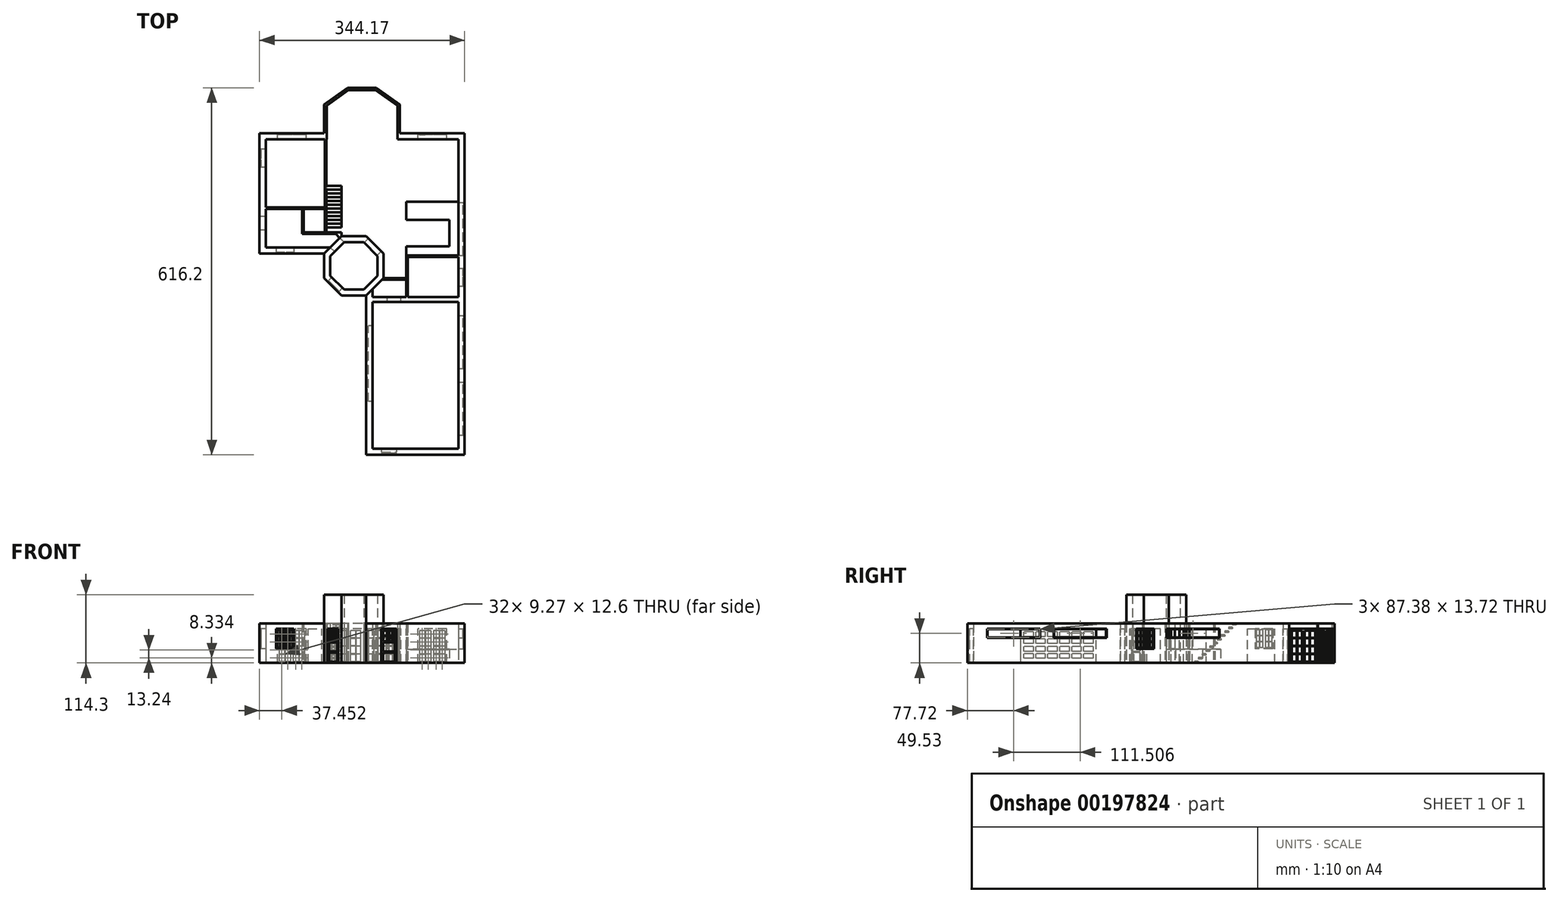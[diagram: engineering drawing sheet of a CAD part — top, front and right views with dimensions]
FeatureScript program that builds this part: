
annotation { "Feature Type Name" : "Feature", "Feature Type Description" : "" }
export const myFeature = defineFeature(function(context is Context, id is Id, definition is map)
    precondition{}
    {
        {
            var Q0;
            Q0=qCreatedBy(makeId("Top.planeOp"),FACE);
            var sketch = newSketch(context, id + "F0", { "sketchPlane" : qUnion([Q0])});
            skLineSegment(sketch, "E0", {"start": v(0, 0) * mm, "end": v(-108.59, 0) * mm});
            skLineSegment(sketch, "E1", {"start": v(-108.59, 0) * mm, "end": v(-108.59, 48.27) * mm});
            skLineSegment(sketch, "E2", {"start": v(-108.59, 48.27) * mm, "end": v(-147.95, 76.2) * mm});
            skLineSegment(sketch, "E3", {"start": v(-147.95, 76.2) * mm, "end": v(-196.22, 76.2) * mm});
            skLineSegment(sketch, "E4", {"start": v(-196.22, 76.2) * mm, "end": v(-235.59, 48.27) * mm});
            skLineSegment(sketch, "E5", {"start": v(-235.59, 48.27) * mm, "end": v(-235.59, 0) * mm});
            skLineSegment(sketch, "E6", {"start": v(-235.59, 0) * mm, "end": v(-344.17, 0) * mm});
            skLineSegment(sketch, "E7", {"start": v(-344.17, 0) * mm, "end": v(-344.17, -202.18) * mm});
            skLineSegment(sketch, "E8", {"start": v(-165.1, -540) * mm, "end": v(0, -540) * mm});
            skLineSegment(sketch, "E9", {"start": v(0, -540) * mm, "end": v(0, 0) * mm});
            skCircle(sketch, "E10.cCircle", {"center": v(-185.82, -222.9) * mm, "radius": 39.86 * mm, "construction": true});
            skLineSegment(sketch, "E10.0", {"start": v(-225.68, -239.41) * mm, "end": v(-225.68, -206.4) * mm});
            skLineSegment(sketch, "E10.1", {"start": v(-225.68, -206.4) * mm, "end": v(-202.33, -183.04) * mm});
            skLineSegment(sketch, "E10.2", {"start": v(-202.33, -183.04) * mm, "end": v(-169.3, -183.04) * mm});
            skLineSegment(sketch, "E10.3", {"start": v(-169.3, -183.04) * mm, "end": v(-145.96, -206.4) * mm});
            skLineSegment(sketch, "E10.4", {"start": v(-145.96, -206.4) * mm, "end": v(-145.96, -239.41) * mm});
            skLineSegment(sketch, "E10.5", {"start": v(-145.96, -239.41) * mm, "end": v(-169.3, -262.76) * mm});
            skLineSegment(sketch, "E10.6", {"start": v(-169.3, -262.76) * mm, "end": v(-202.33, -262.76) * mm});
            skLineSegment(sketch, "E10.7", {"start": v(-202.33, -262.76) * mm, "end": v(-225.68, -239.41) * mm});
            skPoint(sketch, "E10.0.midPoint", {"position": v(-225.68, -222.9) * mm});
            skCircle(sketch, "E11.cCircle", {"center": v(-185.82, -222.9) * mm, "radius": 50.02 * mm, "construction": true});
            skLineSegment(sketch, "E11.0", {"start": v(-235.84, -243.62) * mm, "end": v(-235.84, -202.18) * mm});
            skLineSegment(sketch, "E11.1", {"start": v(-235.84, -202.18) * mm, "end": v(-206.54, -172.88) * mm});
            skLineSegment(sketch, "E11.2", {"start": v(-206.54, -172.88) * mm, "end": v(-165.1, -172.88) * mm});
            skLineSegment(sketch, "E11.3", {"start": v(-165.1, -172.88) * mm, "end": v(-135.8, -202.18) * mm});
            skLineSegment(sketch, "E11.4", {"start": v(-135.8, -202.18) * mm, "end": v(-135.8, -243.62) * mm});
            skLineSegment(sketch, "E11.5", {"start": v(-135.8, -243.62) * mm, "end": v(-165.1, -272.92) * mm});
            skLineSegment(sketch, "E11.6", {"start": v(-165.1, -272.92) * mm, "end": v(-206.54, -272.92) * mm});
            skLineSegment(sketch, "E11.7", {"start": v(-206.54, -272.92) * mm, "end": v(-235.84, -243.62) * mm});
            skPoint(sketch, "E11.0.midPoint", {"position": v(-235.84, -222.9) * mm});
            skLineSegment(sketch, "E12", {"start": v(-235.84, -202.18) * mm, "end": v(-344.17, -202.18) * mm});
            skLineSegment(sketch, "E13", {"start": v(-165.1, -540) * mm, "end": v(-165.1, -272.92) * mm});
            skLineSegment(sketch, "E14", {"start": v(-149.3, 71.98) * mm, "end": v(-194.88, 71.98) * mm});
            skLineSegment(sketch, "E15", {"start": v(-194.88, 71.98) * mm, "end": v(-231.37, 46.1) * mm});
            skLineSegment(sketch, "E16", {"start": v(-112.8, 46.1) * mm, "end": v(-149.3, 71.98) * mm});
            skLineSegment(sketch, "E17", {"start": v(-112.8, -10.41) * mm, "end": v(-10.41, -10.41) * mm});
            skLineSegment(sketch, "E18", {"start": v(-231.37, -10.41) * mm, "end": v(-333.76, -10.41) * mm});
            skLineSegment(sketch, "E19", {"start": v(-333.76, -10.41) * mm, "end": v(-333.76, -191.77) * mm});
            skLineSegment(sketch, "E20", {"start": v(-10.41, -10.41) * mm, "end": v(-10.41, -529.6) * mm});
            skLineSegment(sketch, "E21", {"start": v(-10.41, -529.6) * mm, "end": v(-154.69, -529.6) * mm});
            skLineSegment(sketch, "E22", {"start": v(-333.76, -191.77) * mm, "end": v(-225.42, -191.77) * mm});
            skLineSegment(sketch, "E23", {"start": v(-154.69, -529.6) * mm, "end": v(-154.69, -262.5) * mm});
            skLineSegment(sketch, "E24", {"start": v(-112.8, 46.1) * mm, "end": v(-112.8, -10.41) * mm});
            skLineSegment(sketch, "E25", {"start": v(-231.37, -10.41) * mm, "end": v(-231.37, 46.1) * mm});
            skLineSegment(sketch, "E26", {"start": v(-206.54, -172.88) * mm, "end": v(-206.54, -169.42) * mm});
            skLineSegment(sketch, "E27", {"start": v(-206.54, -169.42) * mm, "end": v(-272.58, -169.42) * mm});
            skLineSegment(sketch, "E28", {"start": v(-206.54, -169.42) * mm, "end": v(-206.54, -166.88) * mm});
            skLineSegment(sketch, "E29", {"start": v(-206.54, -166.88) * mm, "end": v(-270.04, -166.88) * mm});
            skLineSegment(sketch, "E30", {"start": v(-270.04, -166.88) * mm, "end": v(-270.04, -126.93) * mm});
            skLineSegment(sketch, "E31", {"start": v(-272.58, -169.42) * mm, "end": v(-272.58, -126.93) * mm});
            skLineSegment(sketch, "E32", {"start": v(-272.58, -126.93) * mm, "end": v(-333.76, -126.93) * mm});
            skLineSegment(sketch, "E33", {"start": v(-333.76, -124.39) * mm, "end": v(-231.94, -124.39) * mm});
            skLineSegment(sketch, "E34", {"start": v(-270.04, -126.93) * mm, "end": v(-234.48, -126.93) * mm});
            skLineSegment(sketch, "E35", {"start": v(-234.48, -126.93) * mm, "end": v(-234.48, -166.88) * mm});
            skLineSegment(sketch, "E36", {"start": v(-231.94, -124.39) * mm, "end": v(-231.94, -166.88) * mm});
            skLineSegment(sketch, "E37", {"start": v(-231.94, -124.39) * mm, "end": v(-231.94, -103.89) * mm});
            skLineSegment(sketch, "E38", {"start": v(-231.94, -103.89) * mm, "end": v(-231.94, -10.41) * mm});
            skLineSegment(sketch, "E39", {"start": v(-234.48, -10.41) * mm, "end": v(-234.48, -124.39) * mm});
            skLineSegment(sketch, "E40", {"start": v(-154.69, -283.46) * mm, "end": v(-10.41, -283.46) * mm});
            skLineSegment(sketch, "E41", {"start": v(-154.69, -275.34) * mm, "end": v(-10.41, -275.34) * mm});
            skLineSegment(sketch, "E42", {"start": v(-135.8, -243.62) * mm, "end": v(-97.7, -243.62) * mm});
            skLineSegment(sketch, "E43", {"start": v(-97.7, -243.62) * mm, "end": v(-97.7, -205.52) * mm});
            skLineSegment(sketch, "E44", {"start": v(-97.7, -205.52) * mm, "end": v(-10.41, -205.52) * mm});
            skLineSegment(sketch, "E45", {"start": v(-97.7, -243.62) * mm, "end": v(-97.7, -275.34) * mm});
            skLineSegment(sketch, "E46", {"start": v(-95.16, -275.34) * mm, "end": v(-95.16, -208.06) * mm});
            skLineSegment(sketch, "E47", {"start": v(-95.16, -208.06) * mm, "end": v(-10.41, -208.06) * mm});
            skLineSegment(sketch, "E48", {"start": v(-97.7, -246.16) * mm, "end": v(-138.34, -246.16) * mm});
            skLineSegment(sketch, "E49", {"start": v(-209.51, -175.86) * mm, "end": v(-215.95, -169.42) * mm});
            skLineSegment(sketch, "E50", {"start": v(-97.7, -205.52) * mm, "end": v(-97.7, -190.28) * mm});
            skLineSegment(sketch, "E51", {"start": v(-97.7, -190.28) * mm, "end": v(-25.65, -190.28) * mm});
            skLineSegment(sketch, "E52", {"start": v(-25.65, -190.28) * mm, "end": v(-25.65, -145.5) * mm});
            skLineSegment(sketch, "E53", {"start": v(-25.65, -145.5) * mm, "end": v(-97.7, -145.5) * mm});
            skLineSegment(sketch, "E54", {"start": v(-97.7, -145.5) * mm, "end": v(-97.7, -115.03) * mm});
            skLineSegment(sketch, "E55", {"start": v(-97.7, -115.03) * mm, "end": v(-10.41, -115.03) * mm});
            skSolve(sketch);
        }
        {
            var Q0;
            Q0=makeQuery(id+"F0.imprint","IMPRINT",FACE,{"disambiguationData":[TD([[makeQuery(id+"F0.imprint","IMPRINT",EDGE,{"derivedFrom":sQuery(id+"F0.wireOp",EDGE,"E0")}),1.0]])]});
            var Q1;
            {var subQ1=sQuery(id+"F0.wireOp",EDGE,"E37");Q1=makeQuery(id+"F0.imprint","IMPRINT",FACE,{"disambiguationData":[TD([[makeQuery(id+"F0.imprint","IMPRINT",EDGE,{"derivedFrom":subQ1}),1.0]])]});}
            var Q2;
            {var subQ8=sQuery(id+"F0.wireOp",EDGE,"E28");Q2=makeQuery(id+"F0.imprint","IMPRINT",FACE,{"disambiguationData":[TD([[makeQuery(id+"F0.imprint","IMPRINT",EDGE,{"derivedFrom":subQ8}),1.0]])]});}
            var Q3;
            {var subQ0=sQuery(id+"F0.wireOp",EDGE,"E26");Q3=makeQuery(id+"F0.imprint","IMPRINT",FACE,{"disambiguationData":[TD([[makeQuery(id+"F0.imprint","IMPRINT",EDGE,{"derivedFrom":subQ0}),1.0]])]});}
            var Q4;
            {var subQ1=sQuery(id+"F0.wireOp",EDGE,"E43");Q4=makeQuery(id+"F0.imprint","IMPRINT",FACE,{"disambiguationData":[TD([[makeQuery(id+"F0.imprint","IMPRINT",EDGE,{"derivedFrom":subQ1}),-1.0]])]});}
            var Q5;
            {var subQ0=sQuery(id+"F0.wireOp",EDGE,"E42");Q5=makeQuery(id+"F0.imprint","IMPRINT",FACE,{"disambiguationData":[TD([[makeQuery(id+"F0.imprint","IMPRINT",EDGE,{"derivedFrom":subQ0}),-1.0]])]});}
            var Q6;
            {var subQ4=sQuery(id+"F0.wireOp",EDGE,"E40");Q6=makeQuery(id+"F0.imprint","IMPRINT",FACE,{"disambiguationData":[TD([[makeQuery(id+"F0.imprint","IMPRINT",EDGE,{"derivedFrom":subQ4}),1.0]])]});}
            extrude(context, id + "F1", {"entities" : qUnion([Q0, Q1, Q2, Q3, Q4, Q5, Q6]), "depth" : 66.04 * mm});
        }
        {
            var Q0;
            {var subQ0=sQuery(id+"F0.wireOp",EDGE,"E44");Q0=makeQuery(id+"F0.imprint","IMPRINT",FACE,{"disambiguationData":[TD([[makeQuery(id+"F0.imprint","IMPRINT",EDGE,{"derivedFrom":subQ0}),1.0]])]});}
            extrude(context, id + "F2", {"entities" : qUnion([Q0]), "operationType" : NewBodyOperationType.ADD, "depth" : 22.86 * mm});
        }
        {
            var Q0;
            Q0=makeQuery(id+"F0.imprint","IMPRINT",FACE,{"disambiguationData":[TD([[makeQuery(id+"F0.imprint","IMPRINT",EDGE,{"derivedFrom":sQuery(id+"F0.wireOp",EDGE,"E10.0")}),1.0]])]});
            extrude(context, id + "F3", {"entities" : qUnion([Q0]), "operationType" : NewBodyOperationType.ADD, "depth" : 114.3 * mm});
        }
        {
            var Q0;
            Q0=makeQuery(id+"F3.opExtrude","SWEPT_FACE",FACE,{"disambiguationData":[OSD([sQuery(id+"F0.wireOp",EDGE,"E11.7")])]});
            var sketch = newSketch(context, id + "F4", { "sketchPlane" : qUnion([Q0])});
            skLineSegment(sketch, "E56.bottom", {"start": v(13.54, 0) * mm, "end": v(38.94, 0) * mm});
            skLineSegment(sketch, "E56.top", {"start": v(13.54, 57.15) * mm, "end": v(38.94, 57.15) * mm});
            skLineSegment(sketch, "E56.left", {"start": v(13.54, 0) * mm, "end": v(13.54, 57.15) * mm});
            skLineSegment(sketch, "E56.right", {"start": v(38.94, 0) * mm, "end": v(38.94, 57.15) * mm});
            skLineSegment(sketch, "E57", {"start": v(14.3, 0) * mm, "end": v(14.3, 56.39) * mm});
            skLineSegment(sketch, "E58", {"start": v(14.3, 56.39) * mm, "end": v(38.18, 56.39) * mm});
            skLineSegment(sketch, "E59", {"start": v(38.18, 56.39) * mm, "end": v(38.18, 0) * mm});
            skLineSegment(sketch, "E60.bottom", {"start": v(16.33, 17.27) * mm, "end": v(36.15, 17.27) * mm});
            skLineSegment(sketch, "E60.top", {"start": v(16.33, 2.03) * mm, "end": v(36.15, 2.03) * mm});
            skLineSegment(sketch, "E60.left", {"start": v(16.33, 17.27) * mm, "end": v(16.33, 2.03) * mm});
            skLineSegment(sketch, "E60.right", {"start": v(36.15, 17.27) * mm, "end": v(36.15, 2.03) * mm});
            skPoint(sketch, "E61.oppositeSnap0", {"position": v(36.15, 9.65) * mm});
            skLineSegment(sketch, "E61.bottom", {"start": v(16.33, 34.54) * mm, "end": v(36.15, 34.54) * mm});
            skLineSegment(sketch, "E61.top", {"start": v(16.33, 19.3) * mm, "end": v(36.15, 19.3) * mm});
            skLineSegment(sketch, "E61.left", {"start": v(16.33, 34.54) * mm, "end": v(16.33, 19.3) * mm});
            skLineSegment(sketch, "E61.right", {"start": v(36.15, 34.54) * mm, "end": v(36.15, 19.3) * mm});
            skLineSegment(sketch, "E62.bottom", {"start": v(16.33, 54.36) * mm, "end": v(25.92, 54.36) * mm});
            skLineSegment(sketch, "E62.top", {"start": v(16.33, 45.78) * mm, "end": v(25.92, 45.78) * mm});
            skLineSegment(sketch, "E62.left", {"start": v(16.33, 54.36) * mm, "end": v(16.33, 45.78) * mm});
            skLineSegment(sketch, "E62.right", {"start": v(25.92, 54.36) * mm, "end": v(25.92, 45.78) * mm});
            skLineSegment(sketch, "E63.bottom", {"start": v(26.56, 54.36) * mm, "end": v(36.15, 54.36) * mm});
            skLineSegment(sketch, "E63.top", {"start": v(26.56, 45.78) * mm, "end": v(36.15, 45.78) * mm});
            skLineSegment(sketch, "E63.left", {"start": v(26.56, 54.36) * mm, "end": v(26.56, 45.78) * mm});
            skLineSegment(sketch, "E63.right", {"start": v(36.15, 54.36) * mm, "end": v(36.15, 45.78) * mm});
            skLineSegment(sketch, "E64.bottom", {"start": v(36.15, 45.15) * mm, "end": v(26.56, 45.15) * mm});
            skLineSegment(sketch, "E64.top", {"start": v(36.15, 36.58) * mm, "end": v(26.56, 36.58) * mm});
            skLineSegment(sketch, "E64.left", {"start": v(36.15, 45.15) * mm, "end": v(36.15, 36.58) * mm});
            skLineSegment(sketch, "E64.right", {"start": v(26.56, 45.15) * mm, "end": v(26.56, 36.58) * mm});
            skLineSegment(sketch, "E65.bottom", {"start": v(25.92, 45.15) * mm, "end": v(16.33, 45.15) * mm});
            skLineSegment(sketch, "E65.top", {"start": v(25.92, 36.58) * mm, "end": v(16.33, 36.58) * mm});
            skLineSegment(sketch, "E65.left", {"start": v(25.92, 45.15) * mm, "end": v(25.92, 36.58) * mm});
            skLineSegment(sketch, "E65.right", {"start": v(16.33, 45.15) * mm, "end": v(16.33, 36.58) * mm});
            skSolve(sketch);
        }
        {
            var Q0;
            Q0 = qSketchRegion(id + "F4", true);
            var Q1;
            {var subQ1=sQuery(id+"F4.wireOp",EDGE,"wZGJqwOu-hPp5-KiIY-bGTE-YoklEwD7c8TK");Q1=makeQuery(id+"F4.imprint","IMPRINT",FACE,{"disambiguationData":[TD([[makeQuery(id+"F4.imprint","IMPRINT",EDGE,{"derivedFrom":subQ1}),-1.0]])]});}
            var Q2;
            Q2=makeQuery(id+"F4.imprint","IMPRINT",FACE,{"disambiguationData":[TD([[makeQuery(id+"F4.imprint","IMPRINT",EDGE,{"derivedFrom":sQuery(id+"F4.wireOp",EDGE,"E62.bottom")}),-1.0]])]});
            var Q3;
            Q3=makeQuery(id+"F4.imprint","IMPRINT",FACE,{"disambiguationData":[TD([[makeQuery(id+"F4.imprint","IMPRINT",EDGE,{"derivedFrom":sQuery(id+"F4.wireOp",EDGE,"E63.bottom")}),-1.0]])]});
            var Q4;
            Q4=makeQuery(id+"F4.imprint","IMPRINT",FACE,{"disambiguationData":[TD([[makeQuery(id+"F4.imprint","IMPRINT",EDGE,{"derivedFrom":sQuery(id+"F4.wireOp",EDGE,"E64.bottom")}),1.0]])]});
            var Q5;
            Q5=makeQuery(id+"F4.imprint","IMPRINT",FACE,{"disambiguationData":[TD([[makeQuery(id+"F4.imprint","IMPRINT",EDGE,{"derivedFrom":sQuery(id+"F4.wireOp",EDGE,"E65.bottom")}),1.0]])]});
            var Q6;
            Q6=makeQuery(id+"F4.imprint","IMPRINT",FACE,{"disambiguationData":[TD([[makeQuery(id+"F4.imprint","IMPRINT",EDGE,{"derivedFrom":sQuery(id+"F4.wireOp",EDGE,"E61.bottom")}),-1.0]])]});
            var Q7;
            Q7=makeQuery(id+"F4.imprint","IMPRINT",FACE,{"disambiguationData":[TD([[makeQuery(id+"F4.imprint","IMPRINT",EDGE,{"derivedFrom":sQuery(id+"F4.wireOp",EDGE,"E60.bottom")}),-1.0]])]});
            extrude(context, id + "F5", {"entities" : qUnion([Q0, Q1, Q2, Q3, Q4, Q5, Q6, Q7]), "operationType" : NewBodyOperationType.REMOVE, "oppositeDirection" : true, "depth" : 10.16 * mm});
        }
        {
            var Q0;
            Q0 = qSketchRegion(id + "F4", true);
            extrude(context, id + "F6", {"entities" : qUnion([Q0]), "operationType" : NewBodyOperationType.ADD, "oppositeDirection" : true, "depth" : 2.54 * mm, "hasSecondDirection" : true, "secondDirectionOppositeDirection" : true, "secondDirectionDepth" : 1.27 * mm});
        }
        {
            var Q0;
            Q0=makeQuery(id+"F4.imprint","IMPRINT",FACE,{"disambiguationData":[TD([[makeQuery(id+"F4.imprint","IMPRINT",EDGE,{"derivedFrom":sQuery(id+"F4.wireOp",EDGE,"E61.bottom")}),-1.0]])]});
            var Q1;
            Q1=makeQuery(id+"F4.imprint","IMPRINT",FACE,{"disambiguationData":[TD([[makeQuery(id+"F4.imprint","IMPRINT",EDGE,{"derivedFrom":sQuery(id+"F4.wireOp",EDGE,"E60.bottom")}),-1.0]])]});
            extrude(context, id + "F7", {"entities" : qUnion([Q0, Q1]), "operationType" : NewBodyOperationType.ADD, "oppositeDirection" : true, "depth" : 2.54 * mm, "hasSecondDirection" : true, "secondDirectionOppositeDirection" : true, "secondDirectionDepth" : 0.89 * mm});
        }
        {
            var Q0;
            Q0=makeQuery(id+"F1.opExtrude","SWEPT_FACE",FACE,{"disambiguationData":[OSD([sQuery(id+"F0.wireOp",EDGE,"E13")])]});
            var sketch = newSketch(context, id + "F8", { "sketchPlane" : qUnion([Q0])});
            skPoint(sketch, "E66.endSnap0", {"position": v(272.92, 33.02) * mm});
            skLineSegment(sketch, "E67", {"start": v(323.72, 0) * mm, "end": v(323.72, 57.15) * mm});
            skLineSegment(sketch, "E68", {"start": v(323.72, 57.15) * mm, "end": v(450.72, 57.15) * mm});
            skLineSegment(sketch, "E69", {"start": v(450.72, 57.15) * mm, "end": v(450.72, 0) * mm});
            skLineSegment(sketch, "E70.bottom", {"start": v(328.8, 52.07) * mm, "end": v(345.1, 52.07) * mm});
            skLineSegment(sketch, "E70.top", {"start": v(328.8, 44.13) * mm, "end": v(345.1, 44.13) * mm});
            skLineSegment(sketch, "E70.left", {"start": v(328.8, 52.07) * mm, "end": v(328.8, 44.13) * mm});
            skLineSegment(sketch, "E70.right", {"start": v(345.1, 52.07) * mm, "end": v(345.1, 44.13) * mm});
            skLineSegment(sketch, "E71.bottom", {"start": v(348.9, 52.07) * mm, "end": v(365.2, 52.07) * mm});
            skLineSegment(sketch, "E71.top", {"start": v(348.9, 44.13) * mm, "end": v(365.2, 44.13) * mm});
            skLineSegment(sketch, "E71.left", {"start": v(348.9, 52.07) * mm, "end": v(348.9, 44.13) * mm});
            skLineSegment(sketch, "E71.right", {"start": v(365.2, 52.07) * mm, "end": v(365.2, 44.13) * mm});
            skLineSegment(sketch, "E72.bottom", {"start": v(369.02, 52.07) * mm, "end": v(385.32, 52.07) * mm});
            skLineSegment(sketch, "E72.top", {"start": v(369.02, 44.13) * mm, "end": v(385.32, 44.13) * mm});
            skLineSegment(sketch, "E72.left", {"start": v(369.02, 52.07) * mm, "end": v(369.02, 44.13) * mm});
            skLineSegment(sketch, "E72.right", {"start": v(385.32, 52.07) * mm, "end": v(385.32, 44.13) * mm});
            skLineSegment(sketch, "E73.bottom", {"start": v(389.13, 52.07) * mm, "end": v(405.42, 52.07) * mm});
            skLineSegment(sketch, "E73.top", {"start": v(389.13, 44.13) * mm, "end": v(405.42, 44.13) * mm});
            skLineSegment(sketch, "E73.left", {"start": v(389.13, 52.07) * mm, "end": v(389.13, 44.13) * mm});
            skLineSegment(sketch, "E73.right", {"start": v(405.42, 52.07) * mm, "end": v(405.42, 44.13) * mm});
            skLineSegment(sketch, "E74.bottom", {"start": v(409.23, 52.07) * mm, "end": v(425.53, 52.07) * mm});
            skLineSegment(sketch, "E74.top", {"start": v(409.23, 44.13) * mm, "end": v(425.53, 44.13) * mm});
            skLineSegment(sketch, "E74.left", {"start": v(409.23, 52.07) * mm, "end": v(409.23, 44.13) * mm});
            skLineSegment(sketch, "E74.right", {"start": v(425.53, 52.07) * mm, "end": v(425.53, 44.13) * mm});
            skLineSegment(sketch, "E75.bottom", {"start": v(429.34, 52.07) * mm, "end": v(445.64, 52.07) * mm});
            skLineSegment(sketch, "E75.top", {"start": v(429.34, 44.13) * mm, "end": v(445.64, 44.13) * mm});
            skLineSegment(sketch, "E75.left", {"start": v(429.34, 52.07) * mm, "end": v(429.34, 44.13) * mm});
            skLineSegment(sketch, "E75.right", {"start": v(445.64, 52.07) * mm, "end": v(445.64, 44.13) * mm});
            skLineSegment(sketch, "E76.bottom", {"start": v(328.8, 40.32) * mm, "end": v(345.1, 40.32) * mm});
            skLineSegment(sketch, "E76.top", {"start": v(328.8, 32.39) * mm, "end": v(345.1, 32.39) * mm});
            skLineSegment(sketch, "E76.left", {"start": v(328.8, 40.32) * mm, "end": v(328.8, 32.39) * mm});
            skLineSegment(sketch, "E76.right", {"start": v(345.1, 40.32) * mm, "end": v(345.1, 32.39) * mm});
            skLineSegment(sketch, "E77.bottom", {"start": v(348.9, 40.32) * mm, "end": v(365.2, 40.32) * mm});
            skLineSegment(sketch, "E77.top", {"start": v(348.9, 32.39) * mm, "end": v(365.2, 32.39) * mm});
            skLineSegment(sketch, "E77.left", {"start": v(348.9, 40.32) * mm, "end": v(348.9, 32.39) * mm});
            skLineSegment(sketch, "E77.right", {"start": v(365.2, 40.32) * mm, "end": v(365.2, 32.39) * mm});
            skLineSegment(sketch, "E78.bottom", {"start": v(369.02, 40.32) * mm, "end": v(385.32, 40.32) * mm});
            skLineSegment(sketch, "E78.top", {"start": v(369.02, 32.39) * mm, "end": v(385.32, 32.39) * mm});
            skLineSegment(sketch, "E78.left", {"start": v(369.02, 40.32) * mm, "end": v(369.02, 32.39) * mm});
            skLineSegment(sketch, "E78.right", {"start": v(385.32, 40.32) * mm, "end": v(385.32, 32.39) * mm});
            skLineSegment(sketch, "E79.bottom", {"start": v(389.13, 40.32) * mm, "end": v(405.42, 40.32) * mm});
            skLineSegment(sketch, "E79.top", {"start": v(389.13, 32.39) * mm, "end": v(405.42, 32.39) * mm});
            skLineSegment(sketch, "E79.left", {"start": v(389.13, 40.32) * mm, "end": v(389.13, 32.39) * mm});
            skLineSegment(sketch, "E79.right", {"start": v(405.42, 40.32) * mm, "end": v(405.42, 32.39) * mm});
            skLineSegment(sketch, "E80.bottom", {"start": v(409.23, 40.32) * mm, "end": v(425.53, 40.32) * mm});
            skLineSegment(sketch, "E80.top", {"start": v(409.23, 32.39) * mm, "end": v(425.53, 32.39) * mm});
            skLineSegment(sketch, "E80.left", {"start": v(409.23, 40.32) * mm, "end": v(409.23, 32.39) * mm});
            skLineSegment(sketch, "E80.right", {"start": v(425.53, 40.32) * mm, "end": v(425.53, 32.39) * mm});
            skLineSegment(sketch, "E81.bottom", {"start": v(429.34, 40.32) * mm, "end": v(445.64, 40.32) * mm});
            skLineSegment(sketch, "E81.top", {"start": v(429.34, 32.39) * mm, "end": v(445.64, 32.39) * mm});
            skLineSegment(sketch, "E81.left", {"start": v(429.34, 40.32) * mm, "end": v(429.34, 32.39) * mm});
            skLineSegment(sketch, "E81.right", {"start": v(445.64, 40.32) * mm, "end": v(445.64, 32.39) * mm});
            skLineSegment(sketch, "E82.bottom", {"start": v(328.8, 27.3) * mm, "end": v(345.1, 27.3) * mm});
            skLineSegment(sketch, "E82.top", {"start": v(328.8, 19.37) * mm, "end": v(345.1, 19.37) * mm});
            skLineSegment(sketch, "E82.left", {"start": v(328.8, 27.3) * mm, "end": v(328.8, 19.37) * mm});
            skLineSegment(sketch, "E82.right", {"start": v(345.1, 27.3) * mm, "end": v(345.1, 19.37) * mm});
            skLineSegment(sketch, "E83.bottom", {"start": v(348.9, 27.3) * mm, "end": v(365.2, 27.3) * mm});
            skLineSegment(sketch, "E83.top", {"start": v(348.9, 19.37) * mm, "end": v(365.2, 19.37) * mm});
            skLineSegment(sketch, "E83.left", {"start": v(348.9, 27.3) * mm, "end": v(348.9, 19.37) * mm});
            skLineSegment(sketch, "E83.right", {"start": v(365.2, 27.3) * mm, "end": v(365.2, 19.37) * mm});
            skLineSegment(sketch, "E84.bottom", {"start": v(369.02, 27.3) * mm, "end": v(385.32, 27.3) * mm});
            skLineSegment(sketch, "E84.top", {"start": v(369.02, 19.37) * mm, "end": v(385.32, 19.37) * mm});
            skLineSegment(sketch, "E84.left", {"start": v(369.02, 27.3) * mm, "end": v(369.02, 19.37) * mm});
            skLineSegment(sketch, "E84.right", {"start": v(385.32, 27.3) * mm, "end": v(385.32, 19.37) * mm});
            skLineSegment(sketch, "E85.bottom", {"start": v(389.13, 27.3) * mm, "end": v(405.42, 27.3) * mm});
            skLineSegment(sketch, "E85.top", {"start": v(389.13, 19.37) * mm, "end": v(405.42, 19.37) * mm});
            skLineSegment(sketch, "E85.left", {"start": v(389.13, 27.3) * mm, "end": v(389.13, 19.37) * mm});
            skLineSegment(sketch, "E85.right", {"start": v(405.42, 27.3) * mm, "end": v(405.42, 19.37) * mm});
            skLineSegment(sketch, "E86.bottom", {"start": v(409.23, 27.3) * mm, "end": v(425.53, 27.3) * mm});
            skLineSegment(sketch, "E86.top", {"start": v(409.23, 19.37) * mm, "end": v(425.53, 19.37) * mm});
            skLineSegment(sketch, "E86.left", {"start": v(409.23, 27.3) * mm, "end": v(409.23, 19.37) * mm});
            skLineSegment(sketch, "E86.right", {"start": v(425.53, 27.3) * mm, "end": v(425.53, 19.37) * mm});
            skLineSegment(sketch, "E87.bottom", {"start": v(429.34, 27.3) * mm, "end": v(445.64, 27.3) * mm});
            skLineSegment(sketch, "E87.top", {"start": v(429.34, 19.37) * mm, "end": v(445.64, 19.37) * mm});
            skLineSegment(sketch, "E87.left", {"start": v(429.34, 27.3) * mm, "end": v(429.34, 19.37) * mm});
            skLineSegment(sketch, "E87.right", {"start": v(445.64, 27.3) * mm, "end": v(445.64, 19.37) * mm});
            skLineSegment(sketch, "E88.bottom", {"start": v(328.8, 15.56) * mm, "end": v(345.1, 15.56) * mm});
            skLineSegment(sketch, "E88.top", {"start": v(328.8, 7.62) * mm, "end": v(345.1, 7.62) * mm});
            skLineSegment(sketch, "E88.left", {"start": v(328.8, 15.56) * mm, "end": v(328.8, 7.62) * mm});
            skLineSegment(sketch, "E88.right", {"start": v(345.1, 15.56) * mm, "end": v(345.1, 7.62) * mm});
            skLineSegment(sketch, "E89.bottom", {"start": v(348.9, 15.56) * mm, "end": v(365.2, 15.56) * mm});
            skLineSegment(sketch, "E89.top", {"start": v(348.9, 7.62) * mm, "end": v(365.2, 7.62) * mm});
            skLineSegment(sketch, "E89.left", {"start": v(348.9, 15.56) * mm, "end": v(348.9, 7.62) * mm});
            skLineSegment(sketch, "E89.right", {"start": v(365.2, 15.56) * mm, "end": v(365.2, 7.62) * mm});
            skLineSegment(sketch, "E90.bottom", {"start": v(369.02, 15.56) * mm, "end": v(385.32, 15.56) * mm});
            skLineSegment(sketch, "E90.top", {"start": v(369.02, 7.62) * mm, "end": v(385.32, 7.62) * mm});
            skLineSegment(sketch, "E90.left", {"start": v(369.02, 15.56) * mm, "end": v(369.02, 7.62) * mm});
            skLineSegment(sketch, "E90.right", {"start": v(385.32, 15.56) * mm, "end": v(385.32, 7.62) * mm});
            skLineSegment(sketch, "E91.bottom", {"start": v(389.13, 15.56) * mm, "end": v(405.42, 15.56) * mm});
            skLineSegment(sketch, "E91.top", {"start": v(389.13, 7.62) * mm, "end": v(405.42, 7.62) * mm});
            skLineSegment(sketch, "E91.left", {"start": v(389.13, 15.56) * mm, "end": v(389.13, 7.62) * mm});
            skLineSegment(sketch, "E91.right", {"start": v(405.42, 15.56) * mm, "end": v(405.42, 7.62) * mm});
            skLineSegment(sketch, "E92.bottom", {"start": v(409.23, 15.56) * mm, "end": v(425.53, 15.56) * mm});
            skLineSegment(sketch, "E92.top", {"start": v(409.23, 7.62) * mm, "end": v(425.53, 7.62) * mm});
            skLineSegment(sketch, "E92.left", {"start": v(409.23, 15.56) * mm, "end": v(409.23, 7.62) * mm});
            skLineSegment(sketch, "E92.right", {"start": v(425.53, 15.56) * mm, "end": v(425.53, 7.62) * mm});
            skLineSegment(sketch, "E93.bottom", {"start": v(429.34, 15.56) * mm, "end": v(445.64, 15.56) * mm});
            skLineSegment(sketch, "E93.top", {"start": v(429.34, 7.62) * mm, "end": v(445.64, 7.62) * mm});
            skLineSegment(sketch, "E93.left", {"start": v(429.34, 15.56) * mm, "end": v(429.34, 7.62) * mm});
            skLineSegment(sketch, "E93.right", {"start": v(445.64, 15.56) * mm, "end": v(445.64, 7.62) * mm});
            skSolve(sketch);
        }
        {
            var Q0;
            Q0 = qSketchRegion(id + "F8", true);
            var Q1;
            {var subQ0=sQuery(id+"F8.wireOp",EDGE,"E67");Q1=makeQuery(id+"F8.imprint","IMPRINT",FACE,{"disambiguationData":[TD([[makeQuery(id+"F8.imprint","IMPRINT",EDGE,{"derivedFrom":subQ0}),-1.0]])]});}
            extrude(context, id + "F9", {"entities" : qUnion([Q0, Q1]), "operationType" : NewBodyOperationType.REMOVE, "oppositeDirection" : true, "depth" : 10.4 * mm});
        }
        {
            var Q0;
            {var subQ1=sQuery(id+"F8.wireOp",EDGE,"E67");Q0=makeQuery(id+"F8.imprint","IMPRINT",FACE,{"disambiguationData":[TD([[makeQuery(id+"F8.imprint","IMPRINT",EDGE,{"derivedFrom":subQ1}),-1.0]])]});}
            extrude(context, id + "F10", {"entities" : qUnion([Q0]), "operationType" : NewBodyOperationType.ADD, "oppositeDirection" : true, "depth" : 3.8 * mm, "hasSecondDirection" : true, "secondDirectionOppositeDirection" : true, "secondDirectionDepth" : 1.27 * mm});
        }
        {
            var Q0;
            Q0 = qSketchRegion(id + "F8", true);
            extrude(context, id + "F11", {"entities" : qUnion([Q0]), "operationType" : NewBodyOperationType.ADD, "oppositeDirection" : true, "depth" : 3.8 * mm, "hasSecondDirection" : true, "secondDirectionOppositeDirection" : true, "secondDirectionDepth" : 1.14 * mm});
        }
        {
            var Q0;
            Q0=makeQuery(id+"F1.opExtrude","SWEPT_FACE",FACE,{"disambiguationData":[OSD([sQuery(id+"F0.wireOp",EDGE,"E12")])]});
            var sketch = newSketch(context, id + "F12", { "sketchPlane" : qUnion([Q0])});
            skLineSegment(sketch, "E94.bottom", {"start": v(-316.6, 57.15) * mm, "end": v(-286.64, 57.15) * mm});
            skLineSegment(sketch, "E94.top", {"start": v(-316.6, 23.62) * mm, "end": v(-286.64, 23.62) * mm});
            skLineSegment(sketch, "E94.left", {"start": v(-316.6, 57.15) * mm, "end": v(-316.6, 23.62) * mm});
            skLineSegment(sketch, "E94.right", {"start": v(-286.64, 57.15) * mm, "end": v(-286.64, 23.62) * mm});
            skLineSegment(sketch, "E95.bottom", {"start": v(-299.43, 55.12) * mm, "end": v(-288.67, 55.12) * mm});
            skLineSegment(sketch, "E95.top", {"start": v(-299.43, 25.65) * mm, "end": v(-288.67, 25.65) * mm});
            skLineSegment(sketch, "E95.left", {"start": v(-299.43, 55.12) * mm, "end": v(-299.43, 25.65) * mm});
            skLineSegment(sketch, "E95.right", {"start": v(-288.67, 55.12) * mm, "end": v(-288.67, 25.65) * mm});
            skLineSegment(sketch, "E96", {"start": v(-293.71, 55.12) * mm, "end": v(-293.71, 25.65) * mm});
            skLineSegment(sketch, "E97", {"start": v(-294.35, 55.12) * mm, "end": v(-294.35, 25.65) * mm});
            skLineSegment(sketch, "E98", {"start": v(-299.43, 45.72) * mm, "end": v(-288.67, 45.72) * mm});
            skLineSegment(sketch, "E99", {"start": v(-299.43, 45.09) * mm, "end": v(-288.67, 45.09) * mm});
            skLineSegment(sketch, "E100", {"start": v(-299.43, 35.69) * mm, "end": v(-288.67, 35.69) * mm});
            skLineSegment(sketch, "E101", {"start": v(-299.43, 35.05) * mm, "end": v(-288.67, 35.05) * mm});
            skLineSegment(sketch, "E102", {"start": v(-294.35, 55.12) * mm, "end": v(-294.35, 45.09) * mm});
            skLineSegment(sketch, "E103", {"start": v(-294.35, 55.12) * mm, "end": v(-294.35, 45.72) * mm});
            skLineSegment(sketch, "E104", {"start": v(-294.35, 45.72) * mm, "end": v(-294.35, 45.09) * mm});
            skLineSegment(sketch, "E105", {"start": v(-294.35, 45.09) * mm, "end": v(-294.35, 35.69) * mm});
            skLineSegment(sketch, "E106", {"start": v(-294.35, 35.69) * mm, "end": v(-294.35, 35.05) * mm});
            skLineSegment(sketch, "E107", {"start": v(-294.35, 35.05) * mm, "end": v(-294.35, 25.65) * mm});
            skLineSegment(sketch, "E108.bottom", {"start": v(-314.58, 55.12) * mm, "end": v(-303.82, 55.12) * mm});
            skLineSegment(sketch, "E108.top", {"start": v(-314.58, 25.65) * mm, "end": v(-303.82, 25.65) * mm});
            skLineSegment(sketch, "E108.left", {"start": v(-314.58, 55.12) * mm, "end": v(-314.58, 25.65) * mm});
            skLineSegment(sketch, "E108.right", {"start": v(-303.82, 55.12) * mm, "end": v(-303.82, 25.65) * mm});
            skLineSegment(sketch, "E109", {"start": v(-308.89, 55.12) * mm, "end": v(-308.89, 25.65) * mm});
            skLineSegment(sketch, "E110", {"start": v(-309.52, 55.12) * mm, "end": v(-309.52, 25.65) * mm});
            skLineSegment(sketch, "E111", {"start": v(-314.58, 45.72) * mm, "end": v(-303.82, 45.72) * mm});
            skLineSegment(sketch, "E112", {"start": v(-314.58, 45.09) * mm, "end": v(-303.82, 45.09) * mm});
            skLineSegment(sketch, "E113", {"start": v(-314.58, 35.69) * mm, "end": v(-303.82, 35.69) * mm});
            skLineSegment(sketch, "E114", {"start": v(-314.58, 35.05) * mm, "end": v(-303.82, 35.05) * mm});
            skLineSegment(sketch, "E115", {"start": v(-309.52, 55.12) * mm, "end": v(-309.52, 45.09) * mm});
            skLineSegment(sketch, "E116", {"start": v(-309.52, 55.12) * mm, "end": v(-309.52, 45.72) * mm});
            skLineSegment(sketch, "E117", {"start": v(-309.52, 45.72) * mm, "end": v(-309.52, 45.09) * mm});
            skLineSegment(sketch, "E118", {"start": v(-309.52, 45.09) * mm, "end": v(-309.52, 35.69) * mm});
            skLineSegment(sketch, "E119", {"start": v(-309.52, 35.69) * mm, "end": v(-309.52, 35.05) * mm});
            skLineSegment(sketch, "E120", {"start": v(-309.52, 35.05) * mm, "end": v(-309.52, 25.65) * mm});
            skLineSegment(sketch, "E121.bottom", {"start": v(-315.85, 56.39) * mm, "end": v(-287.4, 56.39) * mm});
            skLineSegment(sketch, "E121.top", {"start": v(-315.85, 24.38) * mm, "end": v(-287.4, 24.38) * mm});
            skLineSegment(sketch, "E121.left", {"start": v(-315.85, 56.39) * mm, "end": v(-315.85, 24.38) * mm});
            skLineSegment(sketch, "E121.right", {"start": v(-287.4, 56.39) * mm, "end": v(-287.4, 24.38) * mm});
            skLineSegment(sketch, "E122", {"start": v(-302, 24.38) * mm, "end": v(-302, 56.39) * mm});
            skLineSegment(sketch, "E123", {"start": v(-301.24, 56.39) * mm, "end": v(-301.24, 24.38) * mm});
            skSolve(sketch);
        }
        {
            var Q0;
            {var subQ0=sQuery(id+"F12.wireOp",EDGE,"E108.left");var subQ1=sQuery(id+"F12.wireOp",EDGE,"E108.bottom");var subQ2=makeQuery(id+"F12.imprint","INTERSECT",VERTEX,{"derivedFrom":[subQ1,subQ0]});Q0=makeQuery(id+"F12.imprint","IMPRINT",FACE,{"disambiguationData":[TD([[makeQuery(id+"F12.imprint","IMPRINT",EDGE,{"disambiguationData":[TD([[subQ2,-1.0]])],"derivedFrom":subQ1}),-1.0]])]});}
            var Q1;
            {var subQ0=sQuery(id+"F12.wireOp",EDGE,"E109");var subQ1=sQuery(id+"F12.wireOp",EDGE,"E108.bottom");var subQ2=makeQuery(id+"F12.imprint","INTERSECT",VERTEX,{"derivedFrom":[subQ1,subQ0]});Q1=makeQuery(id+"F12.imprint","IMPRINT",FACE,{"disambiguationData":[TD([[makeQuery(id+"F12.imprint","IMPRINT",EDGE,{"disambiguationData":[TD([[subQ2,-1.0]])],"derivedFrom":subQ1}),-1.0]])]});}
            var Q2;
            {var subQ0=sQuery(id+"F12.wireOp",EDGE,"E112");var subQ1=sQuery(id+"F12.wireOp",EDGE,"E108.right");var subQ2=makeQuery(id+"F12.imprint","INTERSECT",VERTEX,{"derivedFrom":[subQ1,subQ0]});Q2=makeQuery(id+"F12.imprint","IMPRINT",FACE,{"disambiguationData":[TD([[makeQuery(id+"F12.imprint","IMPRINT",EDGE,{"disambiguationData":[TD([[subQ2,-1.0]])],"derivedFrom":subQ1}),-1.0]])]});}
            var Q3;
            {var subQ0=sQuery(id+"F12.wireOp",EDGE,"E112");var subQ1=sQuery(id+"F12.wireOp",EDGE,"E108.left");var subQ2=makeQuery(id+"F12.imprint","INTERSECT",VERTEX,{"derivedFrom":[subQ1,subQ0]});Q3=makeQuery(id+"F12.imprint","IMPRINT",FACE,{"disambiguationData":[TD([[makeQuery(id+"F12.imprint","IMPRINT",EDGE,{"disambiguationData":[TD([[subQ2,-1.0]])],"derivedFrom":subQ1}),1.0]])]});}
            var Q4;
            {var subQ0=sQuery(id+"F12.wireOp",EDGE,"E108.left");var subQ1=sQuery(id+"F12.wireOp",EDGE,"E108.top");var subQ2=makeQuery(id+"F12.imprint","INTERSECT",VERTEX,{"derivedFrom":[subQ1,subQ0]});Q4=makeQuery(id+"F12.imprint","IMPRINT",FACE,{"disambiguationData":[TD([[makeQuery(id+"F12.imprint","IMPRINT",EDGE,{"disambiguationData":[TD([[subQ2,-1.0]])],"derivedFrom":subQ1}),1.0]])]});}
            var Q5;
            {var subQ0=sQuery(id+"F12.wireOp",EDGE,"E109");var subQ1=sQuery(id+"F12.wireOp",EDGE,"E108.top");var subQ2=makeQuery(id+"F12.imprint","INTERSECT",VERTEX,{"derivedFrom":[subQ1,subQ0]});Q5=makeQuery(id+"F12.imprint","IMPRINT",FACE,{"disambiguationData":[TD([[makeQuery(id+"F12.imprint","IMPRINT",EDGE,{"disambiguationData":[TD([[subQ2,-1.0]])],"derivedFrom":subQ1}),1.0]])]});}
            var Q6;
            {var subQ0=sQuery(id+"F12.wireOp",EDGE,"E95.left");var subQ1=sQuery(id+"F12.wireOp",EDGE,"E95.top");var subQ2=makeQuery(id+"F12.imprint","INTERSECT",VERTEX,{"derivedFrom":[subQ1,subQ0]});Q6=makeQuery(id+"F12.imprint","IMPRINT",FACE,{"disambiguationData":[TD([[makeQuery(id+"F12.imprint","IMPRINT",EDGE,{"disambiguationData":[TD([[subQ2,-1.0]])],"derivedFrom":subQ1}),1.0]])]});}
            var Q7;
            {var subQ0=sQuery(id+"F12.wireOp",EDGE,"E96");var subQ1=sQuery(id+"F12.wireOp",EDGE,"E95.top");var subQ2=makeQuery(id+"F12.imprint","INTERSECT",VERTEX,{"derivedFrom":[subQ1,subQ0]});Q7=makeQuery(id+"F12.imprint","IMPRINT",FACE,{"disambiguationData":[TD([[makeQuery(id+"F12.imprint","IMPRINT",EDGE,{"disambiguationData":[TD([[subQ2,-1.0]])],"derivedFrom":subQ1}),1.0]])]});}
            var Q8;
            {var subQ0=sQuery(id+"F12.wireOp",EDGE,"E99");var subQ1=sQuery(id+"F12.wireOp",EDGE,"E95.right");var subQ2=makeQuery(id+"F12.imprint","INTERSECT",VERTEX,{"derivedFrom":[subQ1,subQ0]});Q8=makeQuery(id+"F12.imprint","IMPRINT",FACE,{"disambiguationData":[TD([[makeQuery(id+"F12.imprint","IMPRINT",EDGE,{"disambiguationData":[TD([[subQ2,-1.0]])],"derivedFrom":subQ1}),-1.0]])]});}
            var Q9;
            {var subQ0=sQuery(id+"F12.wireOp",EDGE,"E99");var subQ1=sQuery(id+"F12.wireOp",EDGE,"E95.left");var subQ2=makeQuery(id+"F12.imprint","INTERSECT",VERTEX,{"derivedFrom":[subQ1,subQ0]});Q9=makeQuery(id+"F12.imprint","IMPRINT",FACE,{"disambiguationData":[TD([[makeQuery(id+"F12.imprint","IMPRINT",EDGE,{"disambiguationData":[TD([[subQ2,-1.0]])],"derivedFrom":subQ1}),1.0]])]});}
            var Q10;
            {var subQ0=sQuery(id+"F12.wireOp",EDGE,"E95.left");var subQ1=sQuery(id+"F12.wireOp",EDGE,"E95.bottom");var subQ2=makeQuery(id+"F12.imprint","INTERSECT",VERTEX,{"derivedFrom":[subQ1,subQ0]});Q10=makeQuery(id+"F12.imprint","IMPRINT",FACE,{"disambiguationData":[TD([[makeQuery(id+"F12.imprint","IMPRINT",EDGE,{"disambiguationData":[TD([[subQ2,-1.0]])],"derivedFrom":subQ1}),-1.0]])]});}
            var Q11;
            {var subQ0=sQuery(id+"F12.wireOp",EDGE,"E96");var subQ1=sQuery(id+"F12.wireOp",EDGE,"E95.bottom");var subQ2=makeQuery(id+"F12.imprint","INTERSECT",VERTEX,{"derivedFrom":[subQ1,subQ0]});Q11=makeQuery(id+"F12.imprint","IMPRINT",FACE,{"disambiguationData":[TD([[makeQuery(id+"F12.imprint","IMPRINT",EDGE,{"disambiguationData":[TD([[subQ2,-1.0]])],"derivedFrom":subQ1}),-1.0]])]});}
            var Q12;
            {var subQ27=sQuery(id+"F12.wireOp",EDGE,"E121.left");Q12=makeQuery(id+"F12.imprint","IMPRINT",FACE,{"disambiguationData":[TD([[makeQuery(id+"F12.imprint","IMPRINT",EDGE,{"derivedFrom":subQ27}),1.0]])]});}
            var Q13;
            Q13=makeQuery(id+"F12.imprint","IMPRINT",FACE,{"disambiguationData":[TD([[makeQuery(id+"F12.imprint","IMPRINT",EDGE,{"derivedFrom":sQuery(id+"F12.wireOp",EDGE,"E94.bottom")}),-1.0]])]});
            var Q14;
            {var subQ2=sQuery(id+"F12.wireOp",EDGE,"E122");Q14=makeQuery(id+"F12.imprint","IMPRINT",FACE,{"disambiguationData":[TD([[makeQuery(id+"F12.imprint","IMPRINT",EDGE,{"derivedFrom":subQ2}),-1.0]])]});}
            var Q15;
            {var subQ9=sQuery(id+"F12.wireOp",EDGE,"E121.right");Q15=makeQuery(id+"F12.imprint","IMPRINT",FACE,{"disambiguationData":[TD([[makeQuery(id+"F12.imprint","IMPRINT",EDGE,{"derivedFrom":subQ9}),-1.0]])]});}
            var Q16;
            {var subQ0=sQuery(id+"F12.wireOp",EDGE,"E96");var subQ1=sQuery(id+"F12.wireOp",EDGE,"E95.bottom");var subQ2=makeQuery(id+"F12.imprint","INTERSECT",VERTEX,{"derivedFrom":[subQ1,subQ0]});Q16=makeQuery(id+"F12.imprint","IMPRINT",FACE,{"disambiguationData":[TD([[makeQuery(id+"F12.imprint","IMPRINT",EDGE,{"disambiguationData":[TD([[subQ2,1.0]])],"derivedFrom":subQ1}),-1.0]])]});}
            var Q17;
            {var subQ0=sQuery(id+"F12.wireOp",EDGE,"E99");var subQ1=sQuery(id+"F12.wireOp",EDGE,"E96");var subQ2=makeQuery(id+"F12.imprint","INTERSECT",VERTEX,{"derivedFrom":[subQ1,subQ0]});Q17=makeQuery(id+"F12.imprint","IMPRINT",FACE,{"disambiguationData":[TD([[makeQuery(id+"F12.imprint","IMPRINT",EDGE,{"disambiguationData":[TD([[subQ2,1.0]])],"derivedFrom":subQ1}),-1.0]])]});}
            var Q18;
            {var subQ0=sQuery(id+"F12.wireOp",EDGE,"E99");var subQ1=sQuery(id+"F12.wireOp",EDGE,"E95.right");var subQ2=makeQuery(id+"F12.imprint","INTERSECT",VERTEX,{"derivedFrom":[subQ1,subQ0]});Q18=makeQuery(id+"F12.imprint","IMPRINT",FACE,{"disambiguationData":[TD([[makeQuery(id+"F12.imprint","IMPRINT",EDGE,{"disambiguationData":[TD([[subQ2,1.0]])],"derivedFrom":subQ1}),-1.0]])]});}
            var Q19;
            {var subQ0=sQuery(id+"F12.wireOp",EDGE,"E99");var subQ1=sQuery(id+"F12.wireOp",EDGE,"E96");var subQ2=makeQuery(id+"F12.imprint","INTERSECT",VERTEX,{"derivedFrom":[subQ1,subQ0]});Q19=makeQuery(id+"F12.imprint","IMPRINT",FACE,{"disambiguationData":[TD([[makeQuery(id+"F12.imprint","IMPRINT",EDGE,{"disambiguationData":[TD([[subQ2,-1.0]])],"derivedFrom":subQ1}),-1.0]])]});}
            var Q20;
            {var subQ0=sQuery(id+"F12.wireOp",EDGE,"E99");var subQ1=sQuery(id+"F12.wireOp",EDGE,"E95.left");var subQ2=makeQuery(id+"F12.imprint","INTERSECT",VERTEX,{"derivedFrom":[subQ1,subQ0]});Q20=makeQuery(id+"F12.imprint","IMPRINT",FACE,{"disambiguationData":[TD([[makeQuery(id+"F12.imprint","IMPRINT",EDGE,{"disambiguationData":[TD([[subQ2,1.0]])],"derivedFrom":subQ1}),1.0]])]});}
            var Q21;
            {var subQ0=sQuery(id+"F12.wireOp",EDGE,"E109");var subQ1=sQuery(id+"F12.wireOp",EDGE,"E108.bottom");var subQ2=makeQuery(id+"F12.imprint","INTERSECT",VERTEX,{"derivedFrom":[subQ1,subQ0]});Q21=makeQuery(id+"F12.imprint","IMPRINT",FACE,{"disambiguationData":[TD([[makeQuery(id+"F12.imprint","IMPRINT",EDGE,{"disambiguationData":[TD([[subQ2,1.0]])],"derivedFrom":subQ1}),-1.0]])]});}
            var Q22;
            {var subQ0=sQuery(id+"F12.wireOp",EDGE,"E111");var subQ1=sQuery(id+"F12.wireOp",EDGE,"E109");var subQ2=makeQuery(id+"F12.imprint","INTERSECT",VERTEX,{"derivedFrom":[subQ1,subQ0]});Q22=makeQuery(id+"F12.imprint","IMPRINT",FACE,{"disambiguationData":[TD([[makeQuery(id+"F12.imprint","IMPRINT",EDGE,{"disambiguationData":[TD([[subQ2,-1.0]])],"derivedFrom":subQ1}),-1.0]])]});}
            var Q23;
            {var subQ0=sQuery(id+"F12.wireOp",EDGE,"E111");var subQ1=sQuery(id+"F12.wireOp",EDGE,"E108.right");var subQ2=makeQuery(id+"F12.imprint","INTERSECT",VERTEX,{"derivedFrom":[subQ1,subQ0]});Q23=makeQuery(id+"F12.imprint","IMPRINT",FACE,{"disambiguationData":[TD([[makeQuery(id+"F12.imprint","IMPRINT",EDGE,{"disambiguationData":[TD([[subQ2,-1.0]])],"derivedFrom":subQ1}),-1.0]])]});}
            var Q24;
            {var subQ0=sQuery(id+"F12.wireOp",EDGE,"E112");var subQ1=sQuery(id+"F12.wireOp",EDGE,"E108.left");var subQ2=makeQuery(id+"F12.imprint","INTERSECT",VERTEX,{"derivedFrom":[subQ1,subQ0]});Q24=makeQuery(id+"F12.imprint","IMPRINT",FACE,{"disambiguationData":[TD([[makeQuery(id+"F12.imprint","IMPRINT",EDGE,{"disambiguationData":[TD([[subQ2,1.0]])],"derivedFrom":subQ1}),1.0]])]});}
            var Q25;
            {var subQ0=sQuery(id+"F12.wireOp",EDGE,"E112");var subQ1=sQuery(id+"F12.wireOp",EDGE,"E109");var subQ2=makeQuery(id+"F12.imprint","INTERSECT",VERTEX,{"derivedFrom":[subQ1,subQ0]});Q25=makeQuery(id+"F12.imprint","IMPRINT",FACE,{"disambiguationData":[TD([[makeQuery(id+"F12.imprint","IMPRINT",EDGE,{"disambiguationData":[TD([[subQ2,-1.0]])],"derivedFrom":subQ1}),-1.0]])]});}
            var Q26;
            {var subQ0=sQuery(id+"F12.wireOp",EDGE,"E96");var subQ1=sQuery(id+"F12.wireOp",EDGE,"E95.top");var subQ2=makeQuery(id+"F12.imprint","INTERSECT",VERTEX,{"derivedFrom":[subQ1,subQ0]});Q26=makeQuery(id+"F12.imprint","IMPRINT",FACE,{"disambiguationData":[TD([[makeQuery(id+"F12.imprint","IMPRINT",EDGE,{"disambiguationData":[TD([[subQ2,1.0]])],"derivedFrom":subQ1}),1.0]])]});}
            var Q27;
            {var subQ0=sQuery(id+"F12.wireOp",EDGE,"E100");var subQ1=sQuery(id+"F12.wireOp",EDGE,"E96");var subQ2=makeQuery(id+"F12.imprint","INTERSECT",VERTEX,{"derivedFrom":[subQ1,subQ0]});Q27=makeQuery(id+"F12.imprint","IMPRINT",FACE,{"disambiguationData":[TD([[makeQuery(id+"F12.imprint","IMPRINT",EDGE,{"disambiguationData":[TD([[subQ2,-1.0]])],"derivedFrom":subQ1}),-1.0]])]});}
            var Q28;
            {var subQ0=sQuery(id+"F12.wireOp",EDGE,"E101");var subQ1=sQuery(id+"F12.wireOp",EDGE,"E95.right");var subQ2=makeQuery(id+"F12.imprint","INTERSECT",VERTEX,{"derivedFrom":[subQ1,subQ0]});Q28=makeQuery(id+"F12.imprint","IMPRINT",FACE,{"disambiguationData":[TD([[makeQuery(id+"F12.imprint","IMPRINT",EDGE,{"disambiguationData":[TD([[subQ2,1.0]])],"derivedFrom":subQ1}),-1.0]])]});}
            var Q29;
            {var subQ0=sQuery(id+"F12.wireOp",EDGE,"E101");var subQ1=sQuery(id+"F12.wireOp",EDGE,"E95.left");var subQ2=makeQuery(id+"F12.imprint","INTERSECT",VERTEX,{"derivedFrom":[subQ1,subQ0]});Q29=makeQuery(id+"F12.imprint","IMPRINT",FACE,{"disambiguationData":[TD([[makeQuery(id+"F12.imprint","IMPRINT",EDGE,{"disambiguationData":[TD([[subQ2,1.0]])],"derivedFrom":subQ1}),1.0]])]});}
            var Q30;
            {var subQ0=sQuery(id+"F12.wireOp",EDGE,"E109");var subQ1=sQuery(id+"F12.wireOp",EDGE,"E108.top");var subQ2=makeQuery(id+"F12.imprint","INTERSECT",VERTEX,{"derivedFrom":[subQ1,subQ0]});Q30=makeQuery(id+"F12.imprint","IMPRINT",FACE,{"disambiguationData":[TD([[makeQuery(id+"F12.imprint","IMPRINT",EDGE,{"disambiguationData":[TD([[subQ2,1.0]])],"derivedFrom":subQ1}),1.0]])]});}
            var Q31;
            {var subQ0=sQuery(id+"F12.wireOp",EDGE,"E114");var subQ1=sQuery(id+"F12.wireOp",EDGE,"E108.right");var subQ2=makeQuery(id+"F12.imprint","INTERSECT",VERTEX,{"derivedFrom":[subQ1,subQ0]});Q31=makeQuery(id+"F12.imprint","IMPRINT",FACE,{"disambiguationData":[TD([[makeQuery(id+"F12.imprint","IMPRINT",EDGE,{"disambiguationData":[TD([[subQ2,1.0]])],"derivedFrom":subQ1}),-1.0]])]});}
            var Q32;
            {var subQ0=sQuery(id+"F12.wireOp",EDGE,"E114");var subQ1=sQuery(id+"F12.wireOp",EDGE,"E109");var subQ2=makeQuery(id+"F12.imprint","INTERSECT",VERTEX,{"derivedFrom":[subQ1,subQ0]});Q32=makeQuery(id+"F12.imprint","IMPRINT",FACE,{"disambiguationData":[TD([[makeQuery(id+"F12.imprint","IMPRINT",EDGE,{"disambiguationData":[TD([[subQ2,1.0]])],"derivedFrom":subQ1}),-1.0]])]});}
            var Q33;
            {var subQ0=sQuery(id+"F12.wireOp",EDGE,"E114");var subQ1=sQuery(id+"F12.wireOp",EDGE,"E108.left");var subQ2=makeQuery(id+"F12.imprint","INTERSECT",VERTEX,{"derivedFrom":[subQ1,subQ0]});Q33=makeQuery(id+"F12.imprint","IMPRINT",FACE,{"disambiguationData":[TD([[makeQuery(id+"F12.imprint","IMPRINT",EDGE,{"disambiguationData":[TD([[subQ2,1.0]])],"derivedFrom":subQ1}),1.0]])]});}
            extrude(context, id + "F13", {"entities" : qUnion([Q0, Q1, Q2, Q3, Q4, Q5, Q6, Q7, Q8, Q9, Q10, Q11, Q12, Q13, Q14, Q15, Q16, Q17, Q18, Q19, Q20, Q21, Q22, Q23, Q24, Q25, Q26, Q27, Q28, Q29, Q30, Q31, Q32, Q33]), "operationType" : NewBodyOperationType.REMOVE, "oppositeDirection" : true, "depth" : 10.4 * mm});
        }
        {
            var Q0;
            Q0=makeQuery(id+"F12.imprint","IMPRINT",FACE,{"disambiguationData":[TD([[makeQuery(id+"F12.imprint","IMPRINT",EDGE,{"derivedFrom":sQuery(id+"F12.wireOp",EDGE,"E94.bottom")}),-1.0]])]});
            var Q1;
            {var subQ0=sQuery(id+"F12.wireOp",EDGE,"E111");var subQ1=sQuery(id+"F12.wireOp",EDGE,"E109");var subQ2=makeQuery(id+"F12.imprint","INTERSECT",VERTEX,{"derivedFrom":[subQ1,subQ0]});Q1=makeQuery(id+"F12.imprint","IMPRINT",FACE,{"disambiguationData":[TD([[makeQuery(id+"F12.imprint","IMPRINT",EDGE,{"disambiguationData":[TD([[subQ2,-1.0]])],"derivedFrom":subQ1}),-1.0]])]});}
            var Q2;
            {var subQ0=sQuery(id+"F12.wireOp",EDGE,"E109");var subQ1=sQuery(id+"F12.wireOp",EDGE,"E108.bottom");var subQ2=makeQuery(id+"F12.imprint","INTERSECT",VERTEX,{"derivedFrom":[subQ1,subQ0]});Q2=makeQuery(id+"F12.imprint","IMPRINT",FACE,{"disambiguationData":[TD([[makeQuery(id+"F12.imprint","IMPRINT",EDGE,{"disambiguationData":[TD([[subQ2,1.0]])],"derivedFrom":subQ1}),-1.0]])]});}
            var Q3;
            {var subQ0=sQuery(id+"F12.wireOp",EDGE,"E111");var subQ1=sQuery(id+"F12.wireOp",EDGE,"E108.right");var subQ2=makeQuery(id+"F12.imprint","INTERSECT",VERTEX,{"derivedFrom":[subQ1,subQ0]});Q3=makeQuery(id+"F12.imprint","IMPRINT",FACE,{"disambiguationData":[TD([[makeQuery(id+"F12.imprint","IMPRINT",EDGE,{"disambiguationData":[TD([[subQ2,-1.0]])],"derivedFrom":subQ1}),-1.0]])]});}
            var Q4;
            {var subQ0=sQuery(id+"F12.wireOp",EDGE,"E112");var subQ1=sQuery(id+"F12.wireOp",EDGE,"E108.left");var subQ2=makeQuery(id+"F12.imprint","INTERSECT",VERTEX,{"derivedFrom":[subQ1,subQ0]});Q4=makeQuery(id+"F12.imprint","IMPRINT",FACE,{"disambiguationData":[TD([[makeQuery(id+"F12.imprint","IMPRINT",EDGE,{"disambiguationData":[TD([[subQ2,1.0]])],"derivedFrom":subQ1}),1.0]])]});}
            var Q5;
            {var subQ0=sQuery(id+"F12.wireOp",EDGE,"E112");var subQ1=sQuery(id+"F12.wireOp",EDGE,"E109");var subQ2=makeQuery(id+"F12.imprint","INTERSECT",VERTEX,{"derivedFrom":[subQ1,subQ0]});Q5=makeQuery(id+"F12.imprint","IMPRINT",FACE,{"disambiguationData":[TD([[makeQuery(id+"F12.imprint","IMPRINT",EDGE,{"disambiguationData":[TD([[subQ2,-1.0]])],"derivedFrom":subQ1}),-1.0]])]});}
            var Q6;
            {var subQ0=sQuery(id+"F12.wireOp",EDGE,"E99");var subQ1=sQuery(id+"F12.wireOp",EDGE,"E95.left");var subQ2=makeQuery(id+"F12.imprint","INTERSECT",VERTEX,{"derivedFrom":[subQ1,subQ0]});Q6=makeQuery(id+"F12.imprint","IMPRINT",FACE,{"disambiguationData":[TD([[makeQuery(id+"F12.imprint","IMPRINT",EDGE,{"disambiguationData":[TD([[subQ2,1.0]])],"derivedFrom":subQ1}),1.0]])]});}
            var Q7;
            {var subQ0=sQuery(id+"F12.wireOp",EDGE,"E96");var subQ1=sQuery(id+"F12.wireOp",EDGE,"E95.bottom");var subQ2=makeQuery(id+"F12.imprint","INTERSECT",VERTEX,{"derivedFrom":[subQ1,subQ0]});Q7=makeQuery(id+"F12.imprint","IMPRINT",FACE,{"disambiguationData":[TD([[makeQuery(id+"F12.imprint","IMPRINT",EDGE,{"disambiguationData":[TD([[subQ2,1.0]])],"derivedFrom":subQ1}),-1.0]])]});}
            var Q8;
            {var subQ0=sQuery(id+"F12.wireOp",EDGE,"E99");var subQ1=sQuery(id+"F12.wireOp",EDGE,"E95.right");var subQ2=makeQuery(id+"F12.imprint","INTERSECT",VERTEX,{"derivedFrom":[subQ1,subQ0]});Q8=makeQuery(id+"F12.imprint","IMPRINT",FACE,{"disambiguationData":[TD([[makeQuery(id+"F12.imprint","IMPRINT",EDGE,{"disambiguationData":[TD([[subQ2,1.0]])],"derivedFrom":subQ1}),-1.0]])]});}
            var Q9;
            {var subQ0=sQuery(id+"F12.wireOp",EDGE,"E99");var subQ1=sQuery(id+"F12.wireOp",EDGE,"E96");var subQ2=makeQuery(id+"F12.imprint","INTERSECT",VERTEX,{"derivedFrom":[subQ1,subQ0]});Q9=makeQuery(id+"F12.imprint","IMPRINT",FACE,{"disambiguationData":[TD([[makeQuery(id+"F12.imprint","IMPRINT",EDGE,{"disambiguationData":[TD([[subQ2,-1.0]])],"derivedFrom":subQ1}),-1.0]])]});}
            var Q10;
            {var subQ0=sQuery(id+"F12.wireOp",EDGE,"E99");var subQ1=sQuery(id+"F12.wireOp",EDGE,"E96");var subQ2=makeQuery(id+"F12.imprint","INTERSECT",VERTEX,{"derivedFrom":[subQ1,subQ0]});Q10=makeQuery(id+"F12.imprint","IMPRINT",FACE,{"disambiguationData":[TD([[makeQuery(id+"F12.imprint","IMPRINT",EDGE,{"disambiguationData":[TD([[subQ2,1.0]])],"derivedFrom":subQ1}),-1.0]])]});}
            var Q11;
            {var subQ0=sQuery(id+"F12.wireOp",EDGE,"E114");var subQ1=sQuery(id+"F12.wireOp",EDGE,"E108.left");var subQ2=makeQuery(id+"F12.imprint","INTERSECT",VERTEX,{"derivedFrom":[subQ1,subQ0]});Q11=makeQuery(id+"F12.imprint","IMPRINT",FACE,{"disambiguationData":[TD([[makeQuery(id+"F12.imprint","IMPRINT",EDGE,{"disambiguationData":[TD([[subQ2,1.0]])],"derivedFrom":subQ1}),1.0]])]});}
            var Q12;
            {var subQ0=sQuery(id+"F12.wireOp",EDGE,"E114");var subQ1=sQuery(id+"F12.wireOp",EDGE,"E109");var subQ2=makeQuery(id+"F12.imprint","INTERSECT",VERTEX,{"derivedFrom":[subQ1,subQ0]});Q12=makeQuery(id+"F12.imprint","IMPRINT",FACE,{"disambiguationData":[TD([[makeQuery(id+"F12.imprint","IMPRINT",EDGE,{"disambiguationData":[TD([[subQ2,1.0]])],"derivedFrom":subQ1}),-1.0]])]});}
            var Q13;
            {var subQ0=sQuery(id+"F12.wireOp",EDGE,"E114");var subQ1=sQuery(id+"F12.wireOp",EDGE,"E108.right");var subQ2=makeQuery(id+"F12.imprint","INTERSECT",VERTEX,{"derivedFrom":[subQ1,subQ0]});Q13=makeQuery(id+"F12.imprint","IMPRINT",FACE,{"disambiguationData":[TD([[makeQuery(id+"F12.imprint","IMPRINT",EDGE,{"disambiguationData":[TD([[subQ2,1.0]])],"derivedFrom":subQ1}),-1.0]])]});}
            var Q14;
            {var subQ0=sQuery(id+"F12.wireOp",EDGE,"E109");var subQ1=sQuery(id+"F12.wireOp",EDGE,"E108.top");var subQ2=makeQuery(id+"F12.imprint","INTERSECT",VERTEX,{"derivedFrom":[subQ1,subQ0]});Q14=makeQuery(id+"F12.imprint","IMPRINT",FACE,{"disambiguationData":[TD([[makeQuery(id+"F12.imprint","IMPRINT",EDGE,{"disambiguationData":[TD([[subQ2,1.0]])],"derivedFrom":subQ1}),1.0]])]});}
            var Q15;
            {var subQ0=sQuery(id+"F12.wireOp",EDGE,"E101");var subQ1=sQuery(id+"F12.wireOp",EDGE,"E95.left");var subQ2=makeQuery(id+"F12.imprint","INTERSECT",VERTEX,{"derivedFrom":[subQ1,subQ0]});Q15=makeQuery(id+"F12.imprint","IMPRINT",FACE,{"disambiguationData":[TD([[makeQuery(id+"F12.imprint","IMPRINT",EDGE,{"disambiguationData":[TD([[subQ2,1.0]])],"derivedFrom":subQ1}),1.0]])]});}
            var Q16;
            {var subQ0=sQuery(id+"F12.wireOp",EDGE,"E100");var subQ1=sQuery(id+"F12.wireOp",EDGE,"E96");var subQ2=makeQuery(id+"F12.imprint","INTERSECT",VERTEX,{"derivedFrom":[subQ1,subQ0]});Q16=makeQuery(id+"F12.imprint","IMPRINT",FACE,{"disambiguationData":[TD([[makeQuery(id+"F12.imprint","IMPRINT",EDGE,{"disambiguationData":[TD([[subQ2,-1.0]])],"derivedFrom":subQ1}),-1.0]])]});}
            var Q17;
            {var subQ0=sQuery(id+"F12.wireOp",EDGE,"E101");var subQ1=sQuery(id+"F12.wireOp",EDGE,"E95.right");var subQ2=makeQuery(id+"F12.imprint","INTERSECT",VERTEX,{"derivedFrom":[subQ1,subQ0]});Q17=makeQuery(id+"F12.imprint","IMPRINT",FACE,{"disambiguationData":[TD([[makeQuery(id+"F12.imprint","IMPRINT",EDGE,{"disambiguationData":[TD([[subQ2,1.0]])],"derivedFrom":subQ1}),-1.0]])]});}
            var Q18;
            {var subQ0=sQuery(id+"F12.wireOp",EDGE,"E96");var subQ1=sQuery(id+"F12.wireOp",EDGE,"E95.top");var subQ2=makeQuery(id+"F12.imprint","INTERSECT",VERTEX,{"derivedFrom":[subQ1,subQ0]});Q18=makeQuery(id+"F12.imprint","IMPRINT",FACE,{"disambiguationData":[TD([[makeQuery(id+"F12.imprint","IMPRINT",EDGE,{"disambiguationData":[TD([[subQ2,1.0]])],"derivedFrom":subQ1}),1.0]])]});}
            var Q19;
            {var subQ27=sQuery(id+"F12.wireOp",EDGE,"E121.left");Q19=makeQuery(id+"F12.imprint","IMPRINT",FACE,{"disambiguationData":[TD([[makeQuery(id+"F12.imprint","IMPRINT",EDGE,{"derivedFrom":subQ27}),1.0]])]});}
            var Q20;
            {var subQ9=sQuery(id+"F12.wireOp",EDGE,"E121.right");Q20=makeQuery(id+"F12.imprint","IMPRINT",FACE,{"disambiguationData":[TD([[makeQuery(id+"F12.imprint","IMPRINT",EDGE,{"derivedFrom":subQ9}),-1.0]])]});}
            var Q21;
            {var subQ2=sQuery(id+"F12.wireOp",EDGE,"E122");Q21=makeQuery(id+"F12.imprint","IMPRINT",FACE,{"disambiguationData":[TD([[makeQuery(id+"F12.imprint","IMPRINT",EDGE,{"derivedFrom":subQ2}),-1.0]])]});}
            extrude(context, id + "F14", {"entities" : qUnion([Q0, Q1, Q2, Q3, Q4, Q5, Q6, Q7, Q8, Q9, Q10, Q11, Q12, Q13, Q14, Q15, Q16, Q17, Q18, Q19, Q20, Q21]), "operationType" : NewBodyOperationType.ADD, "oppositeDirection" : true, "depth" : 2.54 * mm, "hasSecondDirection" : true, "secondDirectionOppositeDirection" : true, "secondDirectionDepth" : 1.27 * mm});
        }
        {
            var Q0;
            Q0=makeQuery(id+"F1.opExtrude","SWEPT_FACE",FACE,{"disambiguationData":[OSD([sQuery(id+"F0.wireOp",EDGE,"E7")])]});
            var sketch = newSketch(context, id + "F15", { "sketchPlane" : qUnion([Q0])});
            skLineSegment(sketch, "E124.bottom", {"start": v(27.18, 57.15) * mm, "end": v(57.15, 57.15) * mm});
            skLineSegment(sketch, "E124.top", {"start": v(27.18, 23.62) * mm, "end": v(57.15, 23.62) * mm});
            skLineSegment(sketch, "E124.left", {"start": v(27.18, 57.15) * mm, "end": v(27.18, 23.62) * mm});
            skLineSegment(sketch, "E124.right", {"start": v(57.15, 57.15) * mm, "end": v(57.15, 23.62) * mm});
            skLineSegment(sketch, "E125.bottom", {"start": v(44.36, 55.12) * mm, "end": v(55.12, 55.12) * mm});
            skLineSegment(sketch, "E125.top", {"start": v(44.36, 25.65) * mm, "end": v(55.12, 25.65) * mm});
            skLineSegment(sketch, "E125.left", {"start": v(44.36, 55.12) * mm, "end": v(44.36, 25.65) * mm});
            skLineSegment(sketch, "E125.right", {"start": v(55.12, 55.12) * mm, "end": v(55.12, 25.65) * mm});
            skLineSegment(sketch, "E126", {"start": v(50.07, 55.12) * mm, "end": v(50.07, 25.65) * mm});
            skLineSegment(sketch, "E127", {"start": v(49.44, 55.12) * mm, "end": v(49.44, 25.65) * mm});
            skLineSegment(sketch, "E128", {"start": v(44.36, 45.72) * mm, "end": v(55.12, 45.72) * mm});
            skLineSegment(sketch, "E129", {"start": v(44.36, 45.09) * mm, "end": v(55.12, 45.09) * mm});
            skLineSegment(sketch, "E130", {"start": v(44.36, 35.69) * mm, "end": v(55.12, 35.69) * mm});
            skLineSegment(sketch, "E131", {"start": v(44.36, 35.05) * mm, "end": v(55.12, 35.05) * mm});
            skLineSegment(sketch, "E132", {"start": v(49.44, 55.12) * mm, "end": v(49.44, 45.09) * mm});
            skLineSegment(sketch, "E133", {"start": v(49.44, 55.12) * mm, "end": v(49.44, 45.72) * mm});
            skLineSegment(sketch, "E134", {"start": v(49.44, 45.72) * mm, "end": v(49.44, 45.09) * mm});
            skLineSegment(sketch, "E135", {"start": v(49.44, 45.09) * mm, "end": v(49.44, 35.69) * mm});
            skLineSegment(sketch, "E136", {"start": v(49.44, 35.69) * mm, "end": v(49.44, 35.05) * mm});
            skLineSegment(sketch, "E137", {"start": v(49.44, 35.05) * mm, "end": v(49.44, 25.65) * mm});
            skLineSegment(sketch, "E138.bottom", {"start": v(29.21, 55.12) * mm, "end": v(39.97, 55.12) * mm});
            skLineSegment(sketch, "E138.top", {"start": v(29.21, 25.65) * mm, "end": v(39.97, 25.65) * mm});
            skLineSegment(sketch, "E138.left", {"start": v(29.21, 55.12) * mm, "end": v(29.21, 25.65) * mm});
            skLineSegment(sketch, "E138.right", {"start": v(39.97, 55.12) * mm, "end": v(39.97, 25.65) * mm});
            skLineSegment(sketch, "E139", {"start": v(34.9, 55.12) * mm, "end": v(34.9, 25.65) * mm});
            skLineSegment(sketch, "E140", {"start": v(34.27, 55.12) * mm, "end": v(34.27, 25.65) * mm});
            skLineSegment(sketch, "E141", {"start": v(29.21, 45.72) * mm, "end": v(39.97, 45.72) * mm});
            skLineSegment(sketch, "E142", {"start": v(29.21, 45.09) * mm, "end": v(39.97, 45.09) * mm});
            skLineSegment(sketch, "E143", {"start": v(29.21, 35.69) * mm, "end": v(39.97, 35.69) * mm});
            skLineSegment(sketch, "E144", {"start": v(29.21, 35.05) * mm, "end": v(39.97, 35.05) * mm});
            skLineSegment(sketch, "E145", {"start": v(34.27, 55.12) * mm, "end": v(34.27, 45.09) * mm});
            skLineSegment(sketch, "E146", {"start": v(34.27, 55.12) * mm, "end": v(34.27, 45.72) * mm});
            skLineSegment(sketch, "E147", {"start": v(34.27, 45.72) * mm, "end": v(34.27, 45.09) * mm});
            skLineSegment(sketch, "E148", {"start": v(34.27, 45.09) * mm, "end": v(34.27, 35.69) * mm});
            skLineSegment(sketch, "E149", {"start": v(34.27, 35.69) * mm, "end": v(34.27, 35.05) * mm});
            skLineSegment(sketch, "E150", {"start": v(34.27, 35.05) * mm, "end": v(34.27, 25.65) * mm});
            skLineSegment(sketch, "E151.bottom", {"start": v(27.94, 56.39) * mm, "end": v(56.39, 56.39) * mm});
            skLineSegment(sketch, "E151.top", {"start": v(27.94, 24.38) * mm, "end": v(56.39, 24.38) * mm});
            skLineSegment(sketch, "E151.left", {"start": v(27.94, 56.39) * mm, "end": v(27.94, 24.38) * mm});
            skLineSegment(sketch, "E151.right", {"start": v(56.39, 56.39) * mm, "end": v(56.39, 24.38) * mm});
            skLineSegment(sketch, "E152", {"start": v(41.78, 24.38) * mm, "end": v(41.78, 56.39) * mm});
            skLineSegment(sketch, "E153", {"start": v(42.55, 56.39) * mm, "end": v(42.55, 24.38) * mm});
            skLineSegment(sketch, "E154", {"start": v(162.56, 0) * mm, "end": v(162.56, 57.15) * mm});
            skLineSegment(sketch, "E155", {"start": v(162.56, 57.15) * mm, "end": v(139.7, 57.15) * mm});
            skLineSegment(sketch, "E156", {"start": v(139.7, 57.15) * mm, "end": v(139.7, 0) * mm});
            skSolve(sketch);
        }
        {
            var Q0;
            {var subQ0=sQuery(id+"F15.wireOp",EDGE,"E138.left");var subQ1=sQuery(id+"F15.wireOp",EDGE,"E138.bottom");var subQ2=makeQuery(id+"F15.imprint","INTERSECT",VERTEX,{"derivedFrom":[subQ1,subQ0]});Q0=makeQuery(id+"F15.imprint","IMPRINT",FACE,{"disambiguationData":[TD([[makeQuery(id+"F15.imprint","IMPRINT",EDGE,{"disambiguationData":[TD([[subQ2,-1.0]])],"derivedFrom":subQ1}),-1.0]])]});}
            var Q1;
            {var subQ0=sQuery(id+"F15.wireOp",EDGE,"E139");var subQ1=sQuery(id+"F15.wireOp",EDGE,"E138.bottom");var subQ2=makeQuery(id+"F15.imprint","INTERSECT",VERTEX,{"derivedFrom":[subQ1,subQ0]});Q1=makeQuery(id+"F15.imprint","IMPRINT",FACE,{"disambiguationData":[TD([[makeQuery(id+"F15.imprint","IMPRINT",EDGE,{"disambiguationData":[TD([[subQ2,-1.0]])],"derivedFrom":subQ1}),-1.0]])]});}
            var Q2;
            {var subQ0=sQuery(id+"F15.wireOp",EDGE,"E125.left");var subQ1=sQuery(id+"F15.wireOp",EDGE,"E125.bottom");var subQ2=makeQuery(id+"F15.imprint","INTERSECT",VERTEX,{"derivedFrom":[subQ1,subQ0]});Q2=makeQuery(id+"F15.imprint","IMPRINT",FACE,{"disambiguationData":[TD([[makeQuery(id+"F15.imprint","IMPRINT",EDGE,{"disambiguationData":[TD([[subQ2,-1.0]])],"derivedFrom":subQ1}),-1.0]])]});}
            var Q3;
            {var subQ0=sQuery(id+"F15.wireOp",EDGE,"E126");var subQ1=sQuery(id+"F15.wireOp",EDGE,"E125.bottom");var subQ2=makeQuery(id+"F15.imprint","INTERSECT",VERTEX,{"derivedFrom":[subQ1,subQ0]});Q3=makeQuery(id+"F15.imprint","IMPRINT",FACE,{"disambiguationData":[TD([[makeQuery(id+"F15.imprint","IMPRINT",EDGE,{"disambiguationData":[TD([[subQ2,-1.0]])],"derivedFrom":subQ1}),-1.0]])]});}
            var Q4;
            {var subQ0=sQuery(id+"F15.wireOp",EDGE,"E129");var subQ1=sQuery(id+"F15.wireOp",EDGE,"E125.right");var subQ2=makeQuery(id+"F15.imprint","INTERSECT",VERTEX,{"derivedFrom":[subQ1,subQ0]});Q4=makeQuery(id+"F15.imprint","IMPRINT",FACE,{"disambiguationData":[TD([[makeQuery(id+"F15.imprint","IMPRINT",EDGE,{"disambiguationData":[TD([[subQ2,-1.0]])],"derivedFrom":subQ1}),-1.0]])]});}
            var Q5;
            {var subQ0=sQuery(id+"F15.wireOp",EDGE,"E129");var subQ1=sQuery(id+"F15.wireOp",EDGE,"E125.left");var subQ2=makeQuery(id+"F15.imprint","INTERSECT",VERTEX,{"derivedFrom":[subQ1,subQ0]});Q5=makeQuery(id+"F15.imprint","IMPRINT",FACE,{"disambiguationData":[TD([[makeQuery(id+"F15.imprint","IMPRINT",EDGE,{"disambiguationData":[TD([[subQ2,-1.0]])],"derivedFrom":subQ1}),1.0]])]});}
            var Q6;
            {var subQ0=sQuery(id+"F15.wireOp",EDGE,"E142");var subQ1=sQuery(id+"F15.wireOp",EDGE,"E138.right");var subQ2=makeQuery(id+"F15.imprint","INTERSECT",VERTEX,{"derivedFrom":[subQ1,subQ0]});Q6=makeQuery(id+"F15.imprint","IMPRINT",FACE,{"disambiguationData":[TD([[makeQuery(id+"F15.imprint","IMPRINT",EDGE,{"disambiguationData":[TD([[subQ2,-1.0]])],"derivedFrom":subQ1}),-1.0]])]});}
            var Q7;
            {var subQ0=sQuery(id+"F15.wireOp",EDGE,"E142");var subQ1=sQuery(id+"F15.wireOp",EDGE,"E138.left");var subQ2=makeQuery(id+"F15.imprint","INTERSECT",VERTEX,{"derivedFrom":[subQ1,subQ0]});Q7=makeQuery(id+"F15.imprint","IMPRINT",FACE,{"disambiguationData":[TD([[makeQuery(id+"F15.imprint","IMPRINT",EDGE,{"disambiguationData":[TD([[subQ2,-1.0]])],"derivedFrom":subQ1}),1.0]])]});}
            var Q8;
            {var subQ0=sQuery(id+"F15.wireOp",EDGE,"E138.left");var subQ1=sQuery(id+"F15.wireOp",EDGE,"E138.top");var subQ2=makeQuery(id+"F15.imprint","INTERSECT",VERTEX,{"derivedFrom":[subQ1,subQ0]});Q8=makeQuery(id+"F15.imprint","IMPRINT",FACE,{"disambiguationData":[TD([[makeQuery(id+"F15.imprint","IMPRINT",EDGE,{"disambiguationData":[TD([[subQ2,-1.0]])],"derivedFrom":subQ1}),1.0]])]});}
            var Q9;
            {var subQ0=sQuery(id+"F15.wireOp",EDGE,"E139");var subQ1=sQuery(id+"F15.wireOp",EDGE,"E138.top");var subQ2=makeQuery(id+"F15.imprint","INTERSECT",VERTEX,{"derivedFrom":[subQ1,subQ0]});Q9=makeQuery(id+"F15.imprint","IMPRINT",FACE,{"disambiguationData":[TD([[makeQuery(id+"F15.imprint","IMPRINT",EDGE,{"disambiguationData":[TD([[subQ2,-1.0]])],"derivedFrom":subQ1}),1.0]])]});}
            var Q10;
            {var subQ0=sQuery(id+"F15.wireOp",EDGE,"E125.left");var subQ1=sQuery(id+"F15.wireOp",EDGE,"E125.top");var subQ2=makeQuery(id+"F15.imprint","INTERSECT",VERTEX,{"derivedFrom":[subQ1,subQ0]});Q10=makeQuery(id+"F15.imprint","IMPRINT",FACE,{"disambiguationData":[TD([[makeQuery(id+"F15.imprint","IMPRINT",EDGE,{"disambiguationData":[TD([[subQ2,-1.0]])],"derivedFrom":subQ1}),1.0]])]});}
            var Q11;
            {var subQ0=sQuery(id+"F15.wireOp",EDGE,"E126");var subQ1=sQuery(id+"F15.wireOp",EDGE,"E125.top");var subQ2=makeQuery(id+"F15.imprint","INTERSECT",VERTEX,{"derivedFrom":[subQ1,subQ0]});Q11=makeQuery(id+"F15.imprint","IMPRINT",FACE,{"disambiguationData":[TD([[makeQuery(id+"F15.imprint","IMPRINT",EDGE,{"disambiguationData":[TD([[subQ2,-1.0]])],"derivedFrom":subQ1}),1.0]])]});}
            var Q12;
            {var subQ27=sQuery(id+"F15.wireOp",EDGE,"E151.left");Q12=makeQuery(id+"F15.imprint","IMPRINT",FACE,{"disambiguationData":[TD([[makeQuery(id+"F15.imprint","IMPRINT",EDGE,{"derivedFrom":subQ27}),1.0]])]});}
            var Q13;
            {var subQ2=sQuery(id+"F15.wireOp",EDGE,"E152");Q13=makeQuery(id+"F15.imprint","IMPRINT",FACE,{"disambiguationData":[TD([[makeQuery(id+"F15.imprint","IMPRINT",EDGE,{"derivedFrom":subQ2}),-1.0]])]});}
            var Q14;
            {var subQ9=sQuery(id+"F15.wireOp",EDGE,"E151.right");Q14=makeQuery(id+"F15.imprint","IMPRINT",FACE,{"disambiguationData":[TD([[makeQuery(id+"F15.imprint","IMPRINT",EDGE,{"derivedFrom":subQ9}),-1.0]])]});}
            var Q15;
            Q15=makeQuery(id+"F15.imprint","IMPRINT",FACE,{"disambiguationData":[TD([[makeQuery(id+"F15.imprint","IMPRINT",EDGE,{"derivedFrom":sQuery(id+"F15.wireOp",EDGE,"E124.bottom")}),-1.0]])]});
            var Q16;
            {var subQ0=sQuery(id+"F15.wireOp",EDGE,"E139");var subQ1=sQuery(id+"F15.wireOp",EDGE,"E138.bottom");var subQ2=makeQuery(id+"F15.imprint","INTERSECT",VERTEX,{"derivedFrom":[subQ1,subQ0]});Q16=makeQuery(id+"F15.imprint","IMPRINT",FACE,{"disambiguationData":[TD([[makeQuery(id+"F15.imprint","IMPRINT",EDGE,{"disambiguationData":[TD([[subQ2,1.0]])],"derivedFrom":subQ1}),-1.0]])]});}
            var Q17;
            {var subQ0=sQuery(id+"F15.wireOp",EDGE,"E142");var subQ1=sQuery(id+"F15.wireOp",EDGE,"E139");var subQ2=makeQuery(id+"F15.imprint","INTERSECT",VERTEX,{"derivedFrom":[subQ1,subQ0]});Q17=makeQuery(id+"F15.imprint","IMPRINT",FACE,{"disambiguationData":[TD([[makeQuery(id+"F15.imprint","IMPRINT",EDGE,{"disambiguationData":[TD([[subQ2,1.0]])],"derivedFrom":subQ1}),-1.0]])]});}
            var Q18;
            {var subQ0=sQuery(id+"F15.wireOp",EDGE,"E142");var subQ1=sQuery(id+"F15.wireOp",EDGE,"E138.left");var subQ2=makeQuery(id+"F15.imprint","INTERSECT",VERTEX,{"derivedFrom":[subQ1,subQ0]});Q18=makeQuery(id+"F15.imprint","IMPRINT",FACE,{"disambiguationData":[TD([[makeQuery(id+"F15.imprint","IMPRINT",EDGE,{"disambiguationData":[TD([[subQ2,1.0]])],"derivedFrom":subQ1}),1.0]])]});}
            var Q19;
            {var subQ0=sQuery(id+"F15.wireOp",EDGE,"E142");var subQ1=sQuery(id+"F15.wireOp",EDGE,"E138.right");var subQ2=makeQuery(id+"F15.imprint","INTERSECT",VERTEX,{"derivedFrom":[subQ1,subQ0]});Q19=makeQuery(id+"F15.imprint","IMPRINT",FACE,{"disambiguationData":[TD([[makeQuery(id+"F15.imprint","IMPRINT",EDGE,{"disambiguationData":[TD([[subQ2,1.0]])],"derivedFrom":subQ1}),-1.0]])]});}
            var Q20;
            {var subQ0=sQuery(id+"F15.wireOp",EDGE,"E142");var subQ1=sQuery(id+"F15.wireOp",EDGE,"E139");var subQ2=makeQuery(id+"F15.imprint","INTERSECT",VERTEX,{"derivedFrom":[subQ1,subQ0]});Q20=makeQuery(id+"F15.imprint","IMPRINT",FACE,{"disambiguationData":[TD([[makeQuery(id+"F15.imprint","IMPRINT",EDGE,{"disambiguationData":[TD([[subQ2,-1.0]])],"derivedFrom":subQ1}),-1.0]])]});}
            var Q21;
            {var subQ0=sQuery(id+"F15.wireOp",EDGE,"E143");var subQ1=sQuery(id+"F15.wireOp",EDGE,"E138.right");var subQ2=makeQuery(id+"F15.imprint","INTERSECT",VERTEX,{"derivedFrom":[subQ1,subQ0]});Q21=makeQuery(id+"F15.imprint","IMPRINT",FACE,{"disambiguationData":[TD([[makeQuery(id+"F15.imprint","IMPRINT",EDGE,{"disambiguationData":[TD([[subQ2,-1.0]])],"derivedFrom":subQ1}),-1.0]])]});}
            var Q22;
            {var subQ0=sQuery(id+"F15.wireOp",EDGE,"E143");var subQ1=sQuery(id+"F15.wireOp",EDGE,"E138.left");var subQ2=makeQuery(id+"F15.imprint","INTERSECT",VERTEX,{"derivedFrom":[subQ1,subQ0]});Q22=makeQuery(id+"F15.imprint","IMPRINT",FACE,{"disambiguationData":[TD([[makeQuery(id+"F15.imprint","IMPRINT",EDGE,{"disambiguationData":[TD([[subQ2,-1.0]])],"derivedFrom":subQ1}),1.0]])]});}
            var Q23;
            {var subQ0=sQuery(id+"F15.wireOp",EDGE,"E144");var subQ1=sQuery(id+"F15.wireOp",EDGE,"E139");var subQ2=makeQuery(id+"F15.imprint","INTERSECT",VERTEX,{"derivedFrom":[subQ1,subQ0]});Q23=makeQuery(id+"F15.imprint","IMPRINT",FACE,{"disambiguationData":[TD([[makeQuery(id+"F15.imprint","IMPRINT",EDGE,{"disambiguationData":[TD([[subQ2,1.0]])],"derivedFrom":subQ1}),-1.0]])]});}
            var Q24;
            {var subQ0=sQuery(id+"F15.wireOp",EDGE,"E139");var subQ1=sQuery(id+"F15.wireOp",EDGE,"E138.top");var subQ2=makeQuery(id+"F15.imprint","INTERSECT",VERTEX,{"derivedFrom":[subQ1,subQ0]});Q24=makeQuery(id+"F15.imprint","IMPRINT",FACE,{"disambiguationData":[TD([[makeQuery(id+"F15.imprint","IMPRINT",EDGE,{"disambiguationData":[TD([[subQ2,1.0]])],"derivedFrom":subQ1}),1.0]])]});}
            var Q25;
            {var subQ0=sQuery(id+"F15.wireOp",EDGE,"E126");var subQ1=sQuery(id+"F15.wireOp",EDGE,"E125.bottom");var subQ2=makeQuery(id+"F15.imprint","INTERSECT",VERTEX,{"derivedFrom":[subQ1,subQ0]});Q25=makeQuery(id+"F15.imprint","IMPRINT",FACE,{"disambiguationData":[TD([[makeQuery(id+"F15.imprint","IMPRINT",EDGE,{"disambiguationData":[TD([[subQ2,1.0]])],"derivedFrom":subQ1}),-1.0]])]});}
            var Q26;
            {var subQ0=sQuery(id+"F15.wireOp",EDGE,"E129");var subQ1=sQuery(id+"F15.wireOp",EDGE,"E125.right");var subQ2=makeQuery(id+"F15.imprint","INTERSECT",VERTEX,{"derivedFrom":[subQ1,subQ0]});Q26=makeQuery(id+"F15.imprint","IMPRINT",FACE,{"disambiguationData":[TD([[makeQuery(id+"F15.imprint","IMPRINT",EDGE,{"disambiguationData":[TD([[subQ2,1.0]])],"derivedFrom":subQ1}),-1.0]])]});}
            var Q27;
            {var subQ0=sQuery(id+"F15.wireOp",EDGE,"E129");var subQ1=sQuery(id+"F15.wireOp",EDGE,"E126");var subQ2=makeQuery(id+"F15.imprint","INTERSECT",VERTEX,{"derivedFrom":[subQ1,subQ0]});Q27=makeQuery(id+"F15.imprint","IMPRINT",FACE,{"disambiguationData":[TD([[makeQuery(id+"F15.imprint","IMPRINT",EDGE,{"disambiguationData":[TD([[subQ2,1.0]])],"derivedFrom":subQ1}),-1.0]])]});}
            var Q28;
            {var subQ0=sQuery(id+"F15.wireOp",EDGE,"E129");var subQ1=sQuery(id+"F15.wireOp",EDGE,"E125.left");var subQ2=makeQuery(id+"F15.imprint","INTERSECT",VERTEX,{"derivedFrom":[subQ1,subQ0]});Q28=makeQuery(id+"F15.imprint","IMPRINT",FACE,{"disambiguationData":[TD([[makeQuery(id+"F15.imprint","IMPRINT",EDGE,{"disambiguationData":[TD([[subQ2,1.0]])],"derivedFrom":subQ1}),1.0]])]});}
            var Q29;
            {var subQ0=sQuery(id+"F15.wireOp",EDGE,"E129");var subQ1=sQuery(id+"F15.wireOp",EDGE,"E126");var subQ2=makeQuery(id+"F15.imprint","INTERSECT",VERTEX,{"derivedFrom":[subQ1,subQ0]});Q29=makeQuery(id+"F15.imprint","IMPRINT",FACE,{"disambiguationData":[TD([[makeQuery(id+"F15.imprint","IMPRINT",EDGE,{"disambiguationData":[TD([[subQ2,-1.0]])],"derivedFrom":subQ1}),-1.0]])]});}
            var Q30;
            {var subQ0=sQuery(id+"F15.wireOp",EDGE,"E131");var subQ1=sQuery(id+"F15.wireOp",EDGE,"E125.right");var subQ2=makeQuery(id+"F15.imprint","INTERSECT",VERTEX,{"derivedFrom":[subQ1,subQ0]});Q30=makeQuery(id+"F15.imprint","IMPRINT",FACE,{"disambiguationData":[TD([[makeQuery(id+"F15.imprint","IMPRINT",EDGE,{"disambiguationData":[TD([[subQ2,1.0]])],"derivedFrom":subQ1}),-1.0]])]});}
            var Q31;
            {var subQ0=sQuery(id+"F15.wireOp",EDGE,"E130");var subQ1=sQuery(id+"F15.wireOp",EDGE,"E126");var subQ2=makeQuery(id+"F15.imprint","INTERSECT",VERTEX,{"derivedFrom":[subQ1,subQ0]});Q31=makeQuery(id+"F15.imprint","IMPRINT",FACE,{"disambiguationData":[TD([[makeQuery(id+"F15.imprint","IMPRINT",EDGE,{"disambiguationData":[TD([[subQ2,-1.0]])],"derivedFrom":subQ1}),-1.0]])]});}
            var Q32;
            {var subQ0=sQuery(id+"F15.wireOp",EDGE,"E130");var subQ1=sQuery(id+"F15.wireOp",EDGE,"E125.left");var subQ2=makeQuery(id+"F15.imprint","INTERSECT",VERTEX,{"derivedFrom":[subQ1,subQ0]});Q32=makeQuery(id+"F15.imprint","IMPRINT",FACE,{"disambiguationData":[TD([[makeQuery(id+"F15.imprint","IMPRINT",EDGE,{"disambiguationData":[TD([[subQ2,-1.0]])],"derivedFrom":subQ1}),1.0]])]});}
            var Q33;
            {var subQ0=sQuery(id+"F15.wireOp",EDGE,"E126");var subQ1=sQuery(id+"F15.wireOp",EDGE,"E125.top");var subQ2=makeQuery(id+"F15.imprint","INTERSECT",VERTEX,{"derivedFrom":[subQ1,subQ0]});Q33=makeQuery(id+"F15.imprint","IMPRINT",FACE,{"disambiguationData":[TD([[makeQuery(id+"F15.imprint","IMPRINT",EDGE,{"disambiguationData":[TD([[subQ2,1.0]])],"derivedFrom":subQ1}),1.0]])]});}
            extrude(context, id + "F16", {"entities" : qUnion([Q0, Q1, Q2, Q3, Q4, Q5, Q6, Q7, Q8, Q9, Q10, Q11, Q12, Q13, Q14, Q15, Q16, Q17, Q18, Q19, Q20, Q21, Q22, Q23, Q24, Q25, Q26, Q27, Q28, Q29, Q30, Q31, Q32, Q33]), "operationType" : NewBodyOperationType.REMOVE, "oppositeDirection" : true, "depth" : 10.4 * mm});
        }
        {
            var Q0;
            Q0=makeQuery(id+"F15.imprint","IMPRINT",FACE,{"disambiguationData":[TD([[makeQuery(id+"F15.imprint","IMPRINT",EDGE,{"derivedFrom":sQuery(id+"F15.wireOp",EDGE,"E124.bottom")}),-1.0]])]});
            var Q1;
            {var subQ27=sQuery(id+"F15.wireOp",EDGE,"E151.left");Q1=makeQuery(id+"F15.imprint","IMPRINT",FACE,{"disambiguationData":[TD([[makeQuery(id+"F15.imprint","IMPRINT",EDGE,{"derivedFrom":subQ27}),1.0]])]});}
            var Q2;
            {var subQ2=sQuery(id+"F15.wireOp",EDGE,"E152");Q2=makeQuery(id+"F15.imprint","IMPRINT",FACE,{"disambiguationData":[TD([[makeQuery(id+"F15.imprint","IMPRINT",EDGE,{"derivedFrom":subQ2}),-1.0]])]});}
            var Q3;
            {var subQ9=sQuery(id+"F15.wireOp",EDGE,"E151.right");Q3=makeQuery(id+"F15.imprint","IMPRINT",FACE,{"disambiguationData":[TD([[makeQuery(id+"F15.imprint","IMPRINT",EDGE,{"derivedFrom":subQ9}),-1.0]])]});}
            var Q4;
            {var subQ0=sQuery(id+"F15.wireOp",EDGE,"E126");var subQ1=sQuery(id+"F15.wireOp",EDGE,"E125.bottom");var subQ2=makeQuery(id+"F15.imprint","INTERSECT",VERTEX,{"derivedFrom":[subQ1,subQ0]});Q4=makeQuery(id+"F15.imprint","IMPRINT",FACE,{"disambiguationData":[TD([[makeQuery(id+"F15.imprint","IMPRINT",EDGE,{"disambiguationData":[TD([[subQ2,1.0]])],"derivedFrom":subQ1}),-1.0]])]});}
            var Q5;
            {var subQ0=sQuery(id+"F15.wireOp",EDGE,"E129");var subQ1=sQuery(id+"F15.wireOp",EDGE,"E126");var subQ2=makeQuery(id+"F15.imprint","INTERSECT",VERTEX,{"derivedFrom":[subQ1,subQ0]});Q5=makeQuery(id+"F15.imprint","IMPRINT",FACE,{"disambiguationData":[TD([[makeQuery(id+"F15.imprint","IMPRINT",EDGE,{"disambiguationData":[TD([[subQ2,1.0]])],"derivedFrom":subQ1}),-1.0]])]});}
            var Q6;
            {var subQ0=sQuery(id+"F15.wireOp",EDGE,"E129");var subQ1=sQuery(id+"F15.wireOp",EDGE,"E125.right");var subQ2=makeQuery(id+"F15.imprint","INTERSECT",VERTEX,{"derivedFrom":[subQ1,subQ0]});Q6=makeQuery(id+"F15.imprint","IMPRINT",FACE,{"disambiguationData":[TD([[makeQuery(id+"F15.imprint","IMPRINT",EDGE,{"disambiguationData":[TD([[subQ2,1.0]])],"derivedFrom":subQ1}),-1.0]])]});}
            var Q7;
            {var subQ0=sQuery(id+"F15.wireOp",EDGE,"E129");var subQ1=sQuery(id+"F15.wireOp",EDGE,"E125.left");var subQ2=makeQuery(id+"F15.imprint","INTERSECT",VERTEX,{"derivedFrom":[subQ1,subQ0]});Q7=makeQuery(id+"F15.imprint","IMPRINT",FACE,{"disambiguationData":[TD([[makeQuery(id+"F15.imprint","IMPRINT",EDGE,{"disambiguationData":[TD([[subQ2,1.0]])],"derivedFrom":subQ1}),1.0]])]});}
            var Q8;
            {var subQ0=sQuery(id+"F15.wireOp",EDGE,"E129");var subQ1=sQuery(id+"F15.wireOp",EDGE,"E126");var subQ2=makeQuery(id+"F15.imprint","INTERSECT",VERTEX,{"derivedFrom":[subQ1,subQ0]});Q8=makeQuery(id+"F15.imprint","IMPRINT",FACE,{"disambiguationData":[TD([[makeQuery(id+"F15.imprint","IMPRINT",EDGE,{"disambiguationData":[TD([[subQ2,-1.0]])],"derivedFrom":subQ1}),-1.0]])]});}
            var Q9;
            {var subQ0=sQuery(id+"F15.wireOp",EDGE,"E131");var subQ1=sQuery(id+"F15.wireOp",EDGE,"E125.right");var subQ2=makeQuery(id+"F15.imprint","INTERSECT",VERTEX,{"derivedFrom":[subQ1,subQ0]});Q9=makeQuery(id+"F15.imprint","IMPRINT",FACE,{"disambiguationData":[TD([[makeQuery(id+"F15.imprint","IMPRINT",EDGE,{"disambiguationData":[TD([[subQ2,1.0]])],"derivedFrom":subQ1}),-1.0]])]});}
            var Q10;
            {var subQ0=sQuery(id+"F15.wireOp",EDGE,"E126");var subQ1=sQuery(id+"F15.wireOp",EDGE,"E125.top");var subQ2=makeQuery(id+"F15.imprint","INTERSECT",VERTEX,{"derivedFrom":[subQ1,subQ0]});Q10=makeQuery(id+"F15.imprint","IMPRINT",FACE,{"disambiguationData":[TD([[makeQuery(id+"F15.imprint","IMPRINT",EDGE,{"disambiguationData":[TD([[subQ2,1.0]])],"derivedFrom":subQ1}),1.0]])]});}
            var Q11;
            {var subQ0=sQuery(id+"F15.wireOp",EDGE,"E130");var subQ1=sQuery(id+"F15.wireOp",EDGE,"E126");var subQ2=makeQuery(id+"F15.imprint","INTERSECT",VERTEX,{"derivedFrom":[subQ1,subQ0]});Q11=makeQuery(id+"F15.imprint","IMPRINT",FACE,{"disambiguationData":[TD([[makeQuery(id+"F15.imprint","IMPRINT",EDGE,{"disambiguationData":[TD([[subQ2,-1.0]])],"derivedFrom":subQ1}),-1.0]])]});}
            var Q12;
            {var subQ0=sQuery(id+"F15.wireOp",EDGE,"E130");var subQ1=sQuery(id+"F15.wireOp",EDGE,"E125.left");var subQ2=makeQuery(id+"F15.imprint","INTERSECT",VERTEX,{"derivedFrom":[subQ1,subQ0]});Q12=makeQuery(id+"F15.imprint","IMPRINT",FACE,{"disambiguationData":[TD([[makeQuery(id+"F15.imprint","IMPRINT",EDGE,{"disambiguationData":[TD([[subQ2,-1.0]])],"derivedFrom":subQ1}),1.0]])]});}
            var Q13;
            {var subQ0=sQuery(id+"F15.wireOp",EDGE,"E143");var subQ1=sQuery(id+"F15.wireOp",EDGE,"E138.right");var subQ2=makeQuery(id+"F15.imprint","INTERSECT",VERTEX,{"derivedFrom":[subQ1,subQ0]});Q13=makeQuery(id+"F15.imprint","IMPRINT",FACE,{"disambiguationData":[TD([[makeQuery(id+"F15.imprint","IMPRINT",EDGE,{"disambiguationData":[TD([[subQ2,-1.0]])],"derivedFrom":subQ1}),-1.0]])]});}
            var Q14;
            {var subQ0=sQuery(id+"F15.wireOp",EDGE,"E144");var subQ1=sQuery(id+"F15.wireOp",EDGE,"E139");var subQ2=makeQuery(id+"F15.imprint","INTERSECT",VERTEX,{"derivedFrom":[subQ1,subQ0]});Q14=makeQuery(id+"F15.imprint","IMPRINT",FACE,{"disambiguationData":[TD([[makeQuery(id+"F15.imprint","IMPRINT",EDGE,{"disambiguationData":[TD([[subQ2,1.0]])],"derivedFrom":subQ1}),-1.0]])]});}
            var Q15;
            {var subQ0=sQuery(id+"F15.wireOp",EDGE,"E143");var subQ1=sQuery(id+"F15.wireOp",EDGE,"E138.left");var subQ2=makeQuery(id+"F15.imprint","INTERSECT",VERTEX,{"derivedFrom":[subQ1,subQ0]});Q15=makeQuery(id+"F15.imprint","IMPRINT",FACE,{"disambiguationData":[TD([[makeQuery(id+"F15.imprint","IMPRINT",EDGE,{"disambiguationData":[TD([[subQ2,-1.0]])],"derivedFrom":subQ1}),1.0]])]});}
            var Q16;
            {var subQ0=sQuery(id+"F15.wireOp",EDGE,"E142");var subQ1=sQuery(id+"F15.wireOp",EDGE,"E139");var subQ2=makeQuery(id+"F15.imprint","INTERSECT",VERTEX,{"derivedFrom":[subQ1,subQ0]});Q16=makeQuery(id+"F15.imprint","IMPRINT",FACE,{"disambiguationData":[TD([[makeQuery(id+"F15.imprint","IMPRINT",EDGE,{"disambiguationData":[TD([[subQ2,-1.0]])],"derivedFrom":subQ1}),-1.0]])]});}
            var Q17;
            {var subQ0=sQuery(id+"F15.wireOp",EDGE,"E139");var subQ1=sQuery(id+"F15.wireOp",EDGE,"E138.top");var subQ2=makeQuery(id+"F15.imprint","INTERSECT",VERTEX,{"derivedFrom":[subQ1,subQ0]});Q17=makeQuery(id+"F15.imprint","IMPRINT",FACE,{"disambiguationData":[TD([[makeQuery(id+"F15.imprint","IMPRINT",EDGE,{"disambiguationData":[TD([[subQ2,1.0]])],"derivedFrom":subQ1}),1.0]])]});}
            var Q18;
            {var subQ0=sQuery(id+"F15.wireOp",EDGE,"E139");var subQ1=sQuery(id+"F15.wireOp",EDGE,"E138.bottom");var subQ2=makeQuery(id+"F15.imprint","INTERSECT",VERTEX,{"derivedFrom":[subQ1,subQ0]});Q18=makeQuery(id+"F15.imprint","IMPRINT",FACE,{"disambiguationData":[TD([[makeQuery(id+"F15.imprint","IMPRINT",EDGE,{"disambiguationData":[TD([[subQ2,1.0]])],"derivedFrom":subQ1}),-1.0]])]});}
            var Q19;
            {var subQ0=sQuery(id+"F15.wireOp",EDGE,"E142");var subQ1=sQuery(id+"F15.wireOp",EDGE,"E139");var subQ2=makeQuery(id+"F15.imprint","INTERSECT",VERTEX,{"derivedFrom":[subQ1,subQ0]});Q19=makeQuery(id+"F15.imprint","IMPRINT",FACE,{"disambiguationData":[TD([[makeQuery(id+"F15.imprint","IMPRINT",EDGE,{"disambiguationData":[TD([[subQ2,1.0]])],"derivedFrom":subQ1}),-1.0]])]});}
            var Q20;
            {var subQ0=sQuery(id+"F15.wireOp",EDGE,"E142");var subQ1=sQuery(id+"F15.wireOp",EDGE,"E138.right");var subQ2=makeQuery(id+"F15.imprint","INTERSECT",VERTEX,{"derivedFrom":[subQ1,subQ0]});Q20=makeQuery(id+"F15.imprint","IMPRINT",FACE,{"disambiguationData":[TD([[makeQuery(id+"F15.imprint","IMPRINT",EDGE,{"disambiguationData":[TD([[subQ2,1.0]])],"derivedFrom":subQ1}),-1.0]])]});}
            var Q21;
            {var subQ0=sQuery(id+"F15.wireOp",EDGE,"E142");var subQ1=sQuery(id+"F15.wireOp",EDGE,"E138.left");var subQ2=makeQuery(id+"F15.imprint","INTERSECT",VERTEX,{"derivedFrom":[subQ1,subQ0]});Q21=makeQuery(id+"F15.imprint","IMPRINT",FACE,{"disambiguationData":[TD([[makeQuery(id+"F15.imprint","IMPRINT",EDGE,{"disambiguationData":[TD([[subQ2,1.0]])],"derivedFrom":subQ1}),1.0]])]});}
            extrude(context, id + "F17", {"entities" : qUnion([Q0, Q1, Q2, Q3, Q4, Q5, Q6, Q7, Q8, Q9, Q10, Q11, Q12, Q13, Q14, Q15, Q16, Q17, Q18, Q19, Q20, Q21]), "operationType" : NewBodyOperationType.ADD, "oppositeDirection" : true, "depth" : 2.54 * mm, "hasSecondDirection" : true, "secondDirectionOppositeDirection" : true, "secondDirectionDepth" : 1.27 * mm});
        }
        {
            var Q0;
            Q0=makeQuery(id+"F15.imprint","IMPRINT",FACE,{"disambiguationData":[TD([[makeQuery(id+"F15.imprint","IMPRINT",EDGE,{"derivedFrom":sQuery(id+"F15.wireOp",EDGE,"E124.bottom")}),-1.0]])]});
            var Q1;
            {var subQ0=sQuery(id+"F15.wireOp",EDGE,"E154");Q1=makeQuery(id+"F15.imprint","IMPRINT",FACE,{"disambiguationData":[TD([[makeQuery(id+"F15.imprint","IMPRINT",EDGE,{"derivedFrom":subQ0}),1.0]])]});}
            extrude(context, id + "F18", {"entities" : qUnion([Q0, Q1]), "operationType" : NewBodyOperationType.REMOVE, "oppositeDirection" : true, "depth" : 10.4 * mm});
        }
        {
            var Q0;
            Q0=makeQuery(id+"F1.opExtrude","SWEPT_FACE",FACE,{"disambiguationData":[OSD([sQuery(id+"F0.wireOp",EDGE,"E6")])]});
            var sketch = newSketch(context, id + "F19", { "sketchPlane" : qUnion([Q0])});
            skLineSegment(sketch, "E157.bottom", {"start": v(265.89, 0) * mm, "end": v(314.15, 0) * mm});
            skLineSegment(sketch, "E157.top", {"start": v(265.89, 57.15) * mm, "end": v(314.15, 57.15) * mm});
            skLineSegment(sketch, "E157.left", {"start": v(265.89, 0) * mm, "end": v(265.89, 57.15) * mm});
            skLineSegment(sketch, "E157.right", {"start": v(314.15, 0) * mm, "end": v(314.15, 57.15) * mm});
            skLineSegment(sketch, "E158", {"start": v(266.65, 0) * mm, "end": v(266.65, 56.39) * mm});
            skLineSegment(sketch, "E159", {"start": v(266.65, 56.39) * mm, "end": v(313.39, 56.39) * mm});
            skLineSegment(sketch, "E160", {"start": v(313.39, 56.39) * mm, "end": v(313.39, 0) * mm});
            skLineSegment(sketch, "E161.bottom", {"start": v(268.68, 54.36) * mm, "end": v(277.95, 54.36) * mm});
            skLineSegment(sketch, "E161.top", {"start": v(268.68, 2.03) * mm, "end": v(277.95, 2.03) * mm});
            skLineSegment(sketch, "E161.left", {"start": v(268.68, 54.36) * mm, "end": v(268.68, 41.75) * mm});
            skLineSegment(sketch, "E161.right", {"start": v(287.86, 54.36) * mm, "end": v(287.86, 41.75) * mm});
            skLineSegment(sketch, "E162.bottom", {"start": v(292.18, 54.36) * mm, "end": v(301.45, 54.36) * mm});
            skLineSegment(sketch, "E162.top", {"start": v(292.18, 2.03) * mm, "end": v(301.45, 2.03) * mm});
            skLineSegment(sketch, "E162.left", {"start": v(292.18, 54.36) * mm, "end": v(292.18, 41.75) * mm});
            skLineSegment(sketch, "E162.right", {"start": v(311.35, 54.36) * mm, "end": v(311.35, 41.75) * mm});
            skLineSegment(sketch, "E163", {"start": v(289.9, 0) * mm, "end": v(289.9, 56.39) * mm});
            skLineSegment(sketch, "E164", {"start": v(290.14, 0) * mm, "end": v(290.14, 56.39) * mm});
            skLineSegment(sketch, "E165", {"start": v(277.95, 54.36) * mm, "end": v(277.95, 41.75) * mm});
            skLineSegment(sketch, "E166", {"start": v(277.95, 41.75) * mm, "end": v(268.68, 41.75) * mm});
            skLineSegment(sketch, "E167", {"start": v(278.59, 54.36) * mm, "end": v(278.59, 41.75) * mm});
            skLineSegment(sketch, "E168", {"start": v(278.59, 41.75) * mm, "end": v(287.86, 41.75) * mm});
            skLineSegment(sketch, "E169", {"start": v(287.86, 41.12) * mm, "end": v(278.59, 41.12) * mm});
            skLineSegment(sketch, "E170", {"start": v(278.59, 41.12) * mm, "end": v(278.59, 28.51) * mm});
            skLineSegment(sketch, "E171", {"start": v(278.59, 28.51) * mm, "end": v(287.86, 28.51) * mm});
            skLineSegment(sketch, "E172", {"start": v(268.68, 41.12) * mm, "end": v(277.95, 41.12) * mm});
            skLineSegment(sketch, "E173", {"start": v(277.95, 41.12) * mm, "end": v(277.95, 28.51) * mm});
            skLineSegment(sketch, "E174", {"start": v(277.95, 28.51) * mm, "end": v(268.68, 28.51) * mm});
            skLineSegment(sketch, "E175", {"start": v(268.68, 27.88) * mm, "end": v(277.95, 27.88) * mm});
            skLineSegment(sketch, "E176", {"start": v(277.95, 27.88) * mm, "end": v(277.95, 15.27) * mm});
            skLineSegment(sketch, "E177", {"start": v(277.95, 15.27) * mm, "end": v(268.68, 15.27) * mm});
            skLineSegment(sketch, "E178", {"start": v(287.86, 27.88) * mm, "end": v(278.59, 27.88) * mm});
            skLineSegment(sketch, "E179", {"start": v(278.59, 27.88) * mm, "end": v(278.59, 15.27) * mm});
            skLineSegment(sketch, "E180", {"start": v(278.59, 15.27) * mm, "end": v(287.86, 15.27) * mm});
            skLineSegment(sketch, "E181", {"start": v(268.68, 14.64) * mm, "end": v(277.95, 14.64) * mm});
            skLineSegment(sketch, "E182", {"start": v(277.95, 14.64) * mm, "end": v(277.95, 2.03) * mm});
            skLineSegment(sketch, "E183", {"start": v(287.86, 14.64) * mm, "end": v(278.59, 14.64) * mm});
            skLineSegment(sketch, "E184", {"start": v(278.59, 14.64) * mm, "end": v(278.59, 2.03) * mm});
            skLineSegment(sketch, "E185", {"start": v(301.45, 54.36) * mm, "end": v(301.45, 41.75) * mm});
            skLineSegment(sketch, "E186", {"start": v(301.45, 41.75) * mm, "end": v(292.18, 41.75) * mm});
            skLineSegment(sketch, "E187", {"start": v(292.18, 41.12) * mm, "end": v(301.45, 41.12) * mm});
            skLineSegment(sketch, "E188", {"start": v(301.45, 41.12) * mm, "end": v(301.45, 28.51) * mm});
            skLineSegment(sketch, "E189", {"start": v(301.45, 28.51) * mm, "end": v(292.18, 28.51) * mm});
            skLineSegment(sketch, "E190", {"start": v(292.18, 27.88) * mm, "end": v(301.45, 27.88) * mm});
            skLineSegment(sketch, "E191", {"start": v(301.45, 27.88) * mm, "end": v(301.45, 15.27) * mm});
            skLineSegment(sketch, "E192", {"start": v(301.45, 15.27) * mm, "end": v(292.18, 15.27) * mm});
            skLineSegment(sketch, "E193", {"start": v(292.18, 14.64) * mm, "end": v(301.45, 14.64) * mm});
            skLineSegment(sketch, "E194", {"start": v(301.45, 14.64) * mm, "end": v(301.45, 2.03) * mm});
            skLineSegment(sketch, "E195", {"start": v(311.35, 14.64) * mm, "end": v(302.08, 14.64) * mm});
            skLineSegment(sketch, "E196", {"start": v(302.08, 14.64) * mm, "end": v(302.08, 2.03) * mm});
            skLineSegment(sketch, "E197", {"start": v(311.35, 15.27) * mm, "end": v(302.08, 15.27) * mm});
            skLineSegment(sketch, "E198", {"start": v(302.08, 15.27) * mm, "end": v(302.08, 27.88) * mm});
            skLineSegment(sketch, "E199", {"start": v(302.08, 27.88) * mm, "end": v(311.35, 27.88) * mm});
            skLineSegment(sketch, "E200", {"start": v(311.35, 28.51) * mm, "end": v(302.08, 28.51) * mm});
            skLineSegment(sketch, "E201", {"start": v(302.08, 28.51) * mm, "end": v(302.08, 41.12) * mm});
            skLineSegment(sketch, "E202", {"start": v(302.08, 41.12) * mm, "end": v(311.35, 41.12) * mm});
            skLineSegment(sketch, "E203", {"start": v(311.35, 41.75) * mm, "end": v(302.08, 41.75) * mm});
            skLineSegment(sketch, "E204", {"start": v(302.08, 41.75) * mm, "end": v(302.08, 54.36) * mm});
            skLineSegment(sketch, "E205.bottom", {"start": v(30.3, 0) * mm, "end": v(78.56, 0) * mm});
            skLineSegment(sketch, "E205.top", {"start": v(30.3, 57.15) * mm, "end": v(78.56, 57.15) * mm});
            skLineSegment(sketch, "E205.left", {"start": v(30.3, 0) * mm, "end": v(30.3, 57.15) * mm});
            skLineSegment(sketch, "E205.right", {"start": v(78.56, 0) * mm, "end": v(78.56, 57.15) * mm});
            skLineSegment(sketch, "E206", {"start": v(31.06, 0) * mm, "end": v(31.06, 56.39) * mm});
            skLineSegment(sketch, "E207", {"start": v(31.06, 56.39) * mm, "end": v(77.8, 56.39) * mm});
            skLineSegment(sketch, "E208", {"start": v(77.8, 56.39) * mm, "end": v(77.8, 0) * mm});
            skLineSegment(sketch, "E209.bottom", {"start": v(33.1, 54.36) * mm, "end": v(42.37, 54.36) * mm});
            skLineSegment(sketch, "E209.top", {"start": v(33.1, 2.03) * mm, "end": v(42.37, 2.03) * mm});
            skLineSegment(sketch, "E209.left", {"start": v(33.1, 54.36) * mm, "end": v(33.1, 41.75) * mm});
            skLineSegment(sketch, "E209.right", {"start": v(52.27, 54.36) * mm, "end": v(52.27, 41.75) * mm});
            skLineSegment(sketch, "E210.bottom", {"start": v(56.6, 54.36) * mm, "end": v(65.86, 54.36) * mm});
            skLineSegment(sketch, "E210.top", {"start": v(56.6, 2.03) * mm, "end": v(65.86, 2.03) * mm});
            skLineSegment(sketch, "E210.left", {"start": v(56.6, 54.36) * mm, "end": v(56.6, 41.75) * mm});
            skLineSegment(sketch, "E210.right", {"start": v(75.77, 54.36) * mm, "end": v(75.77, 41.75) * mm});
            skLineSegment(sketch, "E211", {"start": v(54.3, 0) * mm, "end": v(54.3, 56.39) * mm});
            skLineSegment(sketch, "E212", {"start": v(54.56, 0) * mm, "end": v(54.56, 56.39) * mm});
            skLineSegment(sketch, "E213", {"start": v(42.37, 54.36) * mm, "end": v(42.37, 41.75) * mm});
            skLineSegment(sketch, "E214", {"start": v(42.37, 41.75) * mm, "end": v(33.1, 41.75) * mm});
            skLineSegment(sketch, "E215", {"start": v(43, 54.36) * mm, "end": v(43, 41.75) * mm});
            skLineSegment(sketch, "E216", {"start": v(43, 41.75) * mm, "end": v(52.27, 41.75) * mm});
            skLineSegment(sketch, "E217", {"start": v(52.27, 41.12) * mm, "end": v(43, 41.12) * mm});
            skLineSegment(sketch, "E218", {"start": v(43, 41.12) * mm, "end": v(43, 28.51) * mm});
            skLineSegment(sketch, "E219", {"start": v(43, 28.51) * mm, "end": v(52.27, 28.51) * mm});
            skLineSegment(sketch, "E220", {"start": v(33.1, 41.12) * mm, "end": v(42.37, 41.12) * mm});
            skLineSegment(sketch, "E221", {"start": v(42.37, 41.12) * mm, "end": v(42.37, 28.51) * mm});
            skLineSegment(sketch, "E222", {"start": v(42.37, 28.51) * mm, "end": v(33.1, 28.51) * mm});
            skLineSegment(sketch, "E223", {"start": v(33.1, 27.88) * mm, "end": v(42.37, 27.88) * mm});
            skLineSegment(sketch, "E224", {"start": v(42.37, 27.88) * mm, "end": v(42.37, 15.27) * mm});
            skLineSegment(sketch, "E225", {"start": v(42.37, 15.27) * mm, "end": v(33.1, 15.27) * mm});
            skLineSegment(sketch, "E226", {"start": v(52.27, 27.88) * mm, "end": v(43, 27.88) * mm});
            skLineSegment(sketch, "E227", {"start": v(43, 27.88) * mm, "end": v(43, 15.27) * mm});
            skLineSegment(sketch, "E228", {"start": v(43, 15.27) * mm, "end": v(52.27, 15.27) * mm});
            skLineSegment(sketch, "E229", {"start": v(33.1, 14.64) * mm, "end": v(42.37, 14.64) * mm});
            skLineSegment(sketch, "E230", {"start": v(42.37, 14.64) * mm, "end": v(42.37, 2.03) * mm});
            skLineSegment(sketch, "E231", {"start": v(52.27, 14.64) * mm, "end": v(43, 14.64) * mm});
            skLineSegment(sketch, "E232", {"start": v(43, 14.64) * mm, "end": v(43, 2.03) * mm});
            skLineSegment(sketch, "E233", {"start": v(65.86, 54.36) * mm, "end": v(65.86, 41.75) * mm});
            skLineSegment(sketch, "E234", {"start": v(65.86, 41.75) * mm, "end": v(56.6, 41.75) * mm});
            skLineSegment(sketch, "E235", {"start": v(56.6, 41.12) * mm, "end": v(65.86, 41.12) * mm});
            skLineSegment(sketch, "E236", {"start": v(65.86, 41.12) * mm, "end": v(65.86, 28.51) * mm});
            skLineSegment(sketch, "E237", {"start": v(65.86, 28.51) * mm, "end": v(56.6, 28.51) * mm});
            skLineSegment(sketch, "E238", {"start": v(56.6, 27.88) * mm, "end": v(65.86, 27.88) * mm});
            skLineSegment(sketch, "E239", {"start": v(65.86, 27.88) * mm, "end": v(65.86, 15.27) * mm});
            skLineSegment(sketch, "E240", {"start": v(65.86, 15.27) * mm, "end": v(56.6, 15.27) * mm});
            skLineSegment(sketch, "E241", {"start": v(56.6, 14.64) * mm, "end": v(65.86, 14.64) * mm});
            skLineSegment(sketch, "E242", {"start": v(65.86, 14.64) * mm, "end": v(65.86, 2.03) * mm});
            skLineSegment(sketch, "E243", {"start": v(75.77, 14.64) * mm, "end": v(66.5, 14.64) * mm});
            skLineSegment(sketch, "E244", {"start": v(66.5, 14.64) * mm, "end": v(66.5, 2.03) * mm});
            skLineSegment(sketch, "E245", {"start": v(75.77, 15.27) * mm, "end": v(66.5, 15.27) * mm});
            skLineSegment(sketch, "E246", {"start": v(66.5, 15.27) * mm, "end": v(66.5, 27.88) * mm});
            skLineSegment(sketch, "E247", {"start": v(66.5, 27.88) * mm, "end": v(75.77, 27.88) * mm});
            skLineSegment(sketch, "E248", {"start": v(75.77, 28.51) * mm, "end": v(66.5, 28.51) * mm});
            skLineSegment(sketch, "E249", {"start": v(66.5, 28.51) * mm, "end": v(66.5, 41.12) * mm});
            skLineSegment(sketch, "E250", {"start": v(66.5, 41.12) * mm, "end": v(75.77, 41.12) * mm});
            skLineSegment(sketch, "E251", {"start": v(75.77, 41.75) * mm, "end": v(66.5, 41.75) * mm});
            skLineSegment(sketch, "E252", {"start": v(66.5, 41.75) * mm, "end": v(66.5, 54.36) * mm});
            skLineSegment(sketch, "E253.trimOffspring", {"start": v(43, 54.36) * mm, "end": v(52.27, 54.36) * mm});
            skLineSegment(sketch, "E254.trimOffspring", {"start": v(52.27, 41.12) * mm, "end": v(52.27, 28.51) * mm});
            skLineSegment(sketch, "E255.trimOffspring", {"start": v(33.1, 41.12) * mm, "end": v(33.1, 28.51) * mm});
            skLineSegment(sketch, "E256.trimOffspring", {"start": v(52.27, 27.88) * mm, "end": v(52.27, 15.27) * mm});
            skLineSegment(sketch, "E257.trimOffspring", {"start": v(33.1, 27.88) * mm, "end": v(33.1, 15.27) * mm});
            skLineSegment(sketch, "E258.trimOffspring", {"start": v(52.27, 14.64) * mm, "end": v(52.27, 2.03) * mm});
            skLineSegment(sketch, "E259.trimOffspring", {"start": v(33.1, 14.64) * mm, "end": v(33.1, 2.03) * mm});
            skLineSegment(sketch, "E260.trimOffspring", {"start": v(43, 2.03) * mm, "end": v(52.27, 2.03) * mm});
            skLineSegment(sketch, "E261.trimOffspring", {"start": v(66.5, 2.03) * mm, "end": v(75.77, 2.03) * mm});
            skLineSegment(sketch, "E262.trimOffspring", {"start": v(75.77, 14.64) * mm, "end": v(75.77, 2.03) * mm});
            skLineSegment(sketch, "E263.trimOffspring", {"start": v(56.6, 14.64) * mm, "end": v(56.6, 2.03) * mm});
            skLineSegment(sketch, "E264.trimOffspring", {"start": v(56.6, 27.88) * mm, "end": v(56.6, 15.27) * mm});
            skLineSegment(sketch, "E265.trimOffspring", {"start": v(75.77, 27.88) * mm, "end": v(75.77, 15.27) * mm});
            skLineSegment(sketch, "E266.trimOffspring", {"start": v(66.5, 54.36) * mm, "end": v(75.77, 54.36) * mm});
            skLineSegment(sketch, "E267.trimOffspring", {"start": v(75.77, 41.12) * mm, "end": v(75.77, 28.51) * mm});
            skLineSegment(sketch, "E268.trimOffspring", {"start": v(56.6, 41.12) * mm, "end": v(56.6, 28.51) * mm});
            skLineSegment(sketch, "E269.trimOffspring", {"start": v(278.59, 54.36) * mm, "end": v(287.86, 54.36) * mm});
            skLineSegment(sketch, "E270.trimOffspring", {"start": v(268.68, 41.12) * mm, "end": v(268.68, 28.51) * mm});
            skLineSegment(sketch, "E271.trimOffspring", {"start": v(287.86, 41.12) * mm, "end": v(287.86, 28.51) * mm});
            skLineSegment(sketch, "E272.trimOffspring", {"start": v(302.08, 54.36) * mm, "end": v(311.35, 54.36) * mm});
            skLineSegment(sketch, "E273.trimOffspring", {"start": v(311.35, 41.12) * mm, "end": v(311.35, 28.51) * mm});
            skLineSegment(sketch, "E274.trimOffspring", {"start": v(292.18, 41.12) * mm, "end": v(292.18, 28.51) * mm});
            skLineSegment(sketch, "E275.trimOffspring", {"start": v(311.35, 27.88) * mm, "end": v(311.35, 15.27) * mm});
            skLineSegment(sketch, "E276.trimOffspring", {"start": v(292.18, 27.88) * mm, "end": v(292.18, 15.27) * mm});
            skLineSegment(sketch, "E277.trimOffspring", {"start": v(287.86, 27.88) * mm, "end": v(287.86, 15.27) * mm});
            skLineSegment(sketch, "E278.trimOffspring", {"start": v(268.68, 27.88) * mm, "end": v(268.68, 15.27) * mm});
            skLineSegment(sketch, "E279.trimOffspring", {"start": v(268.68, 14.64) * mm, "end": v(268.68, 2.03) * mm});
            skLineSegment(sketch, "E280.trimOffspring", {"start": v(287.86, 14.64) * mm, "end": v(287.86, 2.03) * mm});
            skLineSegment(sketch, "E281.trimOffspring", {"start": v(292.18, 14.64) * mm, "end": v(292.18, 2.03) * mm});
            skLineSegment(sketch, "E282.trimOffspring", {"start": v(311.35, 14.64) * mm, "end": v(311.35, 2.03) * mm});
            skLineSegment(sketch, "E283.trimOffspring", {"start": v(302.08, 2.03) * mm, "end": v(311.35, 2.03) * mm});
            skLineSegment(sketch, "E284.trimOffspring", {"start": v(278.59, 2.03) * mm, "end": v(287.86, 2.03) * mm});
            skSolve(sketch);
        }
        {
            var Q0;
            {var subQ0=sQuery(id+"F19.wireOp",EDGE,"E163");Q0=makeQuery(id+"F19.imprint","IMPRINT",FACE,{"disambiguationData":[TD([[makeQuery(id+"F19.imprint","IMPRINT",EDGE,{"derivedFrom":subQ0}),-1.0]])]});}
            var Q1;
            {var subQ0=sQuery(id+"F19.wireOp",EDGE,"E211");Q1=makeQuery(id+"F19.imprint","IMPRINT",FACE,{"disambiguationData":[TD([[makeQuery(id+"F19.imprint","IMPRINT",EDGE,{"derivedFrom":subQ0}),-1.0]])]});}
            var Q2;
            Q2=makeQuery(id+"F19.imprint","IMPRINT",FACE,{"disambiguationData":[TD([[makeQuery(id+"F19.imprint","IMPRINT",EDGE,{"derivedFrom":sQuery(id+"F19.wireOp",EDGE,"E209.bottom")}),-1.0]])]});
            var Q3;
            Q3=makeQuery(id+"F19.imprint","IMPRINT",FACE,{"disambiguationData":[TD([[makeQuery(id+"F19.imprint","IMPRINT",EDGE,{"derivedFrom":sQuery(id+"F19.wireOp",EDGE,"E209.right")}),-1.0]])]});
            var Q4;
            Q4=makeQuery(id+"F19.imprint","IMPRINT",FACE,{"disambiguationData":[TD([[makeQuery(id+"F19.imprint","IMPRINT",EDGE,{"derivedFrom":sQuery(id+"F19.wireOp",EDGE,"E217")}),1.0]])]});
            var Q5;
            Q5=makeQuery(id+"F19.imprint","IMPRINT",FACE,{"disambiguationData":[TD([[makeQuery(id+"F19.imprint","IMPRINT",EDGE,{"derivedFrom":sQuery(id+"F19.wireOp",EDGE,"E220")}),-1.0]])]});
            var Q6;
            Q6=makeQuery(id+"F19.imprint","IMPRINT",FACE,{"disambiguationData":[TD([[makeQuery(id+"F19.imprint","IMPRINT",EDGE,{"derivedFrom":sQuery(id+"F19.wireOp",EDGE,"E223")}),-1.0]])]});
            var Q7;
            Q7=makeQuery(id+"F19.imprint","IMPRINT",FACE,{"disambiguationData":[TD([[makeQuery(id+"F19.imprint","IMPRINT",EDGE,{"derivedFrom":sQuery(id+"F19.wireOp",EDGE,"E226")}),1.0]])]});
            var Q8;
            Q8=makeQuery(id+"F19.imprint","IMPRINT",FACE,{"disambiguationData":[TD([[makeQuery(id+"F19.imprint","IMPRINT",EDGE,{"derivedFrom":sQuery(id+"F19.wireOp",EDGE,"E231")}),1.0]])]});
            var Q9;
            Q9=makeQuery(id+"F19.imprint","IMPRINT",FACE,{"disambiguationData":[TD([[makeQuery(id+"F19.imprint","IMPRINT",EDGE,{"derivedFrom":sQuery(id+"F19.wireOp",EDGE,"E209.top")}),1.0]])]});
            var Q10;
            Q10=makeQuery(id+"F19.imprint","IMPRINT",FACE,{"disambiguationData":[TD([[makeQuery(id+"F19.imprint","IMPRINT",EDGE,{"derivedFrom":sQuery(id+"F19.wireOp",EDGE,"E210.bottom")}),-1.0]])]});
            var Q11;
            Q11=makeQuery(id+"F19.imprint","IMPRINT",FACE,{"disambiguationData":[TD([[makeQuery(id+"F19.imprint","IMPRINT",EDGE,{"derivedFrom":sQuery(id+"F19.wireOp",EDGE,"E210.right")}),-1.0]])]});
            var Q12;
            Q12=makeQuery(id+"F19.imprint","IMPRINT",FACE,{"disambiguationData":[TD([[makeQuery(id+"F19.imprint","IMPRINT",EDGE,{"derivedFrom":sQuery(id+"F19.wireOp",EDGE,"E248")}),-1.0]])]});
            var Q13;
            Q13=makeQuery(id+"F19.imprint","IMPRINT",FACE,{"disambiguationData":[TD([[makeQuery(id+"F19.imprint","IMPRINT",EDGE,{"derivedFrom":sQuery(id+"F19.wireOp",EDGE,"E235")}),-1.0]])]});
            var Q14;
            Q14=makeQuery(id+"F19.imprint","IMPRINT",FACE,{"disambiguationData":[TD([[makeQuery(id+"F19.imprint","IMPRINT",EDGE,{"derivedFrom":sQuery(id+"F19.wireOp",EDGE,"E238")}),-1.0]])]});
            var Q15;
            Q15=makeQuery(id+"F19.imprint","IMPRINT",FACE,{"disambiguationData":[TD([[makeQuery(id+"F19.imprint","IMPRINT",EDGE,{"derivedFrom":sQuery(id+"F19.wireOp",EDGE,"E245")}),-1.0]])]});
            var Q16;
            Q16=makeQuery(id+"F19.imprint","IMPRINT",FACE,{"disambiguationData":[TD([[makeQuery(id+"F19.imprint","IMPRINT",EDGE,{"derivedFrom":sQuery(id+"F19.wireOp",EDGE,"E243")}),1.0]])]});
            var Q17;
            Q17=makeQuery(id+"F19.imprint","IMPRINT",FACE,{"disambiguationData":[TD([[makeQuery(id+"F19.imprint","IMPRINT",EDGE,{"derivedFrom":sQuery(id+"F19.wireOp",EDGE,"E210.top")}),1.0]])]});
            var Q18;
            Q18=makeQuery(id+"F19.imprint","IMPRINT",FACE,{"disambiguationData":[TD([[makeQuery(id+"F19.imprint","IMPRINT",EDGE,{"derivedFrom":sQuery(id+"F19.wireOp",EDGE,"E161.bottom")}),-1.0]])]});
            var Q19;
            Q19=makeQuery(id+"F19.imprint","IMPRINT",FACE,{"disambiguationData":[TD([[makeQuery(id+"F19.imprint","IMPRINT",EDGE,{"derivedFrom":sQuery(id+"F19.wireOp",EDGE,"E161.right")}),-1.0]])]});
            var Q20;
            Q20=makeQuery(id+"F19.imprint","IMPRINT",FACE,{"disambiguationData":[TD([[makeQuery(id+"F19.imprint","IMPRINT",EDGE,{"derivedFrom":sQuery(id+"F19.wireOp",EDGE,"E169")}),1.0]])]});
            var Q21;
            Q21=makeQuery(id+"F19.imprint","IMPRINT",FACE,{"disambiguationData":[TD([[makeQuery(id+"F19.imprint","IMPRINT",EDGE,{"derivedFrom":sQuery(id+"F19.wireOp",EDGE,"E172")}),-1.0]])]});
            var Q22;
            Q22=makeQuery(id+"F19.imprint","IMPRINT",FACE,{"disambiguationData":[TD([[makeQuery(id+"F19.imprint","IMPRINT",EDGE,{"derivedFrom":sQuery(id+"F19.wireOp",EDGE,"E175")}),-1.0]])]});
            var Q23;
            Q23=makeQuery(id+"F19.imprint","IMPRINT",FACE,{"disambiguationData":[TD([[makeQuery(id+"F19.imprint","IMPRINT",EDGE,{"derivedFrom":sQuery(id+"F19.wireOp",EDGE,"E178")}),1.0]])]});
            var Q24;
            Q24=makeQuery(id+"F19.imprint","IMPRINT",FACE,{"disambiguationData":[TD([[makeQuery(id+"F19.imprint","IMPRINT",EDGE,{"derivedFrom":sQuery(id+"F19.wireOp",EDGE,"E183")}),1.0]])]});
            var Q25;
            Q25=makeQuery(id+"F19.imprint","IMPRINT",FACE,{"disambiguationData":[TD([[makeQuery(id+"F19.imprint","IMPRINT",EDGE,{"derivedFrom":sQuery(id+"F19.wireOp",EDGE,"E161.top")}),1.0]])]});
            var Q26;
            Q26=makeQuery(id+"F19.imprint","IMPRINT",FACE,{"disambiguationData":[TD([[makeQuery(id+"F19.imprint","IMPRINT",EDGE,{"derivedFrom":sQuery(id+"F19.wireOp",EDGE,"E162.top")}),1.0]])]});
            var Q27;
            Q27=makeQuery(id+"F19.imprint","IMPRINT",FACE,{"disambiguationData":[TD([[makeQuery(id+"F19.imprint","IMPRINT",EDGE,{"derivedFrom":sQuery(id+"F19.wireOp",EDGE,"E195")}),1.0]])]});
            var Q28;
            Q28=makeQuery(id+"F19.imprint","IMPRINT",FACE,{"disambiguationData":[TD([[makeQuery(id+"F19.imprint","IMPRINT",EDGE,{"derivedFrom":sQuery(id+"F19.wireOp",EDGE,"E197")}),-1.0]])]});
            var Q29;
            Q29=makeQuery(id+"F19.imprint","IMPRINT",FACE,{"disambiguationData":[TD([[makeQuery(id+"F19.imprint","IMPRINT",EDGE,{"derivedFrom":sQuery(id+"F19.wireOp",EDGE,"E190")}),-1.0]])]});
            var Q30;
            Q30=makeQuery(id+"F19.imprint","IMPRINT",FACE,{"disambiguationData":[TD([[makeQuery(id+"F19.imprint","IMPRINT",EDGE,{"derivedFrom":sQuery(id+"F19.wireOp",EDGE,"E187")}),-1.0]])]});
            var Q31;
            Q31=makeQuery(id+"F19.imprint","IMPRINT",FACE,{"disambiguationData":[TD([[makeQuery(id+"F19.imprint","IMPRINT",EDGE,{"derivedFrom":sQuery(id+"F19.wireOp",EDGE,"E200")}),-1.0]])]});
            var Q32;
            Q32=makeQuery(id+"F19.imprint","IMPRINT",FACE,{"disambiguationData":[TD([[makeQuery(id+"F19.imprint","IMPRINT",EDGE,{"derivedFrom":sQuery(id+"F19.wireOp",EDGE,"E162.right")}),-1.0]])]});
            var Q33;
            Q33=makeQuery(id+"F19.imprint","IMPRINT",FACE,{"disambiguationData":[TD([[makeQuery(id+"F19.imprint","IMPRINT",EDGE,{"derivedFrom":sQuery(id+"F19.wireOp",EDGE,"E162.bottom")}),-1.0]])]});
            extrude(context, id + "F20", {"entities" : qUnion([Q0, Q1, Q2, Q3, Q4, Q5, Q6, Q7, Q8, Q9, Q10, Q11, Q12, Q13, Q14, Q15, Q16, Q17, Q18, Q19, Q20, Q21, Q22, Q23, Q24, Q25, Q26, Q27, Q28, Q29, Q30, Q31, Q32, Q33]), "operationType" : NewBodyOperationType.REMOVE, "oppositeDirection" : true, "depth" : 10.4 * mm});
        }
        {
            var Q0;
            Q0=makeQuery(id+"F19.imprint","IMPRINT",FACE,{"disambiguationData":[TD([[makeQuery(id+"F19.imprint","IMPRINT",EDGE,{"derivedFrom":sQuery(id+"F19.wireOp",EDGE,"E205.top")}),-1.0]])]});
            var Q1;
            {var subQ0=sQuery(id+"F19.wireOp",EDGE,"E211");Q1=makeQuery(id+"F19.imprint","IMPRINT",FACE,{"disambiguationData":[TD([[makeQuery(id+"F19.imprint","IMPRINT",EDGE,{"derivedFrom":subQ0}),-1.0]])]});}
            var Q2;
            Q2=makeQuery(id+"F19.imprint","IMPRINT",FACE,{"disambiguationData":[TD([[makeQuery(id+"F19.imprint","IMPRINT",EDGE,{"derivedFrom":sQuery(id+"F19.wireOp",EDGE,"E157.top")}),-1.0]])]});
            var Q3;
            {var subQ1=sQuery(id+"F19.wireOp",EDGE,"E158");Q3=makeQuery(id+"F19.imprint","IMPRINT",FACE,{"disambiguationData":[TD([[makeQuery(id+"F19.imprint","IMPRINT",EDGE,{"derivedFrom":subQ1}),-1.0]])]});}
            var Q4;
            {var subQ1=sQuery(id+"F19.wireOp",EDGE,"E206");Q4=makeQuery(id+"F19.imprint","IMPRINT",FACE,{"disambiguationData":[TD([[makeQuery(id+"F19.imprint","IMPRINT",EDGE,{"derivedFrom":subQ1}),-1.0]])]});}
            var Q5;
            {var subQ0=sQuery(id+"F19.wireOp",EDGE,"E208");Q5=makeQuery(id+"F19.imprint","IMPRINT",FACE,{"disambiguationData":[TD([[makeQuery(id+"F19.imprint","IMPRINT",EDGE,{"derivedFrom":subQ0}),-1.0]])]});}
            var Q6;
            {var subQ0=sQuery(id+"F19.wireOp",EDGE,"E160");Q6=makeQuery(id+"F19.imprint","IMPRINT",FACE,{"disambiguationData":[TD([[makeQuery(id+"F19.imprint","IMPRINT",EDGE,{"derivedFrom":subQ0}),-1.0]])]});}
            var Q7;
            {var subQ0=sQuery(id+"F19.wireOp",EDGE,"E163");Q7=makeQuery(id+"F19.imprint","IMPRINT",FACE,{"disambiguationData":[TD([[makeQuery(id+"F19.imprint","IMPRINT",EDGE,{"derivedFrom":subQ0}),-1.0]])]});}
            extrude(context, id + "F21", {"entities" : qUnion([Q0, Q1, Q2, Q3, Q4, Q5, Q6, Q7]), "operationType" : NewBodyOperationType.REMOVE, "oppositeDirection" : true, "depth" : 10.4 * mm});
        }
        {
            var Q0;
            Q0 = qSketchRegion(id + "F19", true);
            extrude(context, id + "F22", {"entities" : qUnion([Q0]), "operationType" : NewBodyOperationType.ADD, "oppositeDirection" : true, "depth" : 2.54 * mm, "hasSecondDirection" : true, "secondDirectionOppositeDirection" : true, "secondDirectionDepth" : 1.27 * mm});
        }
        {
            var Q0;
            Q0=makeQuery(id+"F1.opExtrude","SWEPT_FACE",FACE,{"disambiguationData":[OSD([sQuery(id+"F0.wireOp",EDGE,"E3")])]});
            var sketch = newSketch(context, id + "F23", { "sketchPlane" : qUnion([Q0])});
            skLineSegment(sketch, "E285.bottom", {"start": v(149.73, 0) * mm, "end": v(194.44, 0) * mm});
            skLineSegment(sketch, "E285.top", {"start": v(149.73, 57.15) * mm, "end": v(194.44, 57.15) * mm});
            skLineSegment(sketch, "E285.left", {"start": v(149.73, 0) * mm, "end": v(149.73, 57.15) * mm});
            skLineSegment(sketch, "E285.right", {"start": v(194.44, 0) * mm, "end": v(194.44, 57.15) * mm});
            skLineSegment(sketch, "E286", {"start": v(150.5, 0) * mm, "end": v(150.5, 56.39) * mm});
            skLineSegment(sketch, "E287", {"start": v(150.5, 56.39) * mm, "end": v(193.68, 56.39) * mm});
            skLineSegment(sketch, "E288", {"start": v(193.68, 56.39) * mm, "end": v(193.68, 0) * mm});
            skLineSegment(sketch, "E289.bottom", {"start": v(152.53, 54.36) * mm, "end": v(169.93, 54.36) * mm});
            skLineSegment(sketch, "E289.top", {"start": v(152.53, 2.03) * mm, "end": v(169.93, 2.03) * mm});
            skLineSegment(sketch, "E289.left", {"start": v(152.53, 54.36) * mm, "end": v(152.53, 2.03) * mm});
            skLineSegment(sketch, "E289.right", {"start": v(169.93, 54.36) * mm, "end": v(169.93, 2.03) * mm});
            skLineSegment(sketch, "E290.bottom", {"start": v(174.24, 2.03) * mm, "end": v(191.64, 2.03) * mm});
            skLineSegment(sketch, "E290.top", {"start": v(174.24, 54.36) * mm, "end": v(191.64, 54.36) * mm});
            skLineSegment(sketch, "E290.left", {"start": v(174.24, 2.03) * mm, "end": v(174.24, 54.36) * mm});
            skLineSegment(sketch, "E290.right", {"start": v(191.64, 2.03) * mm, "end": v(191.64, 54.36) * mm});
            skLineSegment(sketch, "E291", {"start": v(171.96, 0) * mm, "end": v(171.96, 56.39) * mm});
            skLineSegment(sketch, "E292", {"start": v(172.21, 56.39) * mm, "end": v(172.21, 0) * mm});
            skLineSegment(sketch, "E293", {"start": v(161.38, 54.36) * mm, "end": v(161.38, 41.75) * mm});
            skLineSegment(sketch, "E294", {"start": v(161.38, 41.75) * mm, "end": v(152.53, 41.75) * mm});
            skLineSegment(sketch, "E295", {"start": v(162.02, 54.36) * mm, "end": v(162.02, 41.75) * mm});
            skLineSegment(sketch, "E296", {"start": v(162.02, 41.75) * mm, "end": v(169.93, 41.75) * mm});
            skLineSegment(sketch, "E297", {"start": v(169.93, 41.12) * mm, "end": v(162.02, 41.12) * mm});
            skLineSegment(sketch, "E298", {"start": v(162.02, 41.12) * mm, "end": v(162.02, 28.51) * mm});
            skLineSegment(sketch, "E299", {"start": v(162.02, 28.51) * mm, "end": v(169.93, 28.51) * mm});
            skLineSegment(sketch, "E300", {"start": v(152.53, 41.12) * mm, "end": v(161.38, 41.12) * mm});
            skLineSegment(sketch, "E301", {"start": v(161.38, 41.12) * mm, "end": v(161.38, 28.51) * mm});
            skLineSegment(sketch, "E302", {"start": v(161.38, 28.51) * mm, "end": v(152.53, 28.51) * mm});
            skLineSegment(sketch, "E303", {"start": v(182.63, 54.36) * mm, "end": v(182.63, 41.75) * mm});
            skLineSegment(sketch, "E304", {"start": v(182.63, 41.75) * mm, "end": v(174.24, 41.75) * mm});
            skLineSegment(sketch, "E305", {"start": v(183.26, 54.36) * mm, "end": v(183.26, 41.75) * mm});
            skLineSegment(sketch, "E306", {"start": v(183.26, 41.75) * mm, "end": v(191.64, 41.75) * mm});
            skLineSegment(sketch, "E307", {"start": v(191.64, 41.12) * mm, "end": v(183.26, 41.12) * mm});
            skLineSegment(sketch, "E308", {"start": v(183.26, 41.12) * mm, "end": v(183.26, 28.51) * mm});
            skLineSegment(sketch, "E309", {"start": v(183.26, 28.51) * mm, "end": v(191.64, 28.51) * mm});
            skLineSegment(sketch, "E310", {"start": v(174.24, 41.12) * mm, "end": v(182.63, 41.12) * mm});
            skLineSegment(sketch, "E311", {"start": v(182.63, 41.12) * mm, "end": v(182.63, 28.51) * mm});
            skLineSegment(sketch, "E312", {"start": v(182.63, 28.51) * mm, "end": v(174.24, 28.51) * mm});
            skLineSegment(sketch, "E313", {"start": v(182.63, 27.88) * mm, "end": v(182.63, 15.27) * mm});
            skLineSegment(sketch, "E314", {"start": v(182.63, 15.27) * mm, "end": v(174.24, 15.27) * mm});
            skLineSegment(sketch, "E315", {"start": v(174.24, 14.64) * mm, "end": v(182.63, 14.64) * mm});
            skLineSegment(sketch, "E316", {"start": v(182.63, 14.64) * mm, "end": v(182.63, 2.03) * mm});
            skLineSegment(sketch, "E317", {"start": v(183.26, 27.88) * mm, "end": v(183.26, 15.27) * mm});
            skLineSegment(sketch, "E318", {"start": v(183.26, 15.27) * mm, "end": v(191.64, 15.27) * mm});
            skLineSegment(sketch, "E319", {"start": v(191.64, 14.64) * mm, "end": v(183.26, 14.64) * mm});
            skLineSegment(sketch, "E320", {"start": v(183.26, 14.64) * mm, "end": v(183.26, 2.03) * mm});
            skLineSegment(sketch, "E321", {"start": v(169.93, 27.88) * mm, "end": v(162.02, 27.88) * mm});
            skLineSegment(sketch, "E322", {"start": v(162.02, 27.88) * mm, "end": v(162.02, 15.27) * mm});
            skLineSegment(sketch, "E323", {"start": v(162.02, 15.27) * mm, "end": v(169.93, 15.27) * mm});
            skLineSegment(sketch, "E324", {"start": v(169.93, 14.64) * mm, "end": v(162.02, 14.64) * mm});
            skLineSegment(sketch, "E325", {"start": v(162.02, 14.64) * mm, "end": v(162.02, 2.03) * mm});
            skLineSegment(sketch, "E326", {"start": v(152.53, 27.88) * mm, "end": v(161.38, 27.88) * mm});
            skLineSegment(sketch, "E327", {"start": v(161.38, 27.88) * mm, "end": v(161.38, 15.27) * mm});
            skLineSegment(sketch, "E328", {"start": v(161.38, 15.27) * mm, "end": v(152.53, 15.27) * mm});
            skLineSegment(sketch, "E329", {"start": v(152.53, 14.64) * mm, "end": v(161.38, 14.64) * mm});
            skLineSegment(sketch, "E330", {"start": v(161.38, 14.64) * mm, "end": v(161.38, 2.03) * mm});
            skLineSegment(sketch, "E331", {"start": v(174.24, 27.88) * mm, "end": v(182.63, 27.88) * mm});
            skLineSegment(sketch, "E332", {"start": v(183.26, 27.88) * mm, "end": v(191.64, 27.88) * mm});
            skSolve(sketch);
        }
        {
            var Q0;
            Q0=makeQuery(id+"F23.imprint","IMPRINT",FACE,{"disambiguationData":[TD([[makeQuery(id+"F23.imprint","IMPRINT",EDGE,{"derivedFrom":sQuery(id+"F23.wireOp",EDGE,"ec37f207-7bdc-4fa6-a789-52db764d9877.top")}),-1.0]])]});
            var Q1;
            {var subQ0=sQuery(id+"F23.wireOp",EDGE,"48c7da2d-7675-48bf-99d2-7d747f79266a");Q1=makeQuery(id+"F23.imprint","IMPRINT",FACE,{"disambiguationData":[TD([[makeQuery(id+"F23.imprint","IMPRINT",EDGE,{"derivedFrom":subQ0}),-1.0]])]});}
            var Q2;
            {var subQ20=sQuery(id+"F23.wireOp",EDGE,"1ab792e2-2677-4b89-9f5d-44a788012051");Q2=makeQuery(id+"F23.imprint","IMPRINT",FACE,{"disambiguationData":[TD([[makeQuery(id+"F23.imprint","IMPRINT",EDGE,{"derivedFrom":subQ20}),-1.0]])]});}
            var Q3;
            {var subQ19=sQuery(id+"F23.wireOp",EDGE,"af2b58b6-41da-47a7-81b6-485796316a6f");Q3=makeQuery(id+"F23.imprint","IMPRINT",FACE,{"disambiguationData":[TD([[makeQuery(id+"F23.imprint","IMPRINT",EDGE,{"derivedFrom":subQ19}),-1.0]])]});}
            var Q4;
            {var subQ3=sQuery(id+"F23.wireOp",EDGE,"E303");Q4=makeQuery(id+"F23.imprint","IMPRINT",FACE,{"disambiguationData":[TD([[makeQuery(id+"F23.imprint","IMPRINT",EDGE,{"derivedFrom":subQ3}),-1.0]])]});}
            var Q5;
            {var subQ3=sQuery(id+"F23.wireOp",EDGE,"E305");Q5=makeQuery(id+"F23.imprint","IMPRINT",FACE,{"disambiguationData":[TD([[makeQuery(id+"F23.imprint","IMPRINT",EDGE,{"derivedFrom":subQ3}),1.0]])]});}
            var Q6;
            {var subQ3=sQuery(id+"F23.wireOp",EDGE,"E295");Q6=makeQuery(id+"F23.imprint","IMPRINT",FACE,{"disambiguationData":[TD([[makeQuery(id+"F23.imprint","IMPRINT",EDGE,{"derivedFrom":subQ3}),1.0]])]});}
            var Q7;
            {var subQ3=sQuery(id+"F23.wireOp",EDGE,"E293");Q7=makeQuery(id+"F23.imprint","IMPRINT",FACE,{"disambiguationData":[TD([[makeQuery(id+"F23.imprint","IMPRINT",EDGE,{"derivedFrom":subQ3}),-1.0]])]});}
            var Q8;
            {var subQ0=sQuery(id+"F23.wireOp",EDGE,"E300");Q8=makeQuery(id+"F23.imprint","IMPRINT",FACE,{"disambiguationData":[TD([[makeQuery(id+"F23.imprint","IMPRINT",EDGE,{"derivedFrom":subQ0}),-1.0]])]});}
            var Q9;
            {var subQ0=sQuery(id+"F23.wireOp",EDGE,"E297");Q9=makeQuery(id+"F23.imprint","IMPRINT",FACE,{"disambiguationData":[TD([[makeQuery(id+"F23.imprint","IMPRINT",EDGE,{"derivedFrom":subQ0}),1.0]])]});}
            var Q10;
            {var subQ0=sQuery(id+"F23.wireOp",EDGE,"E310");Q10=makeQuery(id+"F23.imprint","IMPRINT",FACE,{"disambiguationData":[TD([[makeQuery(id+"F23.imprint","IMPRINT",EDGE,{"derivedFrom":subQ0}),-1.0]])]});}
            var Q11;
            {var subQ0=sQuery(id+"F23.wireOp",EDGE,"E307");Q11=makeQuery(id+"F23.imprint","IMPRINT",FACE,{"disambiguationData":[TD([[makeQuery(id+"F23.imprint","IMPRINT",EDGE,{"derivedFrom":subQ0}),1.0]])]});}
            var Q12;
            Q12=makeQuery(id+"F23.imprint","IMPRINT",FACE,{"disambiguationData":[TD([[makeQuery(id+"F23.imprint","IMPRINT",EDGE,{"derivedFrom":sQuery(id+"F23.wireOp",EDGE,"E317")}),1.0]])]});
            var Q13;
            Q13=makeQuery(id+"F23.imprint","IMPRINT",FACE,{"disambiguationData":[TD([[makeQuery(id+"F23.imprint","IMPRINT",EDGE,{"derivedFrom":sQuery(id+"F23.wireOp",EDGE,"E313")}),-1.0]])]});
            var Q14;
            {var subQ4=sQuery(id+"F23.wireOp",EDGE,"E319");Q14=makeQuery(id+"F23.imprint","IMPRINT",FACE,{"disambiguationData":[TD([[makeQuery(id+"F23.imprint","IMPRINT",EDGE,{"derivedFrom":subQ4}),1.0]])]});}
            var Q15;
            {var subQ4=sQuery(id+"F23.wireOp",EDGE,"E315");Q15=makeQuery(id+"F23.imprint","IMPRINT",FACE,{"disambiguationData":[TD([[makeQuery(id+"F23.imprint","IMPRINT",EDGE,{"derivedFrom":subQ4}),-1.0]])]});}
            var Q16;
            {var subQ4=sQuery(id+"F23.wireOp",EDGE,"E324");Q16=makeQuery(id+"F23.imprint","IMPRINT",FACE,{"disambiguationData":[TD([[makeQuery(id+"F23.imprint","IMPRINT",EDGE,{"derivedFrom":subQ4}),1.0]])]});}
            var Q17;
            {var subQ4=sQuery(id+"F23.wireOp",EDGE,"E329");Q17=makeQuery(id+"F23.imprint","IMPRINT",FACE,{"disambiguationData":[TD([[makeQuery(id+"F23.imprint","IMPRINT",EDGE,{"derivedFrom":subQ4}),-1.0]])]});}
            var Q18;
            {var subQ0=sQuery(id+"F23.wireOp",EDGE,"E326");Q18=makeQuery(id+"F23.imprint","IMPRINT",FACE,{"disambiguationData":[TD([[makeQuery(id+"F23.imprint","IMPRINT",EDGE,{"derivedFrom":subQ0}),-1.0]])]});}
            var Q19;
            {var subQ0=sQuery(id+"F23.wireOp",EDGE,"E321");Q19=makeQuery(id+"F23.imprint","IMPRINT",FACE,{"disambiguationData":[TD([[makeQuery(id+"F23.imprint","IMPRINT",EDGE,{"derivedFrom":subQ0}),1.0]])]});}
            var Q20;
            {var subQ9=sQuery(id+"F23.wireOp",EDGE,"E286");Q20=makeQuery(id+"F23.imprint","IMPRINT",FACE,{"disambiguationData":[TD([[makeQuery(id+"F23.imprint","IMPRINT",EDGE,{"derivedFrom":subQ9}),-1.0]])]});}
            var Q21;
            Q21=makeQuery(id+"F23.imprint","IMPRINT",FACE,{"disambiguationData":[TD([[makeQuery(id+"F23.imprint","IMPRINT",EDGE,{"derivedFrom":sQuery(id+"F23.wireOp",EDGE,"E285.top")}),-1.0]])]});
            var Q22;
            {var subQ0=sQuery(id+"F23.wireOp",EDGE,"E291");Q22=makeQuery(id+"F23.imprint","IMPRINT",FACE,{"disambiguationData":[TD([[makeQuery(id+"F23.imprint","IMPRINT",EDGE,{"derivedFrom":subQ0}),-1.0]])]});}
            var Q23;
            {var subQ23=sQuery(id+"F23.wireOp",EDGE,"E288");Q23=makeQuery(id+"F23.imprint","IMPRINT",FACE,{"disambiguationData":[TD([[makeQuery(id+"F23.imprint","IMPRINT",EDGE,{"derivedFrom":subQ23}),-1.0]])]});}
            var Q24;
            {var subQ16=sQuery(id+"F23.wireOp",EDGE,"E303");Q24=makeQuery(id+"F23.imprint","IMPRINT",FACE,{"disambiguationData":[TD([[makeQuery(id+"F23.imprint","IMPRINT",EDGE,{"derivedFrom":subQ16}),1.0]])]});}
            var Q25;
            {var subQ14=sQuery(id+"F23.wireOp",EDGE,"E293");Q25=makeQuery(id+"F23.imprint","IMPRINT",FACE,{"disambiguationData":[TD([[makeQuery(id+"F23.imprint","IMPRINT",EDGE,{"derivedFrom":subQ14}),1.0]])]});}
            extrude(context, id + "F24", {"entities" : qUnion([Q0, Q1, Q2, Q3, Q4, Q5, Q6, Q7, Q8, Q9, Q10, Q11, Q12, Q13, Q14, Q15, Q16, Q17, Q18, Q19, Q20, Q21, Q22, Q23, Q24, Q25]), "operationType" : NewBodyOperationType.REMOVE, "oppositeDirection" : true, "depth" : 4.22 * mm});
        }
        {
            var Q0;
            Q0 = qSketchRegion(id + "F23", true);
            var Q1;
            {var subQ16=sQuery(id+"F23.wireOp",EDGE,"E303");Q1=makeQuery(id+"F23.imprint","IMPRINT",FACE,{"disambiguationData":[TD([[makeQuery(id+"F23.imprint","IMPRINT",EDGE,{"derivedFrom":subQ16}),1.0]])]});}
            var Q2;
            {var subQ14=sQuery(id+"F23.wireOp",EDGE,"E293");Q2=makeQuery(id+"F23.imprint","IMPRINT",FACE,{"disambiguationData":[TD([[makeQuery(id+"F23.imprint","IMPRINT",EDGE,{"derivedFrom":subQ14}),1.0]])]});}
            extrude(context, id + "F25", {"entities" : qUnion([Q0, Q1, Q2]), "operationType" : NewBodyOperationType.ADD, "oppositeDirection" : true, "depth" : 2.54 * mm, "hasSecondDirection" : true, "secondDirectionOppositeDirection" : true, "secondDirectionDepth" : 1.27 * mm});
        }
        {
            var Q0;
            Q0=makeQuery(id+"F1.opExtrude","SWEPT_FACE",FACE,{"disambiguationData":[OSD([sQuery(id+"F0.wireOp",EDGE,"E2")])]});
            var sketch = newSketch(context, id + "F26", { "sketchPlane" : qUnion([Q0])});
            skLineSegment(sketch, "E333.bottom", {"start": v(118.27, 0) * mm, "end": v(162.98, 0) * mm});
            skLineSegment(sketch, "E333.top", {"start": v(118.27, 57.15) * mm, "end": v(162.98, 57.15) * mm});
            skLineSegment(sketch, "E333.left", {"start": v(118.27, 0) * mm, "end": v(118.27, 57.15) * mm});
            skLineSegment(sketch, "E333.right", {"start": v(162.98, 0) * mm, "end": v(162.98, 57.15) * mm});
            skLineSegment(sketch, "E334", {"start": v(119.03, 0) * mm, "end": v(119.03, 56.39) * mm});
            skLineSegment(sketch, "E335", {"start": v(119.03, 56.39) * mm, "end": v(162.21, 56.39) * mm});
            skLineSegment(sketch, "E336", {"start": v(162.21, 56.39) * mm, "end": v(162.21, 0) * mm});
            skLineSegment(sketch, "E337.bottom", {"start": v(121.07, 54.36) * mm, "end": v(138.46, 54.36) * mm});
            skLineSegment(sketch, "E337.top", {"start": v(121.07, 2.03) * mm, "end": v(138.46, 2.03) * mm});
            skLineSegment(sketch, "E337.left", {"start": v(121.07, 54.36) * mm, "end": v(121.07, 2.03) * mm});
            skLineSegment(sketch, "E337.right", {"start": v(138.46, 54.36) * mm, "end": v(138.46, 2.03) * mm});
            skLineSegment(sketch, "E338.bottom", {"start": v(142.78, 2.03) * mm, "end": v(160.18, 2.03) * mm});
            skLineSegment(sketch, "E338.top", {"start": v(142.78, 54.36) * mm, "end": v(160.18, 54.36) * mm});
            skLineSegment(sketch, "E338.left", {"start": v(142.78, 2.03) * mm, "end": v(142.78, 54.36) * mm});
            skLineSegment(sketch, "E338.right", {"start": v(160.18, 2.03) * mm, "end": v(160.18, 54.36) * mm});
            skLineSegment(sketch, "E339", {"start": v(140.5, 0) * mm, "end": v(140.5, 56.39) * mm});
            skLineSegment(sketch, "E340", {"start": v(140.75, 56.39) * mm, "end": v(140.75, 0) * mm});
            skLineSegment(sketch, "E341", {"start": v(129.92, 54.36) * mm, "end": v(129.92, 41.75) * mm});
            skLineSegment(sketch, "E342", {"start": v(129.92, 41.75) * mm, "end": v(121.07, 41.75) * mm});
            skLineSegment(sketch, "E343", {"start": v(130.56, 54.36) * mm, "end": v(130.56, 41.75) * mm});
            skLineSegment(sketch, "E344", {"start": v(130.56, 41.75) * mm, "end": v(138.46, 41.75) * mm});
            skLineSegment(sketch, "E345", {"start": v(138.46, 41.12) * mm, "end": v(130.56, 41.12) * mm});
            skLineSegment(sketch, "E346", {"start": v(130.56, 41.12) * mm, "end": v(130.56, 28.51) * mm});
            skLineSegment(sketch, "E347", {"start": v(130.56, 28.51) * mm, "end": v(138.46, 28.51) * mm});
            skLineSegment(sketch, "E348", {"start": v(121.07, 41.12) * mm, "end": v(129.92, 41.12) * mm});
            skLineSegment(sketch, "E349", {"start": v(129.92, 41.12) * mm, "end": v(129.92, 28.51) * mm});
            skLineSegment(sketch, "E350", {"start": v(129.92, 28.51) * mm, "end": v(121.07, 28.51) * mm});
            skLineSegment(sketch, "E351", {"start": v(151.16, 54.36) * mm, "end": v(151.16, 41.75) * mm});
            skLineSegment(sketch, "E352", {"start": v(151.16, 41.75) * mm, "end": v(142.78, 41.75) * mm});
            skLineSegment(sketch, "E353", {"start": v(151.8, 54.36) * mm, "end": v(151.8, 41.75) * mm});
            skLineSegment(sketch, "E354", {"start": v(151.8, 41.75) * mm, "end": v(160.18, 41.75) * mm});
            skLineSegment(sketch, "E355", {"start": v(160.18, 41.12) * mm, "end": v(151.8, 41.12) * mm});
            skLineSegment(sketch, "E356", {"start": v(151.8, 41.12) * mm, "end": v(151.8, 28.51) * mm});
            skLineSegment(sketch, "E357", {"start": v(151.8, 28.51) * mm, "end": v(160.18, 28.51) * mm});
            skLineSegment(sketch, "E358", {"start": v(142.78, 41.12) * mm, "end": v(151.16, 41.12) * mm});
            skLineSegment(sketch, "E359", {"start": v(151.16, 41.12) * mm, "end": v(151.16, 28.51) * mm});
            skLineSegment(sketch, "E360", {"start": v(151.16, 28.51) * mm, "end": v(142.78, 28.51) * mm});
            skLineSegment(sketch, "E361", {"start": v(151.16, 27.88) * mm, "end": v(151.16, 15.27) * mm});
            skLineSegment(sketch, "E362", {"start": v(151.16, 15.27) * mm, "end": v(142.78, 15.27) * mm});
            skLineSegment(sketch, "E363", {"start": v(142.78, 14.64) * mm, "end": v(151.16, 14.64) * mm});
            skLineSegment(sketch, "E364", {"start": v(151.16, 14.64) * mm, "end": v(151.16, 2.03) * mm});
            skLineSegment(sketch, "E365", {"start": v(151.8, 27.88) * mm, "end": v(151.8, 15.27) * mm});
            skLineSegment(sketch, "E366", {"start": v(151.8, 15.27) * mm, "end": v(160.18, 15.27) * mm});
            skLineSegment(sketch, "E367", {"start": v(160.18, 14.64) * mm, "end": v(151.8, 14.64) * mm});
            skLineSegment(sketch, "E368", {"start": v(151.8, 14.64) * mm, "end": v(151.8, 2.03) * mm});
            skLineSegment(sketch, "E369", {"start": v(138.46, 27.88) * mm, "end": v(130.56, 27.88) * mm});
            skLineSegment(sketch, "E370", {"start": v(130.56, 27.88) * mm, "end": v(130.56, 15.27) * mm});
            skLineSegment(sketch, "E371", {"start": v(130.56, 15.27) * mm, "end": v(138.46, 15.27) * mm});
            skLineSegment(sketch, "E372", {"start": v(138.46, 14.64) * mm, "end": v(130.56, 14.64) * mm});
            skLineSegment(sketch, "E373", {"start": v(130.56, 14.64) * mm, "end": v(130.56, 2.03) * mm});
            skLineSegment(sketch, "E374", {"start": v(121.07, 27.88) * mm, "end": v(129.92, 27.88) * mm});
            skLineSegment(sketch, "E375", {"start": v(129.92, 27.88) * mm, "end": v(129.92, 15.27) * mm});
            skLineSegment(sketch, "E376", {"start": v(129.92, 15.27) * mm, "end": v(121.07, 15.27) * mm});
            skLineSegment(sketch, "E377", {"start": v(121.07, 14.64) * mm, "end": v(129.92, 14.64) * mm});
            skLineSegment(sketch, "E378", {"start": v(129.92, 14.64) * mm, "end": v(129.92, 2.03) * mm});
            skLineSegment(sketch, "E379", {"start": v(142.78, 27.88) * mm, "end": v(151.16, 27.88) * mm});
            skLineSegment(sketch, "E380", {"start": v(151.8, 27.88) * mm, "end": v(160.18, 27.88) * mm});
            skSolve(sketch);
        }
        {
            var Q0;
            {var subQ0=sQuery(id+"F26.wireOp",EDGE,"E339");Q0=makeQuery(id+"F26.imprint","IMPRINT",FACE,{"disambiguationData":[TD([[makeQuery(id+"F26.imprint","IMPRINT",EDGE,{"derivedFrom":subQ0}),-1.0]])]});}
            var Q1;
            Q1=makeQuery(id+"F26.imprint","IMPRINT",FACE,{"disambiguationData":[TD([[makeQuery(id+"F26.imprint","IMPRINT",EDGE,{"derivedFrom":sQuery(id+"F26.wireOp",EDGE,"E333.top")}),-1.0]])]});
            var Q2;
            {var subQ21=sQuery(id+"F26.wireOp",EDGE,"E334");Q2=makeQuery(id+"F26.imprint","IMPRINT",FACE,{"disambiguationData":[TD([[makeQuery(id+"F26.imprint","IMPRINT",EDGE,{"derivedFrom":subQ21}),-1.0]])]});}
            var Q3;
            {var subQ3=sQuery(id+"F26.wireOp",EDGE,"E341");Q3=makeQuery(id+"F26.imprint","IMPRINT",FACE,{"disambiguationData":[TD([[makeQuery(id+"F26.imprint","IMPRINT",EDGE,{"derivedFrom":subQ3}),-1.0]])]});}
            var Q4;
            {var subQ3=sQuery(id+"F26.wireOp",EDGE,"E343");Q4=makeQuery(id+"F26.imprint","IMPRINT",FACE,{"disambiguationData":[TD([[makeQuery(id+"F26.imprint","IMPRINT",EDGE,{"derivedFrom":subQ3}),1.0]])]});}
            var Q5;
            {var subQ12=sQuery(id+"F26.wireOp",EDGE,"E341");Q5=makeQuery(id+"F26.imprint","IMPRINT",FACE,{"disambiguationData":[TD([[makeQuery(id+"F26.imprint","IMPRINT",EDGE,{"derivedFrom":subQ12}),1.0]])]});}
            var Q6;
            {var subQ3=sQuery(id+"F26.wireOp",EDGE,"E351");Q6=makeQuery(id+"F26.imprint","IMPRINT",FACE,{"disambiguationData":[TD([[makeQuery(id+"F26.imprint","IMPRINT",EDGE,{"derivedFrom":subQ3}),-1.0]])]});}
            var Q7;
            {var subQ3=sQuery(id+"F26.wireOp",EDGE,"E353");Q7=makeQuery(id+"F26.imprint","IMPRINT",FACE,{"disambiguationData":[TD([[makeQuery(id+"F26.imprint","IMPRINT",EDGE,{"derivedFrom":subQ3}),1.0]])]});}
            var Q8;
            {var subQ11=sQuery(id+"F26.wireOp",EDGE,"E351");Q8=makeQuery(id+"F26.imprint","IMPRINT",FACE,{"disambiguationData":[TD([[makeQuery(id+"F26.imprint","IMPRINT",EDGE,{"derivedFrom":subQ11}),1.0]])]});}
            var Q9;
            {var subQ0=sQuery(id+"F26.wireOp",EDGE,"E355");Q9=makeQuery(id+"F26.imprint","IMPRINT",FACE,{"disambiguationData":[TD([[makeQuery(id+"F26.imprint","IMPRINT",EDGE,{"derivedFrom":subQ0}),1.0]])]});}
            var Q10;
            {var subQ0=sQuery(id+"F26.wireOp",EDGE,"E358");Q10=makeQuery(id+"F26.imprint","IMPRINT",FACE,{"disambiguationData":[TD([[makeQuery(id+"F26.imprint","IMPRINT",EDGE,{"derivedFrom":subQ0}),-1.0]])]});}
            var Q11;
            {var subQ0=sQuery(id+"F26.wireOp",EDGE,"E345");Q11=makeQuery(id+"F26.imprint","IMPRINT",FACE,{"disambiguationData":[TD([[makeQuery(id+"F26.imprint","IMPRINT",EDGE,{"derivedFrom":subQ0}),1.0]])]});}
            var Q12;
            {var subQ0=sQuery(id+"F26.wireOp",EDGE,"E348");Q12=makeQuery(id+"F26.imprint","IMPRINT",FACE,{"disambiguationData":[TD([[makeQuery(id+"F26.imprint","IMPRINT",EDGE,{"derivedFrom":subQ0}),-1.0]])]});}
            var Q13;
            Q13=makeQuery(id+"F26.imprint","IMPRINT",FACE,{"disambiguationData":[TD([[makeQuery(id+"F26.imprint","IMPRINT",EDGE,{"derivedFrom":sQuery(id+"F26.wireOp",EDGE,"E365")}),1.0]])]});
            var Q14;
            Q14=makeQuery(id+"F26.imprint","IMPRINT",FACE,{"disambiguationData":[TD([[makeQuery(id+"F26.imprint","IMPRINT",EDGE,{"derivedFrom":sQuery(id+"F26.wireOp",EDGE,"E361")}),-1.0]])]});
            var Q15;
            {var subQ0=sQuery(id+"F26.wireOp",EDGE,"E369");Q15=makeQuery(id+"F26.imprint","IMPRINT",FACE,{"disambiguationData":[TD([[makeQuery(id+"F26.imprint","IMPRINT",EDGE,{"derivedFrom":subQ0}),1.0]])]});}
            var Q16;
            {var subQ0=sQuery(id+"F26.wireOp",EDGE,"E374");Q16=makeQuery(id+"F26.imprint","IMPRINT",FACE,{"disambiguationData":[TD([[makeQuery(id+"F26.imprint","IMPRINT",EDGE,{"derivedFrom":subQ0}),-1.0]])]});}
            var Q17;
            {var subQ4=sQuery(id+"F26.wireOp",EDGE,"E377");Q17=makeQuery(id+"F26.imprint","IMPRINT",FACE,{"disambiguationData":[TD([[makeQuery(id+"F26.imprint","IMPRINT",EDGE,{"derivedFrom":subQ4}),-1.0]])]});}
            var Q18;
            {var subQ4=sQuery(id+"F26.wireOp",EDGE,"E372");Q18=makeQuery(id+"F26.imprint","IMPRINT",FACE,{"disambiguationData":[TD([[makeQuery(id+"F26.imprint","IMPRINT",EDGE,{"derivedFrom":subQ4}),1.0]])]});}
            var Q19;
            {var subQ4=sQuery(id+"F26.wireOp",EDGE,"E363");Q19=makeQuery(id+"F26.imprint","IMPRINT",FACE,{"disambiguationData":[TD([[makeQuery(id+"F26.imprint","IMPRINT",EDGE,{"derivedFrom":subQ4}),-1.0]])]});}
            var Q20;
            {var subQ4=sQuery(id+"F26.wireOp",EDGE,"E367");Q20=makeQuery(id+"F26.imprint","IMPRINT",FACE,{"disambiguationData":[TD([[makeQuery(id+"F26.imprint","IMPRINT",EDGE,{"derivedFrom":subQ4}),1.0]])]});}
            var Q21;
            {var subQ5=sQuery(id+"F26.wireOp",EDGE,"E336");Q21=makeQuery(id+"F26.imprint","IMPRINT",FACE,{"disambiguationData":[TD([[makeQuery(id+"F26.imprint","IMPRINT",EDGE,{"derivedFrom":subQ5}),-1.0]])]});}
            extrude(context, id + "F27", {"entities" : qUnion([Q0, Q1, Q2, Q3, Q4, Q5, Q6, Q7, Q8, Q9, Q10, Q11, Q12, Q13, Q14, Q15, Q16, Q17, Q18, Q19, Q20, Q21]), "operationType" : NewBodyOperationType.REMOVE, "oppositeDirection" : true, "depth" : 4.22 * mm});
        }
        {
            var Q0;
            Q0 = qSketchRegion(id + "F26", true);
            var Q1;
            {var subQ12=sQuery(id+"F26.wireOp",EDGE,"E341");Q1=makeQuery(id+"F26.imprint","IMPRINT",FACE,{"disambiguationData":[TD([[makeQuery(id+"F26.imprint","IMPRINT",EDGE,{"derivedFrom":subQ12}),1.0]])]});}
            var Q2;
            {var subQ11=sQuery(id+"F26.wireOp",EDGE,"E351");Q2=makeQuery(id+"F26.imprint","IMPRINT",FACE,{"disambiguationData":[TD([[makeQuery(id+"F26.imprint","IMPRINT",EDGE,{"derivedFrom":subQ11}),1.0]])]});}
            extrude(context, id + "F28", {"entities" : qUnion([Q0, Q1, Q2]), "operationType" : NewBodyOperationType.ADD, "oppositeDirection" : true, "depth" : 2.54 * mm, "hasSecondDirection" : true, "secondDirectionOppositeDirection" : true, "secondDirectionDepth" : 1.27 * mm});
        }
        {
            var Q0;
            Q0=makeQuery(id+"F1.opExtrude","SWEPT_FACE",FACE,{"disambiguationData":[OSD([sQuery(id+"F0.wireOp",EDGE,"E1")])]});
            var sketch = newSketch(context, id + "F29", { "sketchPlane" : qUnion([Q0])});
            skLineSegment(sketch, "E381.bottom", {"start": v(1.78, 0) * mm, "end": v(46.49, 0) * mm});
            skLineSegment(sketch, "E381.top", {"start": v(1.78, 57.15) * mm, "end": v(46.49, 57.15) * mm});
            skLineSegment(sketch, "E381.left", {"start": v(1.78, 0) * mm, "end": v(1.78, 57.15) * mm});
            skLineSegment(sketch, "E381.right", {"start": v(46.49, 0) * mm, "end": v(46.49, 57.15) * mm});
            skLineSegment(sketch, "E382", {"start": v(2.54, 0) * mm, "end": v(2.54, 56.39) * mm});
            skLineSegment(sketch, "E383", {"start": v(2.54, 56.39) * mm, "end": v(45.72, 56.39) * mm});
            skLineSegment(sketch, "E384", {"start": v(45.72, 56.39) * mm, "end": v(45.72, 0) * mm});
            skLineSegment(sketch, "E385.bottom", {"start": v(4.58, 54.36) * mm, "end": v(21.98, 54.36) * mm});
            skLineSegment(sketch, "E385.top", {"start": v(4.58, 2.03) * mm, "end": v(21.98, 2.03) * mm});
            skLineSegment(sketch, "E385.left", {"start": v(4.58, 54.36) * mm, "end": v(4.58, 2.03) * mm});
            skLineSegment(sketch, "E385.right", {"start": v(21.98, 54.36) * mm, "end": v(21.98, 2.03) * mm});
            skLineSegment(sketch, "E386.bottom", {"start": v(26.3, 2.03) * mm, "end": v(43.7, 2.03) * mm});
            skLineSegment(sketch, "E386.top", {"start": v(26.3, 54.36) * mm, "end": v(43.7, 54.36) * mm});
            skLineSegment(sketch, "E386.left", {"start": v(26.3, 2.03) * mm, "end": v(26.3, 54.36) * mm});
            skLineSegment(sketch, "E386.right", {"start": v(43.7, 2.03) * mm, "end": v(43.7, 54.36) * mm});
            skLineSegment(sketch, "E387", {"start": v(24, 0) * mm, "end": v(24, 56.39) * mm});
            skLineSegment(sketch, "E388", {"start": v(24.26, 56.39) * mm, "end": v(24.26, 0) * mm});
            skLineSegment(sketch, "E389", {"start": v(13.43, 54.36) * mm, "end": v(13.43, 41.75) * mm});
            skLineSegment(sketch, "E390", {"start": v(13.43, 41.75) * mm, "end": v(4.58, 41.75) * mm});
            skLineSegment(sketch, "E391", {"start": v(14.07, 54.36) * mm, "end": v(14.07, 41.75) * mm});
            skLineSegment(sketch, "E392", {"start": v(14.07, 41.75) * mm, "end": v(21.98, 41.75) * mm});
            skLineSegment(sketch, "E393", {"start": v(21.98, 41.12) * mm, "end": v(14.07, 41.12) * mm});
            skLineSegment(sketch, "E394", {"start": v(14.07, 41.12) * mm, "end": v(14.07, 28.51) * mm});
            skLineSegment(sketch, "E395", {"start": v(14.07, 28.51) * mm, "end": v(21.98, 28.51) * mm});
            skLineSegment(sketch, "E396", {"start": v(4.58, 41.12) * mm, "end": v(13.43, 41.12) * mm});
            skLineSegment(sketch, "E397", {"start": v(13.43, 41.12) * mm, "end": v(13.43, 28.51) * mm});
            skLineSegment(sketch, "E398", {"start": v(13.43, 28.51) * mm, "end": v(4.58, 28.51) * mm});
            skLineSegment(sketch, "E399", {"start": v(34.68, 54.36) * mm, "end": v(34.68, 41.75) * mm});
            skLineSegment(sketch, "E400", {"start": v(34.68, 41.75) * mm, "end": v(26.3, 41.75) * mm});
            skLineSegment(sketch, "E401", {"start": v(35.31, 54.36) * mm, "end": v(35.31, 41.75) * mm});
            skLineSegment(sketch, "E402", {"start": v(35.31, 41.75) * mm, "end": v(43.7, 41.75) * mm});
            skLineSegment(sketch, "E403", {"start": v(43.7, 41.12) * mm, "end": v(35.31, 41.12) * mm});
            skLineSegment(sketch, "E404", {"start": v(35.31, 41.12) * mm, "end": v(35.31, 28.51) * mm});
            skLineSegment(sketch, "E405", {"start": v(35.31, 28.51) * mm, "end": v(43.7, 28.51) * mm});
            skLineSegment(sketch, "E406", {"start": v(26.3, 41.12) * mm, "end": v(34.68, 41.12) * mm});
            skLineSegment(sketch, "E407", {"start": v(34.68, 41.12) * mm, "end": v(34.68, 28.51) * mm});
            skLineSegment(sketch, "E408", {"start": v(34.68, 28.51) * mm, "end": v(26.3, 28.51) * mm});
            skLineSegment(sketch, "E409", {"start": v(34.68, 27.88) * mm, "end": v(34.68, 15.27) * mm});
            skLineSegment(sketch, "E410", {"start": v(34.68, 15.27) * mm, "end": v(26.3, 15.27) * mm});
            skLineSegment(sketch, "E411", {"start": v(26.3, 14.64) * mm, "end": v(34.68, 14.64) * mm});
            skLineSegment(sketch, "E412", {"start": v(34.68, 14.64) * mm, "end": v(34.68, 2.03) * mm});
            skLineSegment(sketch, "E413", {"start": v(35.31, 27.88) * mm, "end": v(35.31, 15.27) * mm});
            skLineSegment(sketch, "E414", {"start": v(35.31, 15.27) * mm, "end": v(43.7, 15.27) * mm});
            skLineSegment(sketch, "E415", {"start": v(43.7, 14.64) * mm, "end": v(35.31, 14.64) * mm});
            skLineSegment(sketch, "E416", {"start": v(35.31, 14.64) * mm, "end": v(35.31, 2.03) * mm});
            skLineSegment(sketch, "E417", {"start": v(21.98, 27.88) * mm, "end": v(14.07, 27.88) * mm});
            skLineSegment(sketch, "E418", {"start": v(14.07, 27.88) * mm, "end": v(14.07, 15.27) * mm});
            skLineSegment(sketch, "E419", {"start": v(14.07, 15.27) * mm, "end": v(21.98, 15.27) * mm});
            skLineSegment(sketch, "E420", {"start": v(21.98, 14.64) * mm, "end": v(14.07, 14.64) * mm});
            skLineSegment(sketch, "E421", {"start": v(14.07, 14.64) * mm, "end": v(14.07, 2.03) * mm});
            skLineSegment(sketch, "E422", {"start": v(4.58, 27.88) * mm, "end": v(13.43, 27.88) * mm});
            skLineSegment(sketch, "E423", {"start": v(13.43, 27.88) * mm, "end": v(13.43, 15.27) * mm});
            skLineSegment(sketch, "E424", {"start": v(13.43, 15.27) * mm, "end": v(4.58, 15.27) * mm});
            skLineSegment(sketch, "E425", {"start": v(4.58, 14.64) * mm, "end": v(13.43, 14.64) * mm});
            skLineSegment(sketch, "E426", {"start": v(13.43, 14.64) * mm, "end": v(13.43, 2.03) * mm});
            skLineSegment(sketch, "E427", {"start": v(26.3, 27.88) * mm, "end": v(34.68, 27.88) * mm});
            skLineSegment(sketch, "E428", {"start": v(35.31, 27.88) * mm, "end": v(43.7, 27.88) * mm});
            skSolve(sketch);
        }
        {
            var Q0;
            Q0 = qSketchRegion(id + "F29", true);
            var Q1;
            {var subQ3=sQuery(id+"F29.wireOp",EDGE,"E389");Q1=makeQuery(id+"F29.imprint","IMPRINT",FACE,{"disambiguationData":[TD([[makeQuery(id+"F29.imprint","IMPRINT",EDGE,{"derivedFrom":subQ3}),-1.0]])]});}
            var Q2;
            {var subQ18=sQuery(id+"F29.wireOp",EDGE,"E389");Q2=makeQuery(id+"F29.imprint","IMPRINT",FACE,{"disambiguationData":[TD([[makeQuery(id+"F29.imprint","IMPRINT",EDGE,{"derivedFrom":subQ18}),1.0]])]});}
            var Q3;
            {var subQ3=sQuery(id+"F29.wireOp",EDGE,"E391");Q3=makeQuery(id+"F29.imprint","IMPRINT",FACE,{"disambiguationData":[TD([[makeQuery(id+"F29.imprint","IMPRINT",EDGE,{"derivedFrom":subQ3}),1.0]])]});}
            var Q4;
            {var subQ0=sQuery(id+"F29.wireOp",EDGE,"E393");Q4=makeQuery(id+"F29.imprint","IMPRINT",FACE,{"disambiguationData":[TD([[makeQuery(id+"F29.imprint","IMPRINT",EDGE,{"derivedFrom":subQ0}),1.0]])]});}
            var Q5;
            {var subQ0=sQuery(id+"F29.wireOp",EDGE,"E396");Q5=makeQuery(id+"F29.imprint","IMPRINT",FACE,{"disambiguationData":[TD([[makeQuery(id+"F29.imprint","IMPRINT",EDGE,{"derivedFrom":subQ0}),-1.0]])]});}
            var Q6;
            {var subQ0=sQuery(id+"F29.wireOp",EDGE,"E422");Q6=makeQuery(id+"F29.imprint","IMPRINT",FACE,{"disambiguationData":[TD([[makeQuery(id+"F29.imprint","IMPRINT",EDGE,{"derivedFrom":subQ0}),-1.0]])]});}
            var Q7;
            {var subQ0=sQuery(id+"F29.wireOp",EDGE,"E417");Q7=makeQuery(id+"F29.imprint","IMPRINT",FACE,{"disambiguationData":[TD([[makeQuery(id+"F29.imprint","IMPRINT",EDGE,{"derivedFrom":subQ0}),1.0]])]});}
            var Q8;
            {var subQ4=sQuery(id+"F29.wireOp",EDGE,"E420");Q8=makeQuery(id+"F29.imprint","IMPRINT",FACE,{"disambiguationData":[TD([[makeQuery(id+"F29.imprint","IMPRINT",EDGE,{"derivedFrom":subQ4}),1.0]])]});}
            var Q9;
            {var subQ4=sQuery(id+"F29.wireOp",EDGE,"E425");Q9=makeQuery(id+"F29.imprint","IMPRINT",FACE,{"disambiguationData":[TD([[makeQuery(id+"F29.imprint","IMPRINT",EDGE,{"derivedFrom":subQ4}),-1.0]])]});}
            var Q10;
            {var subQ3=sQuery(id+"F29.wireOp",EDGE,"E399");Q10=makeQuery(id+"F29.imprint","IMPRINT",FACE,{"disambiguationData":[TD([[makeQuery(id+"F29.imprint","IMPRINT",EDGE,{"derivedFrom":subQ3}),-1.0]])]});}
            var Q11;
            {var subQ13=sQuery(id+"F29.wireOp",EDGE,"E399");Q11=makeQuery(id+"F29.imprint","IMPRINT",FACE,{"disambiguationData":[TD([[makeQuery(id+"F29.imprint","IMPRINT",EDGE,{"derivedFrom":subQ13}),1.0]])]});}
            var Q12;
            {var subQ3=sQuery(id+"F29.wireOp",EDGE,"E401");Q12=makeQuery(id+"F29.imprint","IMPRINT",FACE,{"disambiguationData":[TD([[makeQuery(id+"F29.imprint","IMPRINT",EDGE,{"derivedFrom":subQ3}),1.0]])]});}
            var Q13;
            {var subQ0=sQuery(id+"F29.wireOp",EDGE,"E403");Q13=makeQuery(id+"F29.imprint","IMPRINT",FACE,{"disambiguationData":[TD([[makeQuery(id+"F29.imprint","IMPRINT",EDGE,{"derivedFrom":subQ0}),1.0]])]});}
            var Q14;
            {var subQ0=sQuery(id+"F29.wireOp",EDGE,"E406");Q14=makeQuery(id+"F29.imprint","IMPRINT",FACE,{"disambiguationData":[TD([[makeQuery(id+"F29.imprint","IMPRINT",EDGE,{"derivedFrom":subQ0}),-1.0]])]});}
            var Q15;
            Q15=makeQuery(id+"F29.imprint","IMPRINT",FACE,{"disambiguationData":[TD([[makeQuery(id+"F29.imprint","IMPRINT",EDGE,{"derivedFrom":sQuery(id+"F29.wireOp",EDGE,"E409")}),-1.0]])]});
            var Q16;
            Q16=makeQuery(id+"F29.imprint","IMPRINT",FACE,{"disambiguationData":[TD([[makeQuery(id+"F29.imprint","IMPRINT",EDGE,{"derivedFrom":sQuery(id+"F29.wireOp",EDGE,"E413")}),1.0]])]});
            var Q17;
            {var subQ4=sQuery(id+"F29.wireOp",EDGE,"E415");Q17=makeQuery(id+"F29.imprint","IMPRINT",FACE,{"disambiguationData":[TD([[makeQuery(id+"F29.imprint","IMPRINT",EDGE,{"derivedFrom":subQ4}),1.0]])]});}
            var Q18;
            {var subQ4=sQuery(id+"F29.wireOp",EDGE,"E411");Q18=makeQuery(id+"F29.imprint","IMPRINT",FACE,{"disambiguationData":[TD([[makeQuery(id+"F29.imprint","IMPRINT",EDGE,{"derivedFrom":subQ4}),-1.0]])]});}
            extrude(context, id + "F30", {"entities" : qUnion([Q0, Q1, Q2, Q3, Q4, Q5, Q6, Q7, Q8, Q9, Q10, Q11, Q12, Q13, Q14, Q15, Q16, Q17, Q18]), "operationType" : NewBodyOperationType.REMOVE, "oppositeDirection" : true, "depth" : 4.22 * mm});
        }
        {
            var Q0;
            Q0 = qSketchRegion(id + "F29", true);
            var Q1;
            {var subQ18=sQuery(id+"F29.wireOp",EDGE,"E389");Q1=makeQuery(id+"F29.imprint","IMPRINT",FACE,{"disambiguationData":[TD([[makeQuery(id+"F29.imprint","IMPRINT",EDGE,{"derivedFrom":subQ18}),1.0]])]});}
            var Q2;
            {var subQ13=sQuery(id+"F29.wireOp",EDGE,"E399");Q2=makeQuery(id+"F29.imprint","IMPRINT",FACE,{"disambiguationData":[TD([[makeQuery(id+"F29.imprint","IMPRINT",EDGE,{"derivedFrom":subQ13}),1.0]])]});}
            extrude(context, id + "F31", {"entities" : qUnion([Q0, Q1, Q2]), "operationType" : NewBodyOperationType.ADD, "oppositeDirection" : true, "depth" : 2.54 * mm, "hasSecondDirection" : true, "secondDirectionOppositeDirection" : true, "secondDirectionDepth" : 1.27 * mm});
        }
        {
            var Q0;
            Q0=makeQuery(id+"F1.opExtrude","SWEPT_FACE",FACE,{"disambiguationData":[OSD([sQuery(id+"F0.wireOp",EDGE,"E4")])]});
            var sketch = newSketch(context, id + "F32", { "sketchPlane" : qUnion([Q0])});
            skLineSegment(sketch, "E429.bottom", {"start": v(117.72, 0) * mm, "end": v(162.42, 0) * mm});
            skLineSegment(sketch, "E429.top", {"start": v(117.72, 57.15) * mm, "end": v(162.42, 57.15) * mm});
            skLineSegment(sketch, "E429.left", {"start": v(117.72, 0) * mm, "end": v(117.72, 57.15) * mm});
            skLineSegment(sketch, "E429.right", {"start": v(162.42, 0) * mm, "end": v(162.42, 57.15) * mm});
            skLineSegment(sketch, "E430", {"start": v(118.48, 0) * mm, "end": v(118.48, 56.39) * mm});
            skLineSegment(sketch, "E431", {"start": v(118.48, 56.39) * mm, "end": v(161.66, 56.39) * mm});
            skLineSegment(sketch, "E432", {"start": v(161.66, 56.39) * mm, "end": v(161.66, 0) * mm});
            skLineSegment(sketch, "E433.bottom", {"start": v(120.5, 54.36) * mm, "end": v(137.9, 54.36) * mm});
            skLineSegment(sketch, "E433.top", {"start": v(120.5, 2.03) * mm, "end": v(137.9, 2.03) * mm});
            skLineSegment(sketch, "E433.left", {"start": v(120.5, 54.36) * mm, "end": v(120.5, 2.03) * mm});
            skLineSegment(sketch, "E433.right", {"start": v(137.9, 54.36) * mm, "end": v(137.9, 2.03) * mm});
            skLineSegment(sketch, "E434.bottom", {"start": v(142.23, 2.03) * mm, "end": v(159.63, 2.03) * mm});
            skLineSegment(sketch, "E434.top", {"start": v(142.23, 54.36) * mm, "end": v(159.63, 54.36) * mm});
            skLineSegment(sketch, "E434.left", {"start": v(142.23, 2.03) * mm, "end": v(142.23, 54.36) * mm});
            skLineSegment(sketch, "E434.right", {"start": v(159.63, 2.03) * mm, "end": v(159.63, 54.36) * mm});
            skLineSegment(sketch, "E435", {"start": v(139.94, 0) * mm, "end": v(139.94, 56.39) * mm});
            skLineSegment(sketch, "E436", {"start": v(140.2, 56.39) * mm, "end": v(140.2, 0) * mm});
            skLineSegment(sketch, "E437", {"start": v(129.37, 54.36) * mm, "end": v(129.37, 41.75) * mm});
            skLineSegment(sketch, "E438", {"start": v(129.37, 41.75) * mm, "end": v(120.5, 41.75) * mm});
            skLineSegment(sketch, "E439", {"start": v(130, 54.36) * mm, "end": v(130, 41.75) * mm});
            skLineSegment(sketch, "E440", {"start": v(130, 41.75) * mm, "end": v(137.9, 41.75) * mm});
            skLineSegment(sketch, "E441", {"start": v(137.9, 41.12) * mm, "end": v(130, 41.12) * mm});
            skLineSegment(sketch, "E442", {"start": v(130, 41.12) * mm, "end": v(130, 28.51) * mm});
            skLineSegment(sketch, "E443", {"start": v(130, 28.51) * mm, "end": v(137.9, 28.51) * mm});
            skLineSegment(sketch, "E444", {"start": v(120.5, 41.12) * mm, "end": v(129.37, 41.12) * mm});
            skLineSegment(sketch, "E445", {"start": v(129.37, 41.12) * mm, "end": v(129.37, 28.51) * mm});
            skLineSegment(sketch, "E446", {"start": v(129.37, 28.51) * mm, "end": v(120.5, 28.51) * mm});
            skLineSegment(sketch, "E447", {"start": v(150.6, 54.36) * mm, "end": v(150.6, 41.75) * mm});
            skLineSegment(sketch, "E448", {"start": v(150.6, 41.75) * mm, "end": v(142.23, 41.75) * mm});
            skLineSegment(sketch, "E449", {"start": v(151.24, 54.36) * mm, "end": v(151.24, 41.75) * mm});
            skLineSegment(sketch, "E450", {"start": v(151.24, 41.75) * mm, "end": v(159.63, 41.75) * mm});
            skLineSegment(sketch, "E451", {"start": v(159.63, 41.12) * mm, "end": v(151.24, 41.12) * mm});
            skLineSegment(sketch, "E452", {"start": v(151.24, 41.12) * mm, "end": v(151.24, 28.51) * mm});
            skLineSegment(sketch, "E453", {"start": v(151.24, 28.51) * mm, "end": v(159.63, 28.51) * mm});
            skLineSegment(sketch, "E454", {"start": v(142.23, 41.12) * mm, "end": v(150.6, 41.12) * mm});
            skLineSegment(sketch, "E455", {"start": v(150.6, 41.12) * mm, "end": v(150.6, 28.51) * mm});
            skLineSegment(sketch, "E456", {"start": v(150.6, 28.51) * mm, "end": v(142.23, 28.51) * mm});
            skLineSegment(sketch, "E457", {"start": v(150.6, 27.88) * mm, "end": v(150.6, 15.27) * mm});
            skLineSegment(sketch, "E458", {"start": v(150.6, 15.27) * mm, "end": v(142.23, 15.27) * mm});
            skLineSegment(sketch, "E459", {"start": v(142.23, 14.64) * mm, "end": v(150.6, 14.64) * mm});
            skLineSegment(sketch, "E460", {"start": v(150.6, 14.64) * mm, "end": v(150.6, 2.03) * mm});
            skLineSegment(sketch, "E461", {"start": v(151.24, 27.88) * mm, "end": v(151.24, 15.27) * mm});
            skLineSegment(sketch, "E462", {"start": v(151.24, 15.27) * mm, "end": v(159.63, 15.27) * mm});
            skLineSegment(sketch, "E463", {"start": v(159.63, 14.64) * mm, "end": v(151.24, 14.64) * mm});
            skLineSegment(sketch, "E464", {"start": v(151.24, 14.64) * mm, "end": v(151.24, 2.03) * mm});
            skLineSegment(sketch, "E465", {"start": v(137.9, 27.88) * mm, "end": v(130, 27.88) * mm});
            skLineSegment(sketch, "E466", {"start": v(130, 27.88) * mm, "end": v(130, 15.27) * mm});
            skLineSegment(sketch, "E467", {"start": v(130, 15.27) * mm, "end": v(137.9, 15.27) * mm});
            skLineSegment(sketch, "E468", {"start": v(137.9, 14.64) * mm, "end": v(130, 14.64) * mm});
            skLineSegment(sketch, "E469", {"start": v(130, 14.64) * mm, "end": v(130, 2.03) * mm});
            skLineSegment(sketch, "E470", {"start": v(120.5, 27.88) * mm, "end": v(129.37, 27.88) * mm});
            skLineSegment(sketch, "E471", {"start": v(129.37, 27.88) * mm, "end": v(129.37, 15.27) * mm});
            skLineSegment(sketch, "E472", {"start": v(129.37, 15.27) * mm, "end": v(120.5, 15.27) * mm});
            skLineSegment(sketch, "E473", {"start": v(120.5, 14.64) * mm, "end": v(129.37, 14.64) * mm});
            skLineSegment(sketch, "E474", {"start": v(129.37, 14.64) * mm, "end": v(129.37, 2.03) * mm});
            skLineSegment(sketch, "E475", {"start": v(142.23, 27.88) * mm, "end": v(150.6, 27.88) * mm});
            skLineSegment(sketch, "E476", {"start": v(151.24, 27.88) * mm, "end": v(159.63, 27.88) * mm});
            skSolve(sketch);
        }
        {
            var Q0;
            Q0 = qSketchRegion(id + "F32", true);
            var Q1;
            {var subQ3=sQuery(id+"F32.wireOp",EDGE,"E437");Q1=makeQuery(id+"F32.imprint","IMPRINT",FACE,{"disambiguationData":[TD([[makeQuery(id+"F32.imprint","IMPRINT",EDGE,{"derivedFrom":subQ3}),-1.0]])]});}
            var Q2;
            {var subQ3=sQuery(id+"F32.wireOp",EDGE,"E439");Q2=makeQuery(id+"F32.imprint","IMPRINT",FACE,{"disambiguationData":[TD([[makeQuery(id+"F32.imprint","IMPRINT",EDGE,{"derivedFrom":subQ3}),1.0]])]});}
            var Q3;
            {var subQ3=sQuery(id+"F32.wireOp",EDGE,"E447");Q3=makeQuery(id+"F32.imprint","IMPRINT",FACE,{"disambiguationData":[TD([[makeQuery(id+"F32.imprint","IMPRINT",EDGE,{"derivedFrom":subQ3}),-1.0]])]});}
            var Q4;
            {var subQ12=sQuery(id+"F32.wireOp",EDGE,"E447");Q4=makeQuery(id+"F32.imprint","IMPRINT",FACE,{"disambiguationData":[TD([[makeQuery(id+"F32.imprint","IMPRINT",EDGE,{"derivedFrom":subQ12}),1.0]])]});}
            var Q5;
            {var subQ3=sQuery(id+"F32.wireOp",EDGE,"E449");Q5=makeQuery(id+"F32.imprint","IMPRINT",FACE,{"disambiguationData":[TD([[makeQuery(id+"F32.imprint","IMPRINT",EDGE,{"derivedFrom":subQ3}),1.0]])]});}
            var Q6;
            {var subQ0=sQuery(id+"F32.wireOp",EDGE,"E451");Q6=makeQuery(id+"F32.imprint","IMPRINT",FACE,{"disambiguationData":[TD([[makeQuery(id+"F32.imprint","IMPRINT",EDGE,{"derivedFrom":subQ0}),1.0]])]});}
            var Q7;
            {var subQ0=sQuery(id+"F32.wireOp",EDGE,"E454");Q7=makeQuery(id+"F32.imprint","IMPRINT",FACE,{"disambiguationData":[TD([[makeQuery(id+"F32.imprint","IMPRINT",EDGE,{"derivedFrom":subQ0}),-1.0]])]});}
            var Q8;
            {var subQ0=sQuery(id+"F32.wireOp",EDGE,"E444");Q8=makeQuery(id+"F32.imprint","IMPRINT",FACE,{"disambiguationData":[TD([[makeQuery(id+"F32.imprint","IMPRINT",EDGE,{"derivedFrom":subQ0}),-1.0]])]});}
            var Q9;
            {var subQ0=sQuery(id+"F32.wireOp",EDGE,"E441");Q9=makeQuery(id+"F32.imprint","IMPRINT",FACE,{"disambiguationData":[TD([[makeQuery(id+"F32.imprint","IMPRINT",EDGE,{"derivedFrom":subQ0}),1.0]])]});}
            var Q10;
            {var subQ0=sQuery(id+"F32.wireOp",EDGE,"E470");Q10=makeQuery(id+"F32.imprint","IMPRINT",FACE,{"disambiguationData":[TD([[makeQuery(id+"F32.imprint","IMPRINT",EDGE,{"derivedFrom":subQ0}),-1.0]])]});}
            var Q11;
            {var subQ0=sQuery(id+"F32.wireOp",EDGE,"E465");Q11=makeQuery(id+"F32.imprint","IMPRINT",FACE,{"disambiguationData":[TD([[makeQuery(id+"F32.imprint","IMPRINT",EDGE,{"derivedFrom":subQ0}),1.0]])]});}
            var Q12;
            {var subQ7=sQuery(id+"F32.wireOp",EDGE,"E437");Q12=makeQuery(id+"F32.imprint","IMPRINT",FACE,{"disambiguationData":[TD([[makeQuery(id+"F32.imprint","IMPRINT",EDGE,{"derivedFrom":subQ7}),1.0]])]});}
            var Q13;
            Q13=makeQuery(id+"F32.imprint","IMPRINT",FACE,{"disambiguationData":[TD([[makeQuery(id+"F32.imprint","IMPRINT",EDGE,{"derivedFrom":sQuery(id+"F32.wireOp",EDGE,"E457")}),-1.0]])]});
            var Q14;
            Q14=makeQuery(id+"F32.imprint","IMPRINT",FACE,{"disambiguationData":[TD([[makeQuery(id+"F32.imprint","IMPRINT",EDGE,{"derivedFrom":sQuery(id+"F32.wireOp",EDGE,"E461")}),1.0]])]});
            var Q15;
            {var subQ4=sQuery(id+"F32.wireOp",EDGE,"E463");Q15=makeQuery(id+"F32.imprint","IMPRINT",FACE,{"disambiguationData":[TD([[makeQuery(id+"F32.imprint","IMPRINT",EDGE,{"derivedFrom":subQ4}),1.0]])]});}
            var Q16;
            {var subQ4=sQuery(id+"F32.wireOp",EDGE,"E459");Q16=makeQuery(id+"F32.imprint","IMPRINT",FACE,{"disambiguationData":[TD([[makeQuery(id+"F32.imprint","IMPRINT",EDGE,{"derivedFrom":subQ4}),-1.0]])]});}
            var Q17;
            {var subQ4=sQuery(id+"F32.wireOp",EDGE,"E468");Q17=makeQuery(id+"F32.imprint","IMPRINT",FACE,{"disambiguationData":[TD([[makeQuery(id+"F32.imprint","IMPRINT",EDGE,{"derivedFrom":subQ4}),1.0]])]});}
            var Q18;
            {var subQ4=sQuery(id+"F32.wireOp",EDGE,"E473");Q18=makeQuery(id+"F32.imprint","IMPRINT",FACE,{"disambiguationData":[TD([[makeQuery(id+"F32.imprint","IMPRINT",EDGE,{"derivedFrom":subQ4}),-1.0]])]});}
            extrude(context, id + "F33", {"entities" : qUnion([Q0, Q1, Q2, Q3, Q4, Q5, Q6, Q7, Q8, Q9, Q10, Q11, Q12, Q13, Q14, Q15, Q16, Q17, Q18]), "operationType" : NewBodyOperationType.REMOVE, "oppositeDirection" : true, "depth" : 4.22 * mm});
        }
        {
            var Q0;
            Q0 = qSketchRegion(id + "F32", true);
            var Q1;
            {var subQ7=sQuery(id+"F32.wireOp",EDGE,"E437");Q1=makeQuery(id+"F32.imprint","IMPRINT",FACE,{"disambiguationData":[TD([[makeQuery(id+"F32.imprint","IMPRINT",EDGE,{"derivedFrom":subQ7}),1.0]])]});}
            var Q2;
            {var subQ12=sQuery(id+"F32.wireOp",EDGE,"E447");Q2=makeQuery(id+"F32.imprint","IMPRINT",FACE,{"disambiguationData":[TD([[makeQuery(id+"F32.imprint","IMPRINT",EDGE,{"derivedFrom":subQ12}),1.0]])]});}
            extrude(context, id + "F34", {"entities" : qUnion([Q0, Q1, Q2]), "operationType" : NewBodyOperationType.ADD, "oppositeDirection" : true, "depth" : 2.54 * mm, "hasSecondDirection" : true, "secondDirectionOppositeDirection" : true, "secondDirectionDepth" : 1.27 * mm});
        }
        {
            var Q0;
            Q0=makeQuery(id+"F1.opExtrude","SWEPT_FACE",FACE,{"disambiguationData":[OSD([sQuery(id+"F0.wireOp",EDGE,"E5")])]});
            var sketch = newSketch(context, id + "F35", { "sketchPlane" : qUnion([Q0])});
            skLineSegment(sketch, "E477.bottom", {"start": v(-46.49, 0) * mm, "end": v(-1.78, 0) * mm});
            skLineSegment(sketch, "E477.top", {"start": v(-46.49, 57.15) * mm, "end": v(-1.78, 57.15) * mm});
            skLineSegment(sketch, "E477.left", {"start": v(-46.49, 0) * mm, "end": v(-46.49, 57.15) * mm});
            skLineSegment(sketch, "E477.right", {"start": v(-1.78, 0) * mm, "end": v(-1.78, 57.15) * mm});
            skLineSegment(sketch, "E478", {"start": v(-45.72, 0) * mm, "end": v(-45.72, 56.39) * mm});
            skLineSegment(sketch, "E479", {"start": v(-45.72, 56.39) * mm, "end": v(-2.54, 56.39) * mm});
            skLineSegment(sketch, "E480", {"start": v(-2.54, 56.39) * mm, "end": v(-2.54, 0) * mm});
            skLineSegment(sketch, "E481.bottom", {"start": v(-43.7, 54.36) * mm, "end": v(-26.3, 54.36) * mm});
            skLineSegment(sketch, "E481.top", {"start": v(-43.7, 2.03) * mm, "end": v(-26.3, 2.03) * mm});
            skLineSegment(sketch, "E481.left", {"start": v(-43.7, 54.36) * mm, "end": v(-43.7, 2.03) * mm});
            skLineSegment(sketch, "E481.right", {"start": v(-26.3, 54.36) * mm, "end": v(-26.3, 2.03) * mm});
            skLineSegment(sketch, "E482.bottom", {"start": v(-21.98, 2.03) * mm, "end": v(-4.58, 2.03) * mm});
            skLineSegment(sketch, "E482.top", {"start": v(-21.98, 54.36) * mm, "end": v(-4.58, 54.36) * mm});
            skLineSegment(sketch, "E482.left", {"start": v(-21.98, 2.03) * mm, "end": v(-21.98, 54.36) * mm});
            skLineSegment(sketch, "E482.right", {"start": v(-4.58, 2.03) * mm, "end": v(-4.58, 54.36) * mm});
            skLineSegment(sketch, "E483", {"start": v(-24.26, 0) * mm, "end": v(-24.26, 56.39) * mm});
            skLineSegment(sketch, "E484", {"start": v(-24, 56.39) * mm, "end": v(-24, 0) * mm});
            skLineSegment(sketch, "E485", {"start": v(-34.84, 54.36) * mm, "end": v(-34.84, 41.75) * mm});
            skLineSegment(sketch, "E486", {"start": v(-34.84, 41.75) * mm, "end": v(-43.7, 41.75) * mm});
            skLineSegment(sketch, "E487", {"start": v(-34.2, 54.36) * mm, "end": v(-34.2, 41.75) * mm});
            skLineSegment(sketch, "E488", {"start": v(-34.2, 41.75) * mm, "end": v(-26.3, 41.75) * mm});
            skLineSegment(sketch, "E489", {"start": v(-26.3, 41.12) * mm, "end": v(-34.2, 41.12) * mm});
            skLineSegment(sketch, "E490", {"start": v(-34.2, 41.12) * mm, "end": v(-34.2, 28.51) * mm});
            skLineSegment(sketch, "E491", {"start": v(-34.2, 28.51) * mm, "end": v(-26.3, 28.51) * mm});
            skLineSegment(sketch, "E492", {"start": v(-43.7, 41.12) * mm, "end": v(-34.84, 41.12) * mm});
            skLineSegment(sketch, "E493", {"start": v(-34.84, 41.12) * mm, "end": v(-34.84, 28.51) * mm});
            skLineSegment(sketch, "E494", {"start": v(-34.84, 28.51) * mm, "end": v(-43.7, 28.51) * mm});
            skLineSegment(sketch, "E495", {"start": v(-13.6, 54.36) * mm, "end": v(-13.6, 41.75) * mm});
            skLineSegment(sketch, "E496", {"start": v(-13.6, 41.75) * mm, "end": v(-21.98, 41.75) * mm});
            skLineSegment(sketch, "E497", {"start": v(-12.96, 54.36) * mm, "end": v(-12.96, 41.75) * mm});
            skLineSegment(sketch, "E498", {"start": v(-12.96, 41.75) * mm, "end": v(-4.58, 41.75) * mm});
            skLineSegment(sketch, "E499", {"start": v(-4.58, 41.12) * mm, "end": v(-12.96, 41.12) * mm});
            skLineSegment(sketch, "E500", {"start": v(-12.96, 41.12) * mm, "end": v(-12.96, 28.51) * mm});
            skLineSegment(sketch, "E501", {"start": v(-12.96, 28.51) * mm, "end": v(-4.58, 28.51) * mm});
            skLineSegment(sketch, "E502", {"start": v(-21.98, 41.12) * mm, "end": v(-13.6, 41.12) * mm});
            skLineSegment(sketch, "E503", {"start": v(-13.6, 41.12) * mm, "end": v(-13.6, 28.51) * mm});
            skLineSegment(sketch, "E504", {"start": v(-13.6, 28.51) * mm, "end": v(-21.98, 28.51) * mm});
            skLineSegment(sketch, "E505", {"start": v(-13.6, 27.88) * mm, "end": v(-13.6, 15.27) * mm});
            skLineSegment(sketch, "E506", {"start": v(-13.6, 15.27) * mm, "end": v(-21.98, 15.27) * mm});
            skLineSegment(sketch, "E507", {"start": v(-21.98, 14.64) * mm, "end": v(-13.6, 14.64) * mm});
            skLineSegment(sketch, "E508", {"start": v(-13.6, 14.64) * mm, "end": v(-13.6, 2.03) * mm});
            skLineSegment(sketch, "E509", {"start": v(-12.96, 27.88) * mm, "end": v(-12.96, 15.27) * mm});
            skLineSegment(sketch, "E510", {"start": v(-12.96, 15.27) * mm, "end": v(-4.58, 15.27) * mm});
            skLineSegment(sketch, "E511", {"start": v(-4.58, 14.64) * mm, "end": v(-12.96, 14.64) * mm});
            skLineSegment(sketch, "E512", {"start": v(-12.96, 14.64) * mm, "end": v(-12.96, 2.03) * mm});
            skLineSegment(sketch, "E513", {"start": v(-26.3, 27.88) * mm, "end": v(-34.2, 27.88) * mm});
            skLineSegment(sketch, "E514", {"start": v(-34.2, 27.88) * mm, "end": v(-34.2, 15.27) * mm});
            skLineSegment(sketch, "E515", {"start": v(-34.2, 15.27) * mm, "end": v(-26.3, 15.27) * mm});
            skLineSegment(sketch, "E516", {"start": v(-26.3, 14.64) * mm, "end": v(-34.2, 14.64) * mm});
            skLineSegment(sketch, "E517", {"start": v(-34.2, 14.64) * mm, "end": v(-34.2, 2.03) * mm});
            skLineSegment(sketch, "E518", {"start": v(-43.7, 27.88) * mm, "end": v(-34.84, 27.88) * mm});
            skLineSegment(sketch, "E519", {"start": v(-34.84, 27.88) * mm, "end": v(-34.84, 15.27) * mm});
            skLineSegment(sketch, "E520", {"start": v(-34.84, 15.27) * mm, "end": v(-43.7, 15.27) * mm});
            skLineSegment(sketch, "E521", {"start": v(-43.7, 14.64) * mm, "end": v(-34.84, 14.64) * mm});
            skLineSegment(sketch, "E522", {"start": v(-34.84, 14.64) * mm, "end": v(-34.84, 2.03) * mm});
            skLineSegment(sketch, "E523", {"start": v(-21.98, 27.88) * mm, "end": v(-13.6, 27.88) * mm});
            skLineSegment(sketch, "E524", {"start": v(-12.96, 27.88) * mm, "end": v(-4.58, 27.88) * mm});
            skSolve(sketch);
        }
        {
            var Q0;
            Q0 = qSketchRegion(id + "F35", true);
            var Q1;
            {var subQ3=sQuery(id+"F35.wireOp",EDGE,"E485");Q1=makeQuery(id+"F35.imprint","IMPRINT",FACE,{"disambiguationData":[TD([[makeQuery(id+"F35.imprint","IMPRINT",EDGE,{"derivedFrom":subQ3}),-1.0]])]});}
            var Q2;
            {var subQ0=sQuery(id+"F35.wireOp",EDGE,"E489");Q2=makeQuery(id+"F35.imprint","IMPRINT",FACE,{"disambiguationData":[TD([[makeQuery(id+"F35.imprint","IMPRINT",EDGE,{"derivedFrom":subQ0}),1.0]])]});}
            var Q3;
            {var subQ0=sQuery(id+"F35.wireOp",EDGE,"E492");Q3=makeQuery(id+"F35.imprint","IMPRINT",FACE,{"disambiguationData":[TD([[makeQuery(id+"F35.imprint","IMPRINT",EDGE,{"derivedFrom":subQ0}),-1.0]])]});}
            var Q4;
            {var subQ3=sQuery(id+"F35.wireOp",EDGE,"E487");Q4=makeQuery(id+"F35.imprint","IMPRINT",FACE,{"disambiguationData":[TD([[makeQuery(id+"F35.imprint","IMPRINT",EDGE,{"derivedFrom":subQ3}),1.0]])]});}
            var Q5;
            {var subQ0=sQuery(id+"F35.wireOp",EDGE,"E518");Q5=makeQuery(id+"F35.imprint","IMPRINT",FACE,{"disambiguationData":[TD([[makeQuery(id+"F35.imprint","IMPRINT",EDGE,{"derivedFrom":subQ0}),-1.0]])]});}
            var Q6;
            {var subQ0=sQuery(id+"F35.wireOp",EDGE,"E513");Q6=makeQuery(id+"F35.imprint","IMPRINT",FACE,{"disambiguationData":[TD([[makeQuery(id+"F35.imprint","IMPRINT",EDGE,{"derivedFrom":subQ0}),1.0]])]});}
            var Q7;
            {var subQ5=sQuery(id+"F35.wireOp",EDGE,"E485");Q7=makeQuery(id+"F35.imprint","IMPRINT",FACE,{"disambiguationData":[TD([[makeQuery(id+"F35.imprint","IMPRINT",EDGE,{"derivedFrom":subQ5}),1.0]])]});}
            var Q8;
            {var subQ4=sQuery(id+"F35.wireOp",EDGE,"E516");Q8=makeQuery(id+"F35.imprint","IMPRINT",FACE,{"disambiguationData":[TD([[makeQuery(id+"F35.imprint","IMPRINT",EDGE,{"derivedFrom":subQ4}),1.0]])]});}
            var Q9;
            {var subQ4=sQuery(id+"F35.wireOp",EDGE,"E521");Q9=makeQuery(id+"F35.imprint","IMPRINT",FACE,{"disambiguationData":[TD([[makeQuery(id+"F35.imprint","IMPRINT",EDGE,{"derivedFrom":subQ4}),-1.0]])]});}
            var Q10;
            {var subQ3=sQuery(id+"F35.wireOp",EDGE,"E495");Q10=makeQuery(id+"F35.imprint","IMPRINT",FACE,{"disambiguationData":[TD([[makeQuery(id+"F35.imprint","IMPRINT",EDGE,{"derivedFrom":subQ3}),-1.0]])]});}
            var Q11;
            {var subQ0=sQuery(id+"F35.wireOp",EDGE,"E499");Q11=makeQuery(id+"F35.imprint","IMPRINT",FACE,{"disambiguationData":[TD([[makeQuery(id+"F35.imprint","IMPRINT",EDGE,{"derivedFrom":subQ0}),1.0]])]});}
            var Q12;
            {var subQ0=sQuery(id+"F35.wireOp",EDGE,"E502");Q12=makeQuery(id+"F35.imprint","IMPRINT",FACE,{"disambiguationData":[TD([[makeQuery(id+"F35.imprint","IMPRINT",EDGE,{"derivedFrom":subQ0}),-1.0]])]});}
            var Q13;
            Q13=makeQuery(id+"F35.imprint","IMPRINT",FACE,{"disambiguationData":[TD([[makeQuery(id+"F35.imprint","IMPRINT",EDGE,{"derivedFrom":sQuery(id+"F35.wireOp",EDGE,"E505")}),-1.0]])]});
            var Q14;
            Q14=makeQuery(id+"F35.imprint","IMPRINT",FACE,{"disambiguationData":[TD([[makeQuery(id+"F35.imprint","IMPRINT",EDGE,{"derivedFrom":sQuery(id+"F35.wireOp",EDGE,"E509")}),1.0]])]});
            var Q15;
            {var subQ3=sQuery(id+"F35.wireOp",EDGE,"E497");Q15=makeQuery(id+"F35.imprint","IMPRINT",FACE,{"disambiguationData":[TD([[makeQuery(id+"F35.imprint","IMPRINT",EDGE,{"derivedFrom":subQ3}),1.0]])]});}
            var Q16;
            {var subQ16=sQuery(id+"F35.wireOp",EDGE,"E495");Q16=makeQuery(id+"F35.imprint","IMPRINT",FACE,{"disambiguationData":[TD([[makeQuery(id+"F35.imprint","IMPRINT",EDGE,{"derivedFrom":subQ16}),1.0]])]});}
            var Q17;
            {var subQ4=sQuery(id+"F35.wireOp",EDGE,"E511");Q17=makeQuery(id+"F35.imprint","IMPRINT",FACE,{"disambiguationData":[TD([[makeQuery(id+"F35.imprint","IMPRINT",EDGE,{"derivedFrom":subQ4}),1.0]])]});}
            var Q18;
            {var subQ4=sQuery(id+"F35.wireOp",EDGE,"E507");Q18=makeQuery(id+"F35.imprint","IMPRINT",FACE,{"disambiguationData":[TD([[makeQuery(id+"F35.imprint","IMPRINT",EDGE,{"derivedFrom":subQ4}),-1.0]])]});}
            extrude(context, id + "F36", {"entities" : qUnion([Q0, Q1, Q2, Q3, Q4, Q5, Q6, Q7, Q8, Q9, Q10, Q11, Q12, Q13, Q14, Q15, Q16, Q17, Q18]), "operationType" : NewBodyOperationType.REMOVE, "oppositeDirection" : true, "depth" : 4.22 * mm});
        }
        {
            var Q0;
            Q0 = qSketchRegion(id + "F35", true);
            var Q1;
            {var subQ5=sQuery(id+"F35.wireOp",EDGE,"E485");Q1=makeQuery(id+"F35.imprint","IMPRINT",FACE,{"disambiguationData":[TD([[makeQuery(id+"F35.imprint","IMPRINT",EDGE,{"derivedFrom":subQ5}),1.0]])]});}
            var Q2;
            {var subQ16=sQuery(id+"F35.wireOp",EDGE,"E495");Q2=makeQuery(id+"F35.imprint","IMPRINT",FACE,{"disambiguationData":[TD([[makeQuery(id+"F35.imprint","IMPRINT",EDGE,{"derivedFrom":subQ16}),1.0]])]});}
            extrude(context, id + "F37", {"entities" : qUnion([Q0, Q1, Q2]), "operationType" : NewBodyOperationType.ADD, "oppositeDirection" : true, "depth" : 2.54 * mm, "hasSecondDirection" : true, "secondDirectionOppositeDirection" : true, "secondDirectionDepth" : 1.27 * mm});
        }
        {
            var Q0;
            Q0=makeQuery(id+"F1.opExtrude","SWEPT_FACE",FACE,{"disambiguationData":[OSD([sQuery(id+"F0.wireOp",EDGE,"E9")])]});
            var sketch = newSketch(context, id + "F38", { "sketchPlane" : qUnion([Q0])});
            skLineSegment(sketch, "E525.bottom", {"start": v(-205.52, 57.15) * mm, "end": v(-116.62, 57.15) * mm});
            skLineSegment(sketch, "E525.top", {"start": v(-205.52, 41.9) * mm, "end": v(-116.62, 41.9) * mm});
            skLineSegment(sketch, "E525.left", {"start": v(-205.52, 57.15) * mm, "end": v(-205.52, 41.9) * mm});
            skLineSegment(sketch, "E525.right", {"start": v(-116.62, 57.15) * mm, "end": v(-116.62, 41.9) * mm});
            skLineSegment(sketch, "E526.bottom", {"start": v(-204.76, 42.67) * mm, "end": v(-117.38, 42.67) * mm});
            skLineSegment(sketch, "E526.top", {"start": v(-204.76, 56.39) * mm, "end": v(-117.38, 56.39) * mm});
            skLineSegment(sketch, "E526.left", {"start": v(-204.76, 42.67) * mm, "end": v(-204.76, 56.39) * mm});
            skLineSegment(sketch, "E526.right", {"start": v(-117.38, 42.67) * mm, "end": v(-117.38, 56.39) * mm});
            skLineSegment(sketch, "E527.bottom", {"start": v(-256.7, 57.15) * mm, "end": v(-226.72, 57.15) * mm});
            skLineSegment(sketch, "E527.top", {"start": v(-256.7, 23.62) * mm, "end": v(-226.72, 23.62) * mm});
            skLineSegment(sketch, "E527.left", {"start": v(-256.7, 57.15) * mm, "end": v(-256.7, 23.62) * mm});
            skLineSegment(sketch, "E527.right", {"start": v(-226.72, 57.15) * mm, "end": v(-226.72, 23.62) * mm});
            skLineSegment(sketch, "E528.bottom", {"start": v(-239.51, 55.12) * mm, "end": v(-228.75, 55.12) * mm});
            skLineSegment(sketch, "E528.top", {"start": v(-239.51, 25.65) * mm, "end": v(-228.75, 25.65) * mm});
            skLineSegment(sketch, "E528.left", {"start": v(-239.51, 55.12) * mm, "end": v(-239.51, 25.65) * mm});
            skLineSegment(sketch, "E528.right", {"start": v(-228.75, 55.12) * mm, "end": v(-228.75, 25.65) * mm});
            skLineSegment(sketch, "E529", {"start": v(-233.8, 55.12) * mm, "end": v(-233.8, 25.65) * mm});
            skLineSegment(sketch, "E530", {"start": v(-234.43, 55.12) * mm, "end": v(-234.43, 25.65) * mm});
            skLineSegment(sketch, "E531", {"start": v(-239.51, 45.72) * mm, "end": v(-228.75, 45.72) * mm});
            skLineSegment(sketch, "E532", {"start": v(-239.51, 45.09) * mm, "end": v(-228.75, 45.09) * mm});
            skLineSegment(sketch, "E533", {"start": v(-239.51, 35.69) * mm, "end": v(-228.75, 35.69) * mm});
            skLineSegment(sketch, "E534", {"start": v(-239.51, 35.05) * mm, "end": v(-228.75, 35.05) * mm});
            skLineSegment(sketch, "E535", {"start": v(-234.43, 55.12) * mm, "end": v(-234.43, 45.09) * mm});
            skLineSegment(sketch, "E536", {"start": v(-234.43, 55.12) * mm, "end": v(-234.43, 45.72) * mm});
            skLineSegment(sketch, "E537", {"start": v(-234.43, 45.72) * mm, "end": v(-234.43, 45.09) * mm});
            skLineSegment(sketch, "E538", {"start": v(-234.43, 45.09) * mm, "end": v(-234.43, 35.69) * mm});
            skLineSegment(sketch, "E539", {"start": v(-234.43, 35.69) * mm, "end": v(-234.43, 35.05) * mm});
            skLineSegment(sketch, "E540", {"start": v(-234.43, 35.05) * mm, "end": v(-234.43, 25.65) * mm});
            skLineSegment(sketch, "E541.bottom", {"start": v(-254.66, 55.12) * mm, "end": v(-243.9, 55.12) * mm});
            skLineSegment(sketch, "E541.top", {"start": v(-254.66, 25.65) * mm, "end": v(-243.9, 25.65) * mm});
            skLineSegment(sketch, "E541.left", {"start": v(-254.66, 55.12) * mm, "end": v(-254.66, 25.65) * mm});
            skLineSegment(sketch, "E541.right", {"start": v(-243.9, 55.12) * mm, "end": v(-243.9, 25.65) * mm});
            skLineSegment(sketch, "E542", {"start": v(-248.97, 55.12) * mm, "end": v(-248.97, 25.65) * mm});
            skLineSegment(sketch, "E543", {"start": v(-249.6, 55.12) * mm, "end": v(-249.6, 25.65) * mm});
            skLineSegment(sketch, "E544", {"start": v(-254.66, 45.72) * mm, "end": v(-243.9, 45.72) * mm});
            skLineSegment(sketch, "E545", {"start": v(-254.66, 45.09) * mm, "end": v(-243.9, 45.09) * mm});
            skLineSegment(sketch, "E546", {"start": v(-254.66, 35.69) * mm, "end": v(-243.9, 35.69) * mm});
            skLineSegment(sketch, "E547", {"start": v(-254.66, 35.05) * mm, "end": v(-243.9, 35.05) * mm});
            skLineSegment(sketch, "E548", {"start": v(-249.6, 55.12) * mm, "end": v(-249.6, 45.09) * mm});
            skLineSegment(sketch, "E549", {"start": v(-249.6, 55.12) * mm, "end": v(-249.6, 45.72) * mm});
            skLineSegment(sketch, "E550", {"start": v(-249.6, 45.72) * mm, "end": v(-249.6, 45.09) * mm});
            skLineSegment(sketch, "E551", {"start": v(-249.6, 45.09) * mm, "end": v(-249.6, 35.69) * mm});
            skLineSegment(sketch, "E552", {"start": v(-249.6, 35.69) * mm, "end": v(-249.6, 35.05) * mm});
            skLineSegment(sketch, "E553", {"start": v(-249.6, 35.05) * mm, "end": v(-249.6, 25.65) * mm});
            skLineSegment(sketch, "E554.bottom", {"start": v(-255.93, 56.39) * mm, "end": v(-227.48, 56.39) * mm});
            skLineSegment(sketch, "E554.top", {"start": v(-255.93, 24.38) * mm, "end": v(-227.48, 24.38) * mm});
            skLineSegment(sketch, "E554.left", {"start": v(-255.93, 56.39) * mm, "end": v(-255.93, 24.38) * mm});
            skLineSegment(sketch, "E554.right", {"start": v(-227.48, 56.39) * mm, "end": v(-227.48, 24.38) * mm});
            skLineSegment(sketch, "E555", {"start": v(-242.09, 24.38) * mm, "end": v(-242.09, 56.39) * mm});
            skLineSegment(sketch, "E556", {"start": v(-241.32, 56.39) * mm, "end": v(-241.32, 24.38) * mm});
            skLineSegment(sketch, "E557.bottom", {"start": v(-395.22, 57.15) * mm, "end": v(-306.32, 57.15) * mm});
            skLineSegment(sketch, "E557.top", {"start": v(-395.22, 41.9) * mm, "end": v(-306.32, 41.9) * mm});
            skLineSegment(sketch, "E557.left", {"start": v(-395.22, 57.15) * mm, "end": v(-395.22, 41.9) * mm});
            skLineSegment(sketch, "E557.right", {"start": v(-306.32, 57.15) * mm, "end": v(-306.32, 41.9) * mm});
            skLineSegment(sketch, "E558.bottom", {"start": v(-394.46, 42.67) * mm, "end": v(-307.09, 42.67) * mm});
            skLineSegment(sketch, "E558.top", {"start": v(-394.46, 56.39) * mm, "end": v(-307.09, 56.39) * mm});
            skLineSegment(sketch, "E558.left", {"start": v(-394.46, 42.67) * mm, "end": v(-394.46, 56.39) * mm});
            skLineSegment(sketch, "E558.right", {"start": v(-307.09, 42.67) * mm, "end": v(-307.09, 56.39) * mm});
            skLineSegment(sketch, "E559.bottom", {"start": v(-506.73, 57.15) * mm, "end": v(-417.83, 57.15) * mm});
            skLineSegment(sketch, "E559.top", {"start": v(-506.73, 41.9) * mm, "end": v(-417.83, 41.9) * mm});
            skLineSegment(sketch, "E559.left", {"start": v(-506.73, 57.15) * mm, "end": v(-506.73, 41.91) * mm});
            skLineSegment(sketch, "E559.right", {"start": v(-417.83, 57.15) * mm, "end": v(-417.83, 41.9) * mm});
            skLineSegment(sketch, "E560.bottom", {"start": v(-505.97, 42.67) * mm, "end": v(-418.6, 42.67) * mm});
            skLineSegment(sketch, "E560.top", {"start": v(-505.97, 56.39) * mm, "end": v(-418.6, 56.39) * mm});
            skLineSegment(sketch, "E560.left", {"start": v(-505.97, 42.67) * mm, "end": v(-505.97, 56.39) * mm});
            skLineSegment(sketch, "E560.right", {"start": v(-418.6, 42.67) * mm, "end": v(-418.6, 56.39) * mm});
            skSolve(sketch);
        }
        {
            var Q0;
            {Q0=qUnion([makeQuery(id+"F38.imprint","IMPRINT",FACE,{"disambiguationData":[TD([[makeQuery(id+"F38.imprint","IMPRINT",EDGE,{"derivedFrom":sQuery(id+"F38.wireOp",EDGE,"E525.bottom")}),-1.0]])]}),makeQuery(id+"F38.imprint","IMPRINT",FACE,{"disambiguationData":[TD([[makeQuery(id+"F38.imprint","IMPRINT",EDGE,{"derivedFrom":sQuery(id+"F38.wireOp",EDGE,"E557.bottom")}),-1.0]])]}),makeQuery(id+"F38.imprint","IMPRINT",FACE,{"disambiguationData":[TD([[makeQuery(id+"F38.imprint","IMPRINT",EDGE,{"derivedFrom":sQuery(id+"F38.wireOp",EDGE,"E559.bottom")}),-1.0]])]}),makeQuery(id+"F38.imprint","IMPRINT",FACE,{"disambiguationData":[TD([[makeQuery(id+"F38.imprint","IMPRINT",EDGE,{"derivedFrom":sQuery(id+"F38.wireOp",EDGE,"E527.bottom")}),-1.0]])]})]);}
            var Q1;
            Q1=makeQuery(id+"F38.imprint","IMPRINT",FACE,{"disambiguationData":[TD([[makeQuery(id+"F38.imprint","IMPRINT",EDGE,{"derivedFrom":sQuery(id+"F38.wireOp",EDGE,"E526.bottom")}),1.0]])]});
            var Q2;
            {var subQ27=sQuery(id+"F38.wireOp",EDGE,"E554.left");Q2=makeQuery(id+"F38.imprint","IMPRINT",FACE,{"disambiguationData":[TD([[makeQuery(id+"F38.imprint","IMPRINT",EDGE,{"derivedFrom":subQ27}),1.0]])]});}
            var Q3;
            {var subQ2=sQuery(id+"F38.wireOp",EDGE,"E555");Q3=makeQuery(id+"F38.imprint","IMPRINT",FACE,{"disambiguationData":[TD([[makeQuery(id+"F38.imprint","IMPRINT",EDGE,{"derivedFrom":subQ2}),-1.0]])]});}
            var Q4;
            {var subQ9=sQuery(id+"F38.wireOp",EDGE,"E554.right");Q4=makeQuery(id+"F38.imprint","IMPRINT",FACE,{"disambiguationData":[TD([[makeQuery(id+"F38.imprint","IMPRINT",EDGE,{"derivedFrom":subQ9}),-1.0]])]});}
            var Q5;
            {var subQ0=sQuery(id+"F38.wireOp",EDGE,"E541.left");var subQ1=sQuery(id+"F38.wireOp",EDGE,"E541.bottom");var subQ2=makeQuery(id+"F38.imprint","INTERSECT",VERTEX,{"derivedFrom":[subQ1,subQ0]});Q5=makeQuery(id+"F38.imprint","IMPRINT",FACE,{"disambiguationData":[TD([[makeQuery(id+"F38.imprint","IMPRINT",EDGE,{"disambiguationData":[TD([[subQ2,-1.0]])],"derivedFrom":subQ1}),-1.0]])]});}
            var Q6;
            {var subQ0=sQuery(id+"F38.wireOp",EDGE,"E542");var subQ1=sQuery(id+"F38.wireOp",EDGE,"E541.bottom");var subQ2=makeQuery(id+"F38.imprint","INTERSECT",VERTEX,{"derivedFrom":[subQ1,subQ0]});Q6=makeQuery(id+"F38.imprint","IMPRINT",FACE,{"disambiguationData":[TD([[makeQuery(id+"F38.imprint","IMPRINT",EDGE,{"disambiguationData":[TD([[subQ2,1.0]])],"derivedFrom":subQ1}),-1.0]])]});}
            var Q7;
            {var subQ0=sQuery(id+"F38.wireOp",EDGE,"E542");var subQ1=sQuery(id+"F38.wireOp",EDGE,"E541.bottom");var subQ2=makeQuery(id+"F38.imprint","INTERSECT",VERTEX,{"derivedFrom":[subQ1,subQ0]});Q7=makeQuery(id+"F38.imprint","IMPRINT",FACE,{"disambiguationData":[TD([[makeQuery(id+"F38.imprint","IMPRINT",EDGE,{"disambiguationData":[TD([[subQ2,-1.0]])],"derivedFrom":subQ1}),-1.0]])]});}
            var Q8;
            {var subQ0=sQuery(id+"F38.wireOp",EDGE,"E544");var subQ1=sQuery(id+"F38.wireOp",EDGE,"E541.right");var subQ2=makeQuery(id+"F38.imprint","INTERSECT",VERTEX,{"derivedFrom":[subQ1,subQ0]});Q8=makeQuery(id+"F38.imprint","IMPRINT",FACE,{"disambiguationData":[TD([[makeQuery(id+"F38.imprint","IMPRINT",EDGE,{"disambiguationData":[TD([[subQ2,-1.0]])],"derivedFrom":subQ1}),-1.0]])]});}
            var Q9;
            {var subQ0=sQuery(id+"F38.wireOp",EDGE,"E545");var subQ1=sQuery(id+"F38.wireOp",EDGE,"E541.right");var subQ2=makeQuery(id+"F38.imprint","INTERSECT",VERTEX,{"derivedFrom":[subQ1,subQ0]});Q9=makeQuery(id+"F38.imprint","IMPRINT",FACE,{"disambiguationData":[TD([[makeQuery(id+"F38.imprint","IMPRINT",EDGE,{"disambiguationData":[TD([[subQ2,-1.0]])],"derivedFrom":subQ1}),-1.0]])]});}
            var Q10;
            {var subQ0=sQuery(id+"F38.wireOp",EDGE,"E545");var subQ1=sQuery(id+"F38.wireOp",EDGE,"E542");var subQ2=makeQuery(id+"F38.imprint","INTERSECT",VERTEX,{"derivedFrom":[subQ1,subQ0]});Q10=makeQuery(id+"F38.imprint","IMPRINT",FACE,{"disambiguationData":[TD([[makeQuery(id+"F38.imprint","IMPRINT",EDGE,{"disambiguationData":[TD([[subQ2,-1.0]])],"derivedFrom":subQ1}),-1.0]])]});}
            var Q11;
            {var subQ0=sQuery(id+"F38.wireOp",EDGE,"E545");var subQ1=sQuery(id+"F38.wireOp",EDGE,"E541.left");var subQ2=makeQuery(id+"F38.imprint","INTERSECT",VERTEX,{"derivedFrom":[subQ1,subQ0]});Q11=makeQuery(id+"F38.imprint","IMPRINT",FACE,{"disambiguationData":[TD([[makeQuery(id+"F38.imprint","IMPRINT",EDGE,{"disambiguationData":[TD([[subQ2,-1.0]])],"derivedFrom":subQ1}),1.0]])]});}
            var Q12;
            {var subQ0=sQuery(id+"F38.wireOp",EDGE,"E542");var subQ1=sQuery(id+"F38.wireOp",EDGE,"E541.top");var subQ2=makeQuery(id+"F38.imprint","INTERSECT",VERTEX,{"derivedFrom":[subQ1,subQ0]});Q12=makeQuery(id+"F38.imprint","IMPRINT",FACE,{"disambiguationData":[TD([[makeQuery(id+"F38.imprint","IMPRINT",EDGE,{"disambiguationData":[TD([[subQ2,-1.0]])],"derivedFrom":subQ1}),1.0]])]});}
            var Q13;
            {var subQ0=sQuery(id+"F38.wireOp",EDGE,"E541.left");var subQ1=sQuery(id+"F38.wireOp",EDGE,"E541.top");var subQ2=makeQuery(id+"F38.imprint","INTERSECT",VERTEX,{"derivedFrom":[subQ1,subQ0]});Q13=makeQuery(id+"F38.imprint","IMPRINT",FACE,{"disambiguationData":[TD([[makeQuery(id+"F38.imprint","IMPRINT",EDGE,{"disambiguationData":[TD([[subQ2,-1.0]])],"derivedFrom":subQ1}),1.0]])]});}
            var Q14;
            {var subQ0=sQuery(id+"F38.wireOp",EDGE,"E542");var subQ1=sQuery(id+"F38.wireOp",EDGE,"E541.top");var subQ2=makeQuery(id+"F38.imprint","INTERSECT",VERTEX,{"derivedFrom":[subQ1,subQ0]});Q14=makeQuery(id+"F38.imprint","IMPRINT",FACE,{"disambiguationData":[TD([[makeQuery(id+"F38.imprint","IMPRINT",EDGE,{"disambiguationData":[TD([[subQ2,1.0]])],"derivedFrom":subQ1}),1.0]])]});}
            var Q15;
            {var subQ0=sQuery(id+"F38.wireOp",EDGE,"E528.left");var subQ1=sQuery(id+"F38.wireOp",EDGE,"E528.top");var subQ2=makeQuery(id+"F38.imprint","INTERSECT",VERTEX,{"derivedFrom":[subQ1,subQ0]});Q15=makeQuery(id+"F38.imprint","IMPRINT",FACE,{"disambiguationData":[TD([[makeQuery(id+"F38.imprint","IMPRINT",EDGE,{"disambiguationData":[TD([[subQ2,-1.0]])],"derivedFrom":subQ1}),1.0]])]});}
            var Q16;
            {var subQ0=sQuery(id+"F38.wireOp",EDGE,"E529");var subQ1=sQuery(id+"F38.wireOp",EDGE,"E528.top");var subQ2=makeQuery(id+"F38.imprint","INTERSECT",VERTEX,{"derivedFrom":[subQ1,subQ0]});Q16=makeQuery(id+"F38.imprint","IMPRINT",FACE,{"disambiguationData":[TD([[makeQuery(id+"F38.imprint","IMPRINT",EDGE,{"disambiguationData":[TD([[subQ2,-1.0]])],"derivedFrom":subQ1}),1.0]])]});}
            var Q17;
            {var subQ0=sQuery(id+"F38.wireOp",EDGE,"E532");var subQ1=sQuery(id+"F38.wireOp",EDGE,"E528.right");var subQ2=makeQuery(id+"F38.imprint","INTERSECT",VERTEX,{"derivedFrom":[subQ1,subQ0]});Q17=makeQuery(id+"F38.imprint","IMPRINT",FACE,{"disambiguationData":[TD([[makeQuery(id+"F38.imprint","IMPRINT",EDGE,{"disambiguationData":[TD([[subQ2,-1.0]])],"derivedFrom":subQ1}),-1.0]])]});}
            var Q18;
            {var subQ0=sQuery(id+"F38.wireOp",EDGE,"E532");var subQ1=sQuery(id+"F38.wireOp",EDGE,"E529");var subQ2=makeQuery(id+"F38.imprint","INTERSECT",VERTEX,{"derivedFrom":[subQ1,subQ0]});Q18=makeQuery(id+"F38.imprint","IMPRINT",FACE,{"disambiguationData":[TD([[makeQuery(id+"F38.imprint","IMPRINT",EDGE,{"disambiguationData":[TD([[subQ2,-1.0]])],"derivedFrom":subQ1}),-1.0]])]});}
            var Q19;
            {var subQ0=sQuery(id+"F38.wireOp",EDGE,"E533");var subQ1=sQuery(id+"F38.wireOp",EDGE,"E528.left");var subQ2=makeQuery(id+"F38.imprint","INTERSECT",VERTEX,{"derivedFrom":[subQ1,subQ0]});Q19=makeQuery(id+"F38.imprint","IMPRINT",FACE,{"disambiguationData":[TD([[makeQuery(id+"F38.imprint","IMPRINT",EDGE,{"disambiguationData":[TD([[subQ2,-1.0]])],"derivedFrom":subQ1}),1.0]])]});}
            var Q20;
            {var subQ0=sQuery(id+"F38.wireOp",EDGE,"E533");var subQ1=sQuery(id+"F38.wireOp",EDGE,"E528.right");var subQ2=makeQuery(id+"F38.imprint","INTERSECT",VERTEX,{"derivedFrom":[subQ1,subQ0]});Q20=makeQuery(id+"F38.imprint","IMPRINT",FACE,{"disambiguationData":[TD([[makeQuery(id+"F38.imprint","IMPRINT",EDGE,{"disambiguationData":[TD([[subQ2,-1.0]])],"derivedFrom":subQ1}),-1.0]])]});}
            var Q21;
            {var subQ0=sQuery(id+"F38.wireOp",EDGE,"E528.left");var subQ1=sQuery(id+"F38.wireOp",EDGE,"E528.bottom");var subQ2=makeQuery(id+"F38.imprint","INTERSECT",VERTEX,{"derivedFrom":[subQ1,subQ0]});Q21=makeQuery(id+"F38.imprint","IMPRINT",FACE,{"disambiguationData":[TD([[makeQuery(id+"F38.imprint","IMPRINT",EDGE,{"disambiguationData":[TD([[subQ2,-1.0]])],"derivedFrom":subQ1}),-1.0]])]});}
            var Q22;
            {var subQ0=sQuery(id+"F38.wireOp",EDGE,"E529");var subQ1=sQuery(id+"F38.wireOp",EDGE,"E528.bottom");var subQ2=makeQuery(id+"F38.imprint","INTERSECT",VERTEX,{"derivedFrom":[subQ1,subQ0]});Q22=makeQuery(id+"F38.imprint","IMPRINT",FACE,{"disambiguationData":[TD([[makeQuery(id+"F38.imprint","IMPRINT",EDGE,{"disambiguationData":[TD([[subQ2,-1.0]])],"derivedFrom":subQ1}),-1.0]])]});}
            var Q23;
            {var subQ0=sQuery(id+"F38.wireOp",EDGE,"E532");var subQ1=sQuery(id+"F38.wireOp",EDGE,"E528.left");var subQ2=makeQuery(id+"F38.imprint","INTERSECT",VERTEX,{"derivedFrom":[subQ1,subQ0]});Q23=makeQuery(id+"F38.imprint","IMPRINT",FACE,{"disambiguationData":[TD([[makeQuery(id+"F38.imprint","IMPRINT",EDGE,{"disambiguationData":[TD([[subQ2,1.0]])],"derivedFrom":subQ1}),1.0]])]});}
            var Q24;
            {var subQ0=sQuery(id+"F38.wireOp",EDGE,"E547");var subQ1=sQuery(id+"F38.wireOp",EDGE,"E541.left");var subQ2=makeQuery(id+"F38.imprint","INTERSECT",VERTEX,{"derivedFrom":[subQ1,subQ0]});Q24=makeQuery(id+"F38.imprint","IMPRINT",FACE,{"disambiguationData":[TD([[makeQuery(id+"F38.imprint","IMPRINT",EDGE,{"disambiguationData":[TD([[subQ2,1.0]])],"derivedFrom":subQ1}),1.0]])]});}
            var Q25;
            {var subQ0=sQuery(id+"F38.wireOp",EDGE,"E544");var subQ1=sQuery(id+"F38.wireOp",EDGE,"E541.left");var subQ2=makeQuery(id+"F38.imprint","INTERSECT",VERTEX,{"derivedFrom":[subQ1,subQ0]});Q25=makeQuery(id+"F38.imprint","IMPRINT",FACE,{"disambiguationData":[TD([[makeQuery(id+"F38.imprint","IMPRINT",EDGE,{"disambiguationData":[TD([[subQ2,-1.0]])],"derivedFrom":subQ1}),1.0]])]});}
            var Q26;
            {var subQ0=sQuery(id+"F38.wireOp",EDGE,"E544");var subQ1=sQuery(id+"F38.wireOp",EDGE,"E542");var subQ2=makeQuery(id+"F38.imprint","INTERSECT",VERTEX,{"derivedFrom":[subQ1,subQ0]});Q26=makeQuery(id+"F38.imprint","IMPRINT",FACE,{"disambiguationData":[TD([[makeQuery(id+"F38.imprint","IMPRINT",EDGE,{"disambiguationData":[TD([[subQ2,-1.0]])],"derivedFrom":subQ1}),-1.0]])]});}
            var Q27;
            {var subQ0=sQuery(id+"F38.wireOp",EDGE,"E547");var subQ1=sQuery(id+"F38.wireOp",EDGE,"E541.right");var subQ2=makeQuery(id+"F38.imprint","INTERSECT",VERTEX,{"derivedFrom":[subQ1,subQ0]});Q27=makeQuery(id+"F38.imprint","IMPRINT",FACE,{"disambiguationData":[TD([[makeQuery(id+"F38.imprint","IMPRINT",EDGE,{"disambiguationData":[TD([[subQ2,1.0]])],"derivedFrom":subQ1}),-1.0]])]});}
            var Q28;
            {var subQ0=sQuery(id+"F38.wireOp",EDGE,"E547");var subQ1=sQuery(id+"F38.wireOp",EDGE,"E542");var subQ2=makeQuery(id+"F38.imprint","INTERSECT",VERTEX,{"derivedFrom":[subQ1,subQ0]});Q28=makeQuery(id+"F38.imprint","IMPRINT",FACE,{"disambiguationData":[TD([[makeQuery(id+"F38.imprint","IMPRINT",EDGE,{"disambiguationData":[TD([[subQ2,1.0]])],"derivedFrom":subQ1}),-1.0]])]});}
            var Q29;
            {var subQ0=sQuery(id+"F38.wireOp",EDGE,"E532");var subQ1=sQuery(id+"F38.wireOp",EDGE,"E528.left");var subQ2=makeQuery(id+"F38.imprint","INTERSECT",VERTEX,{"derivedFrom":[subQ1,subQ0]});Q29=makeQuery(id+"F38.imprint","IMPRINT",FACE,{"disambiguationData":[TD([[makeQuery(id+"F38.imprint","IMPRINT",EDGE,{"disambiguationData":[TD([[subQ2,-1.0]])],"derivedFrom":subQ1}),1.0]])]});}
            var Q30;
            {var subQ0=sQuery(id+"F38.wireOp",EDGE,"E531");var subQ1=sQuery(id+"F38.wireOp",EDGE,"E529");var subQ2=makeQuery(id+"F38.imprint","INTERSECT",VERTEX,{"derivedFrom":[subQ1,subQ0]});Q30=makeQuery(id+"F38.imprint","IMPRINT",FACE,{"disambiguationData":[TD([[makeQuery(id+"F38.imprint","IMPRINT",EDGE,{"disambiguationData":[TD([[subQ2,-1.0]])],"derivedFrom":subQ1}),-1.0]])]});}
            var Q31;
            {var subQ0=sQuery(id+"F38.wireOp",EDGE,"E534");var subQ1=sQuery(id+"F38.wireOp",EDGE,"E529");var subQ2=makeQuery(id+"F38.imprint","INTERSECT",VERTEX,{"derivedFrom":[subQ1,subQ0]});Q31=makeQuery(id+"F38.imprint","IMPRINT",FACE,{"disambiguationData":[TD([[makeQuery(id+"F38.imprint","IMPRINT",EDGE,{"disambiguationData":[TD([[subQ2,1.0]])],"derivedFrom":subQ1}),-1.0]])]});}
            var Q32;
            {var subQ0=sQuery(id+"F38.wireOp",EDGE,"E529");var subQ1=sQuery(id+"F38.wireOp",EDGE,"E528.top");var subQ2=makeQuery(id+"F38.imprint","INTERSECT",VERTEX,{"derivedFrom":[subQ1,subQ0]});Q32=makeQuery(id+"F38.imprint","IMPRINT",FACE,{"disambiguationData":[TD([[makeQuery(id+"F38.imprint","IMPRINT",EDGE,{"disambiguationData":[TD([[subQ2,1.0]])],"derivedFrom":subQ1}),1.0]])]});}
            var Q33;
            {var subQ0=sQuery(id+"F38.wireOp",EDGE,"E532");var subQ1=sQuery(id+"F38.wireOp",EDGE,"E528.right");var subQ2=makeQuery(id+"F38.imprint","INTERSECT",VERTEX,{"derivedFrom":[subQ1,subQ0]});Q33=makeQuery(id+"F38.imprint","IMPRINT",FACE,{"disambiguationData":[TD([[makeQuery(id+"F38.imprint","IMPRINT",EDGE,{"disambiguationData":[TD([[subQ2,1.0]])],"derivedFrom":subQ1}),-1.0]])]});}
            var Q34;
            {var subQ0=sQuery(id+"F38.wireOp",EDGE,"E529");var subQ1=sQuery(id+"F38.wireOp",EDGE,"E528.bottom");var subQ2=makeQuery(id+"F38.imprint","INTERSECT",VERTEX,{"derivedFrom":[subQ1,subQ0]});Q34=makeQuery(id+"F38.imprint","IMPRINT",FACE,{"disambiguationData":[TD([[makeQuery(id+"F38.imprint","IMPRINT",EDGE,{"disambiguationData":[TD([[subQ2,1.0]])],"derivedFrom":subQ1}),-1.0]])]});}
            var Q35;
            Q35=makeQuery(id+"F38.imprint","IMPRINT",FACE,{"disambiguationData":[TD([[makeQuery(id+"F38.imprint","IMPRINT",EDGE,{"derivedFrom":sQuery(id+"F38.wireOp",EDGE,"E560.bottom")}),1.0]])]});
            var Q36;
            Q36=makeQuery(id+"F38.imprint","IMPRINT",FACE,{"disambiguationData":[TD([[makeQuery(id+"F38.imprint","IMPRINT",EDGE,{"derivedFrom":sQuery(id+"F38.wireOp",EDGE,"E558.bottom")}),1.0]])]});
            extrude(context, id + "F39", {"entities" : qUnion([Q0, Q1, Q2, Q3, Q4, Q5, Q6, Q7, Q8, Q9, Q10, Q11, Q12, Q13, Q14, Q15, Q16, Q17, Q18, Q19, Q20, Q21, Q22, Q23, Q24, Q25, Q26, Q27, Q28, Q29, Q30, Q31, Q32, Q33, Q34, Q35, Q36]), "operationType" : NewBodyOperationType.REMOVE, "oppositeDirection" : true, "depth" : 10.4 * mm});
        }
        {
            var Q0;
            {Q0=qUnion([makeQuery(id+"F38.imprint","IMPRINT",FACE,{"disambiguationData":[TD([[makeQuery(id+"F38.imprint","IMPRINT",EDGE,{"derivedFrom":sQuery(id+"F38.wireOp",EDGE,"E525.bottom")}),-1.0]])]}),makeQuery(id+"F38.imprint","IMPRINT",FACE,{"disambiguationData":[TD([[makeQuery(id+"F38.imprint","IMPRINT",EDGE,{"derivedFrom":sQuery(id+"F38.wireOp",EDGE,"E557.bottom")}),-1.0]])]}),makeQuery(id+"F38.imprint","IMPRINT",FACE,{"disambiguationData":[TD([[makeQuery(id+"F38.imprint","IMPRINT",EDGE,{"derivedFrom":sQuery(id+"F38.wireOp",EDGE,"E559.bottom")}),-1.0]])]}),makeQuery(id+"F38.imprint","IMPRINT",FACE,{"disambiguationData":[TD([[makeQuery(id+"F38.imprint","IMPRINT",EDGE,{"derivedFrom":sQuery(id+"F38.wireOp",EDGE,"E527.bottom")}),-1.0]])]})]);}
            var Q1;
            {var subQ27=sQuery(id+"F38.wireOp",EDGE,"E554.left");Q1=makeQuery(id+"F38.imprint","IMPRINT",FACE,{"disambiguationData":[TD([[makeQuery(id+"F38.imprint","IMPRINT",EDGE,{"derivedFrom":subQ27}),1.0]])]});}
            var Q2;
            {var subQ9=sQuery(id+"F38.wireOp",EDGE,"E554.right");Q2=makeQuery(id+"F38.imprint","IMPRINT",FACE,{"disambiguationData":[TD([[makeQuery(id+"F38.imprint","IMPRINT",EDGE,{"derivedFrom":subQ9}),-1.0]])]});}
            var Q3;
            {var subQ2=sQuery(id+"F38.wireOp",EDGE,"E555");Q3=makeQuery(id+"F38.imprint","IMPRINT",FACE,{"disambiguationData":[TD([[makeQuery(id+"F38.imprint","IMPRINT",EDGE,{"derivedFrom":subQ2}),-1.0]])]});}
            var Q4;
            {var subQ0=sQuery(id+"F38.wireOp",EDGE,"E542");var subQ1=sQuery(id+"F38.wireOp",EDGE,"E541.bottom");var subQ2=makeQuery(id+"F38.imprint","INTERSECT",VERTEX,{"derivedFrom":[subQ1,subQ0]});Q4=makeQuery(id+"F38.imprint","IMPRINT",FACE,{"disambiguationData":[TD([[makeQuery(id+"F38.imprint","IMPRINT",EDGE,{"disambiguationData":[TD([[subQ2,1.0]])],"derivedFrom":subQ1}),-1.0]])]});}
            var Q5;
            {var subQ0=sQuery(id+"F38.wireOp",EDGE,"E544");var subQ1=sQuery(id+"F38.wireOp",EDGE,"E541.right");var subQ2=makeQuery(id+"F38.imprint","INTERSECT",VERTEX,{"derivedFrom":[subQ1,subQ0]});Q5=makeQuery(id+"F38.imprint","IMPRINT",FACE,{"disambiguationData":[TD([[makeQuery(id+"F38.imprint","IMPRINT",EDGE,{"disambiguationData":[TD([[subQ2,-1.0]])],"derivedFrom":subQ1}),-1.0]])]});}
            var Q6;
            {var subQ0=sQuery(id+"F38.wireOp",EDGE,"E544");var subQ1=sQuery(id+"F38.wireOp",EDGE,"E542");var subQ2=makeQuery(id+"F38.imprint","INTERSECT",VERTEX,{"derivedFrom":[subQ1,subQ0]});Q6=makeQuery(id+"F38.imprint","IMPRINT",FACE,{"disambiguationData":[TD([[makeQuery(id+"F38.imprint","IMPRINT",EDGE,{"disambiguationData":[TD([[subQ2,-1.0]])],"derivedFrom":subQ1}),-1.0]])]});}
            var Q7;
            {var subQ0=sQuery(id+"F38.wireOp",EDGE,"E544");var subQ1=sQuery(id+"F38.wireOp",EDGE,"E541.left");var subQ2=makeQuery(id+"F38.imprint","INTERSECT",VERTEX,{"derivedFrom":[subQ1,subQ0]});Q7=makeQuery(id+"F38.imprint","IMPRINT",FACE,{"disambiguationData":[TD([[makeQuery(id+"F38.imprint","IMPRINT",EDGE,{"disambiguationData":[TD([[subQ2,-1.0]])],"derivedFrom":subQ1}),1.0]])]});}
            var Q8;
            {var subQ0=sQuery(id+"F38.wireOp",EDGE,"E545");var subQ1=sQuery(id+"F38.wireOp",EDGE,"E542");var subQ2=makeQuery(id+"F38.imprint","INTERSECT",VERTEX,{"derivedFrom":[subQ1,subQ0]});Q8=makeQuery(id+"F38.imprint","IMPRINT",FACE,{"disambiguationData":[TD([[makeQuery(id+"F38.imprint","IMPRINT",EDGE,{"disambiguationData":[TD([[subQ2,-1.0]])],"derivedFrom":subQ1}),-1.0]])]});}
            var Q9;
            {var subQ0=sQuery(id+"F38.wireOp",EDGE,"E547");var subQ1=sQuery(id+"F38.wireOp",EDGE,"E541.right");var subQ2=makeQuery(id+"F38.imprint","INTERSECT",VERTEX,{"derivedFrom":[subQ1,subQ0]});Q9=makeQuery(id+"F38.imprint","IMPRINT",FACE,{"disambiguationData":[TD([[makeQuery(id+"F38.imprint","IMPRINT",EDGE,{"disambiguationData":[TD([[subQ2,1.0]])],"derivedFrom":subQ1}),-1.0]])]});}
            var Q10;
            {var subQ0=sQuery(id+"F38.wireOp",EDGE,"E547");var subQ1=sQuery(id+"F38.wireOp",EDGE,"E541.left");var subQ2=makeQuery(id+"F38.imprint","INTERSECT",VERTEX,{"derivedFrom":[subQ1,subQ0]});Q10=makeQuery(id+"F38.imprint","IMPRINT",FACE,{"disambiguationData":[TD([[makeQuery(id+"F38.imprint","IMPRINT",EDGE,{"disambiguationData":[TD([[subQ2,1.0]])],"derivedFrom":subQ1}),1.0]])]});}
            var Q11;
            {var subQ0=sQuery(id+"F38.wireOp",EDGE,"E547");var subQ1=sQuery(id+"F38.wireOp",EDGE,"E542");var subQ2=makeQuery(id+"F38.imprint","INTERSECT",VERTEX,{"derivedFrom":[subQ1,subQ0]});Q11=makeQuery(id+"F38.imprint","IMPRINT",FACE,{"disambiguationData":[TD([[makeQuery(id+"F38.imprint","IMPRINT",EDGE,{"disambiguationData":[TD([[subQ2,1.0]])],"derivedFrom":subQ1}),-1.0]])]});}
            var Q12;
            {var subQ0=sQuery(id+"F38.wireOp",EDGE,"E542");var subQ1=sQuery(id+"F38.wireOp",EDGE,"E541.top");var subQ2=makeQuery(id+"F38.imprint","INTERSECT",VERTEX,{"derivedFrom":[subQ1,subQ0]});Q12=makeQuery(id+"F38.imprint","IMPRINT",FACE,{"disambiguationData":[TD([[makeQuery(id+"F38.imprint","IMPRINT",EDGE,{"disambiguationData":[TD([[subQ2,1.0]])],"derivedFrom":subQ1}),1.0]])]});}
            var Q13;
            {var subQ0=sQuery(id+"F38.wireOp",EDGE,"E529");var subQ1=sQuery(id+"F38.wireOp",EDGE,"E528.top");var subQ2=makeQuery(id+"F38.imprint","INTERSECT",VERTEX,{"derivedFrom":[subQ1,subQ0]});Q13=makeQuery(id+"F38.imprint","IMPRINT",FACE,{"disambiguationData":[TD([[makeQuery(id+"F38.imprint","IMPRINT",EDGE,{"disambiguationData":[TD([[subQ2,1.0]])],"derivedFrom":subQ1}),1.0]])]});}
            var Q14;
            {var subQ0=sQuery(id+"F38.wireOp",EDGE,"E534");var subQ1=sQuery(id+"F38.wireOp",EDGE,"E529");var subQ2=makeQuery(id+"F38.imprint","INTERSECT",VERTEX,{"derivedFrom":[subQ1,subQ0]});Q14=makeQuery(id+"F38.imprint","IMPRINT",FACE,{"disambiguationData":[TD([[makeQuery(id+"F38.imprint","IMPRINT",EDGE,{"disambiguationData":[TD([[subQ2,1.0]])],"derivedFrom":subQ1}),-1.0]])]});}
            var Q15;
            {var subQ0=sQuery(id+"F38.wireOp",EDGE,"E533");var subQ1=sQuery(id+"F38.wireOp",EDGE,"E528.right");var subQ2=makeQuery(id+"F38.imprint","INTERSECT",VERTEX,{"derivedFrom":[subQ1,subQ0]});Q15=makeQuery(id+"F38.imprint","IMPRINT",FACE,{"disambiguationData":[TD([[makeQuery(id+"F38.imprint","IMPRINT",EDGE,{"disambiguationData":[TD([[subQ2,-1.0]])],"derivedFrom":subQ1}),-1.0]])]});}
            var Q16;
            {var subQ0=sQuery(id+"F38.wireOp",EDGE,"E533");var subQ1=sQuery(id+"F38.wireOp",EDGE,"E528.left");var subQ2=makeQuery(id+"F38.imprint","INTERSECT",VERTEX,{"derivedFrom":[subQ1,subQ0]});Q16=makeQuery(id+"F38.imprint","IMPRINT",FACE,{"disambiguationData":[TD([[makeQuery(id+"F38.imprint","IMPRINT",EDGE,{"disambiguationData":[TD([[subQ2,-1.0]])],"derivedFrom":subQ1}),1.0]])]});}
            var Q17;
            {var subQ0=sQuery(id+"F38.wireOp",EDGE,"E532");var subQ1=sQuery(id+"F38.wireOp",EDGE,"E529");var subQ2=makeQuery(id+"F38.imprint","INTERSECT",VERTEX,{"derivedFrom":[subQ1,subQ0]});Q17=makeQuery(id+"F38.imprint","IMPRINT",FACE,{"disambiguationData":[TD([[makeQuery(id+"F38.imprint","IMPRINT",EDGE,{"disambiguationData":[TD([[subQ2,-1.0]])],"derivedFrom":subQ1}),-1.0]])]});}
            var Q18;
            {var subQ0=sQuery(id+"F38.wireOp",EDGE,"E532");var subQ1=sQuery(id+"F38.wireOp",EDGE,"E528.right");var subQ2=makeQuery(id+"F38.imprint","INTERSECT",VERTEX,{"derivedFrom":[subQ1,subQ0]});Q18=makeQuery(id+"F38.imprint","IMPRINT",FACE,{"disambiguationData":[TD([[makeQuery(id+"F38.imprint","IMPRINT",EDGE,{"disambiguationData":[TD([[subQ2,1.0]])],"derivedFrom":subQ1}),-1.0]])]});}
            var Q19;
            {var subQ0=sQuery(id+"F38.wireOp",EDGE,"E531");var subQ1=sQuery(id+"F38.wireOp",EDGE,"E529");var subQ2=makeQuery(id+"F38.imprint","INTERSECT",VERTEX,{"derivedFrom":[subQ1,subQ0]});Q19=makeQuery(id+"F38.imprint","IMPRINT",FACE,{"disambiguationData":[TD([[makeQuery(id+"F38.imprint","IMPRINT",EDGE,{"disambiguationData":[TD([[subQ2,-1.0]])],"derivedFrom":subQ1}),-1.0]])]});}
            var Q20;
            {var subQ0=sQuery(id+"F38.wireOp",EDGE,"E532");var subQ1=sQuery(id+"F38.wireOp",EDGE,"E528.left");var subQ2=makeQuery(id+"F38.imprint","INTERSECT",VERTEX,{"derivedFrom":[subQ1,subQ0]});Q20=makeQuery(id+"F38.imprint","IMPRINT",FACE,{"disambiguationData":[TD([[makeQuery(id+"F38.imprint","IMPRINT",EDGE,{"disambiguationData":[TD([[subQ2,1.0]])],"derivedFrom":subQ1}),1.0]])]});}
            var Q21;
            {var subQ0=sQuery(id+"F38.wireOp",EDGE,"E529");var subQ1=sQuery(id+"F38.wireOp",EDGE,"E528.bottom");var subQ2=makeQuery(id+"F38.imprint","INTERSECT",VERTEX,{"derivedFrom":[subQ1,subQ0]});Q21=makeQuery(id+"F38.imprint","IMPRINT",FACE,{"disambiguationData":[TD([[makeQuery(id+"F38.imprint","IMPRINT",EDGE,{"disambiguationData":[TD([[subQ2,1.0]])],"derivedFrom":subQ1}),-1.0]])]});}
            extrude(context, id + "F40", {"entities" : qUnion([Q0, Q1, Q2, Q3, Q4, Q5, Q6, Q7, Q8, Q9, Q10, Q11, Q12, Q13, Q14, Q15, Q16, Q17, Q18, Q19, Q20, Q21]), "operationType" : NewBodyOperationType.ADD, "oppositeDirection" : true, "depth" : 2.54 * mm, "hasSecondDirection" : true, "secondDirectionOppositeDirection" : true, "secondDirectionDepth" : 1.27 * mm});
        }
        {
            var Q0;
            Q0=makeQuery(id+"F1.opExtrude","SWEPT_FACE",FACE,{"disambiguationData":[OSD([sQuery(id+"F0.wireOp",EDGE,"E8")])]});
            var sketch = newSketch(context, id + "F41", { "sketchPlane" : qUnion([Q0])});
            skLineSegment(sketch, "E561.bottom", {"start": v(-139.7, 0) * mm, "end": v(-114.3, 0) * mm});
            skLineSegment(sketch, "E561.top", {"start": v(-139.7, 57.15) * mm, "end": v(-114.3, 57.15) * mm});
            skLineSegment(sketch, "E561.left", {"start": v(-139.7, 0) * mm, "end": v(-139.7, 57.15) * mm});
            skLineSegment(sketch, "E561.right", {"start": v(-114.3, 0) * mm, "end": v(-114.3, 57.15) * mm});
            skLineSegment(sketch, "E562", {"start": v(-138.94, 0) * mm, "end": v(-138.94, 56.39) * mm});
            skLineSegment(sketch, "E563", {"start": v(-138.94, 56.39) * mm, "end": v(-115.06, 56.39) * mm});
            skLineSegment(sketch, "E564", {"start": v(-115.06, 56.39) * mm, "end": v(-115.06, 0) * mm});
            skLineSegment(sketch, "E565.bottom", {"start": v(-136.9, 17.27) * mm, "end": v(-117.1, 17.27) * mm});
            skLineSegment(sketch, "E565.top", {"start": v(-136.9, 2.03) * mm, "end": v(-117.1, 2.03) * mm});
            skLineSegment(sketch, "E565.left", {"start": v(-136.9, 17.27) * mm, "end": v(-136.9, 2.03) * mm});
            skLineSegment(sketch, "E565.right", {"start": v(-117.1, 17.27) * mm, "end": v(-117.1, 2.03) * mm});
            skPoint(sketch, "E566.oppositeSnap0", {"position": v(-117.1, 9.65) * mm});
            skLineSegment(sketch, "E566.bottom", {"start": v(-136.9, 34.54) * mm, "end": v(-117.1, 34.54) * mm});
            skLineSegment(sketch, "E566.top", {"start": v(-136.9, 19.3) * mm, "end": v(-117.1, 19.3) * mm});
            skLineSegment(sketch, "E566.left", {"start": v(-136.9, 34.54) * mm, "end": v(-136.9, 19.3) * mm});
            skLineSegment(sketch, "E566.right", {"start": v(-117.1, 34.54) * mm, "end": v(-117.1, 19.3) * mm});
            skLineSegment(sketch, "E567.bottom", {"start": v(-136.9, 54.36) * mm, "end": v(-127.32, 54.36) * mm});
            skLineSegment(sketch, "E567.top", {"start": v(-136.9, 45.78) * mm, "end": v(-127.32, 45.78) * mm});
            skLineSegment(sketch, "E567.left", {"start": v(-136.9, 54.36) * mm, "end": v(-136.9, 45.78) * mm});
            skLineSegment(sketch, "E567.right", {"start": v(-127.32, 54.36) * mm, "end": v(-127.32, 45.78) * mm});
            skLineSegment(sketch, "E568.bottom", {"start": v(-126.68, 54.36) * mm, "end": v(-117.1, 54.36) * mm});
            skLineSegment(sketch, "E568.top", {"start": v(-126.68, 45.78) * mm, "end": v(-117.1, 45.78) * mm});
            skLineSegment(sketch, "E568.left", {"start": v(-126.68, 54.36) * mm, "end": v(-126.68, 45.78) * mm});
            skLineSegment(sketch, "E568.right", {"start": v(-117.1, 54.36) * mm, "end": v(-117.1, 45.78) * mm});
            skLineSegment(sketch, "E569.bottom", {"start": v(-117.1, 45.15) * mm, "end": v(-126.68, 45.15) * mm});
            skLineSegment(sketch, "E569.top", {"start": v(-117.1, 36.58) * mm, "end": v(-126.68, 36.58) * mm});
            skLineSegment(sketch, "E569.left", {"start": v(-117.1, 45.15) * mm, "end": v(-117.1, 36.58) * mm});
            skLineSegment(sketch, "E569.right", {"start": v(-126.68, 45.15) * mm, "end": v(-126.68, 36.58) * mm});
            skLineSegment(sketch, "E570.bottom", {"start": v(-127.32, 45.15) * mm, "end": v(-136.9, 45.15) * mm});
            skLineSegment(sketch, "E570.top", {"start": v(-127.32, 36.58) * mm, "end": v(-136.9, 36.58) * mm});
            skLineSegment(sketch, "E570.left", {"start": v(-127.32, 45.15) * mm, "end": v(-127.32, 36.58) * mm});
            skLineSegment(sketch, "E570.right", {"start": v(-136.9, 45.15) * mm, "end": v(-136.9, 36.58) * mm});
            skSolve(sketch);
        }
        {
            var Q0;
            Q0 = qSketchRegion(id + "F41", true);
            var Q1;
            Q1=makeQuery(id+"F41.imprint","IMPRINT",FACE,{"disambiguationData":[TD([[makeQuery(id+"F41.imprint","IMPRINT",EDGE,{"derivedFrom":sQuery(id+"F41.wireOp",EDGE,"E567.bottom")}),-1.0]])]});
            var Q2;
            Q2=makeQuery(id+"F41.imprint","IMPRINT",FACE,{"disambiguationData":[TD([[makeQuery(id+"F41.imprint","IMPRINT",EDGE,{"derivedFrom":sQuery(id+"F41.wireOp",EDGE,"E568.bottom")}),-1.0]])]});
            var Q3;
            Q3=makeQuery(id+"F41.imprint","IMPRINT",FACE,{"disambiguationData":[TD([[makeQuery(id+"F41.imprint","IMPRINT",EDGE,{"derivedFrom":sQuery(id+"F41.wireOp",EDGE,"E569.bottom")}),1.0]])]});
            var Q4;
            Q4=makeQuery(id+"F41.imprint","IMPRINT",FACE,{"disambiguationData":[TD([[makeQuery(id+"F41.imprint","IMPRINT",EDGE,{"derivedFrom":sQuery(id+"F41.wireOp",EDGE,"E570.bottom")}),1.0]])]});
            var Q5;
            Q5=makeQuery(id+"F41.imprint","IMPRINT",FACE,{"disambiguationData":[TD([[makeQuery(id+"F41.imprint","IMPRINT",EDGE,{"derivedFrom":sQuery(id+"F41.wireOp",EDGE,"E566.bottom")}),-1.0]])]});
            var Q6;
            Q6=makeQuery(id+"F41.imprint","IMPRINT",FACE,{"disambiguationData":[TD([[makeQuery(id+"F41.imprint","IMPRINT",EDGE,{"derivedFrom":sQuery(id+"F41.wireOp",EDGE,"E565.bottom")}),-1.0]])]});
            extrude(context, id + "F42", {"entities" : qUnion([Q0, Q1, Q2, Q3, Q4, Q5, Q6]), "operationType" : NewBodyOperationType.REMOVE, "oppositeDirection" : true, "depth" : 10.4 * mm});
        }
        {
            var Q0;
            Q0=makeQuery(id+"F41.imprint","IMPRINT",FACE,{"disambiguationData":[TD([[makeQuery(id+"F41.imprint","IMPRINT",EDGE,{"derivedFrom":sQuery(id+"F41.wireOp",EDGE,"E561.top")}),-1.0]])]});
            extrude(context, id + "F43", {"entities" : qUnion([Q0]), "operationType" : NewBodyOperationType.ADD, "oppositeDirection" : true, "depth" : 4.32 * mm, "hasSecondDirection" : true, "secondDirectionOppositeDirection" : true, "secondDirectionDepth" : 1.27 * mm});
        }
        {
            var Q0;
            {var subQ1=sQuery(id+"F41.wireOp",EDGE,"E562");Q0=makeQuery(id+"F41.imprint","IMPRINT",FACE,{"disambiguationData":[TD([[makeQuery(id+"F41.imprint","IMPRINT",EDGE,{"derivedFrom":subQ1}),-1.0]])]});}
            extrude(context, id + "F44", {"entities" : qUnion([Q0]), "operationType" : NewBodyOperationType.ADD, "oppositeDirection" : true, "depth" : 2.54 * mm, "hasSecondDirection" : true, "secondDirectionOppositeDirection" : true, "secondDirectionDepth" : 1.27 * mm});
        }
        {
            var Q0;
            Q0=makeQuery(id+"F41.imprint","IMPRINT",FACE,{"disambiguationData":[TD([[makeQuery(id+"F41.imprint","IMPRINT",EDGE,{"derivedFrom":sQuery(id+"F41.wireOp",EDGE,"E566.bottom")}),-1.0]])]});
            var Q1;
            Q1=makeQuery(id+"F41.imprint","IMPRINT",FACE,{"disambiguationData":[TD([[makeQuery(id+"F41.imprint","IMPRINT",EDGE,{"derivedFrom":sQuery(id+"F41.wireOp",EDGE,"E565.bottom")}),-1.0]])]});
            extrude(context, id + "F45", {"entities" : qUnion([Q0, Q1]), "operationType" : NewBodyOperationType.ADD, "oppositeDirection" : true, "depth" : 2.54 * mm, "hasSecondDirection" : true, "secondDirectionOppositeDirection" : true, "secondDirectionDepth" : 0.89 * mm});
        }
        {
            var Q0;
            Q0=makeQuery(id+"F1.opExtrude","SWEPT_FACE",FACE,{"disambiguationData":[OSD([sQuery(id+"F0.wireOp",EDGE,"E42")])]});
            var sketch = newSketch(context, id + "F46", { "sketchPlane" : qUnion([Q0])});
            skLineSegment(sketch, "E571.bottom", {"start": v(106.59, 0) * mm, "end": v(129.45, 0) * mm});
            skLineSegment(sketch, "E571.top", {"start": v(106.59, 57.15) * mm, "end": v(129.45, 57.15) * mm});
            skLineSegment(sketch, "E571.left", {"start": v(106.59, 0) * mm, "end": v(106.59, 57.15) * mm});
            skLineSegment(sketch, "E571.right", {"start": v(129.45, 0) * mm, "end": v(129.45, 57.15) * mm});
            skSolve(sketch);
        }
        {
            var Q0;
            Q0 = qSketchRegion(id + "F46", true);
            extrude(context, id + "F47", {"entities" : qUnion([Q0]), "operationType" : NewBodyOperationType.REMOVE, "oppositeDirection" : true, "depth" : 50.8 * mm});
        }
        {
            var Q0;
            Q0=makeQuery(id+"F2.boolean.opBoolean","MERGE",FACE,{"derivedFrom":[makeQuery(id+"F1.opExtrude","SWEPT_FACE",FACE,{"disambiguationData":[OSD([sQuery(id+"F0.wireOp",EDGE,"E43")])]}),makeQuery(id+"F2.opExtrude","SWEPT_FACE",FACE,{"disambiguationData":[OSD([sQuery(id+"F0.wireOp",EDGE,"E50")])]})]});
            var sketch = newSketch(context, id + "F48", { "sketchPlane" : qUnion([Q0])});
            skLineSegment(sketch, "E572.bottom", {"start": v(216, 0) * mm, "end": v(238.86, 0) * mm});
            skLineSegment(sketch, "E572.top", {"start": v(216, 57.15) * mm, "end": v(238.86, 57.15) * mm});
            skLineSegment(sketch, "E572.left", {"start": v(216, 0) * mm, "end": v(216, 57.15) * mm});
            skLineSegment(sketch, "E572.right", {"start": v(238.86, 0) * mm, "end": v(238.86, 57.15) * mm});
            skSolve(sketch);
        }
        {
            var Q0;
            Q0 = qSketchRegion(id + "F48", true);
            extrude(context, id + "F49", {"entities" : qUnion([Q0]), "operationType" : NewBodyOperationType.REMOVE, "oppositeDirection" : true, "depth" : 2.54 * mm});
        }
        {
            var Q0;
            Q0=makeQuery(id+"F3.opExtrude","SWEPT_FACE",FACE,{"disambiguationData":[OSD([sQuery(id+"F0.wireOp",EDGE,"E11.3")])]});
            var sketch = newSketch(context, id + "F50", { "sketchPlane" : qUnion([Q0])});
            skSolve(sketch);
        }
        {
            var Q0;
            {var subQ0=sQuery(id+"F0.wireOp",EDGE,"E11.3");Q0=makeQuery(id+"F50.imprint","IMPRINT",FACE,{"disambiguationData":[TD([[makeQuery(id+"F50.imprint","IMPRINT",EDGE,{"derivedFrom":makeQuery(id+"F3.opExtrude","CAP_EDGE",EDGE,{"disambiguationData":[OSD([subQ0])],"isStart":true})}),-1.0]])]});}
            var sketch = newSketch(context, id + "F51", { "sketchPlane" : qUnion([Q0])});
            skLineSegment(sketch, "E573.bottom", {"start": v(-41.46, 0) * mm, "end": v(-10.98, 0) * mm});
            skLineSegment(sketch, "E573.top", {"start": v(-41.46, 57.15) * mm, "end": v(-10.98, 57.15) * mm});
            skLineSegment(sketch, "E573.left", {"start": v(-41.46, 0) * mm, "end": v(-41.46, 57.15) * mm});
            skLineSegment(sketch, "E573.right", {"start": v(-10.98, 0) * mm, "end": v(-10.98, 57.15) * mm});
            skSolve(sketch);
        }
        {
            var Q0;
            Q0 = qSketchRegion(id + "F51", true);
            extrude(context, id + "F52", {"entities" : qUnion([Q0]), "operationType" : NewBodyOperationType.REMOVE, "oppositeDirection" : true, "depth" : 10.16 * mm});
        }
        {
            var Q0;
            Q0=makeQuery(id+"F1.opExtrude","SWEPT_FACE",FACE,{"disambiguationData":[OSD([sQuery(id+"F0.wireOp",EDGE,"E27")])]});
            var sketch = newSketch(context, id + "F53", { "sketchPlane" : qUnion([Q0])});
            skLineSegment(sketch, "E574.bottom", {"start": v(-262.7, 0) * mm, "end": v(-239.84, 0) * mm});
            skLineSegment(sketch, "E574.top", {"start": v(-262.7, 57.15) * mm, "end": v(-239.84, 57.15) * mm});
            skLineSegment(sketch, "E574.left", {"start": v(-262.7, 0) * mm, "end": v(-262.7, 57.15) * mm});
            skLineSegment(sketch, "E574.right", {"start": v(-239.84, 0) * mm, "end": v(-239.84, 57.15) * mm});
            skSolve(sketch);
        }
        {
            var Q0;
            Q0 = qSketchRegion(id + "F53", true);
            extrude(context, id + "F54", {"entities" : qUnion([Q0]), "operationType" : NewBodyOperationType.REMOVE, "oppositeDirection" : true, "depth" : 2.54 * mm});
        }
        {
            var Q0;
            Q0=makeQuery(id+"F3.opExtrude","SWEPT_FACE",FACE,{"disambiguationData":[OSD([sQuery(id+"F0.wireOp",EDGE,"E11.1")])]});
            var sketch = newSketch(context, id + "F55", { "sketchPlane" : qUnion([Q0])});
            skLineSegment(sketch, "E575.bottom", {"start": v(272.5, 0) * mm, "end": v(295, 0) * mm});
            skLineSegment(sketch, "E575.top", {"start": v(272.5, 57.15) * mm, "end": v(295, 57.15) * mm});
            skLineSegment(sketch, "E575.left", {"start": v(272.5, 0) * mm, "end": v(272.5, 57.15) * mm});
            skLineSegment(sketch, "E575.right", {"start": v(295, 0) * mm, "end": v(295, 57.15) * mm});
            skSolve(sketch);
        }
        {
            var Q0;
            Q0 = qSketchRegion(id + "F55", true);
            extrude(context, id + "F56", {"entities" : qUnion([Q0]), "operationType" : NewBodyOperationType.REMOVE, "oppositeDirection" : true, "depth" : 10.16 * mm});
        }
        {
            var Q0;
            Q0=makeQuery(id+"F1.opExtrude","SWEPT_FACE",FACE,{"disambiguationData":[OSD([sQuery(id+"F0.wireOp",EDGE,"E36"),sQuery(id+"F0.wireOp",EDGE,"E37"),sQuery(id+"F0.wireOp",EDGE,"E38")])]});
            var sketch = newSketch(context, id + "F57", { "sketchPlane" : qUnion([Q0])});
            skPoint(sketch, "E576.firstSnap0", {"position": v(-88.65, 66.04) * mm});
            skLineSegment(sketch, "E576.bottom", {"start": v(-88.65, 66.04) * mm, "end": v(-95, 66.04) * mm});
            skLineSegment(sketch, "E576.top", {"start": v(-88.65, 63.5) * mm, "end": v(-95, 63.5) * mm});
            skLineSegment(sketch, "E576.left", {"start": v(-88.65, 66.04) * mm, "end": v(-88.65, 63.5) * mm});
            skLineSegment(sketch, "E576.right", {"start": v(-95, 66.04) * mm, "end": v(-95, 63.5) * mm});
            skLineSegment(sketch, "E577.bottom", {"start": v(-95, 59.7) * mm, "end": v(-101.35, 59.7) * mm});
            skLineSegment(sketch, "E577.top", {"start": v(-95, 57.15) * mm, "end": v(-101.35, 57.15) * mm});
            skLineSegment(sketch, "E577.left", {"start": v(-95, 59.7) * mm, "end": v(-95, 57.15) * mm});
            skLineSegment(sketch, "E577.right", {"start": v(-101.35, 59.7) * mm, "end": v(-101.35, 57.15) * mm});
            skLineSegment(sketch, "E578.bottom", {"start": v(-101.35, 53.34) * mm, "end": v(-107.7, 53.34) * mm});
            skLineSegment(sketch, "E578.top", {"start": v(-101.35, 50.8) * mm, "end": v(-107.7, 50.8) * mm});
            skLineSegment(sketch, "E578.left", {"start": v(-101.35, 53.34) * mm, "end": v(-101.35, 50.8) * mm});
            skLineSegment(sketch, "E578.right", {"start": v(-107.7, 53.34) * mm, "end": v(-107.7, 50.8) * mm});
            skLineSegment(sketch, "E579.bottom", {"start": v(-107.7, 47) * mm, "end": v(-114.05, 47) * mm});
            skLineSegment(sketch, "E579.top", {"start": v(-107.7, 44.45) * mm, "end": v(-114.05, 44.45) * mm});
            skLineSegment(sketch, "E579.left", {"start": v(-107.7, 47) * mm, "end": v(-107.7, 44.45) * mm});
            skLineSegment(sketch, "E579.right", {"start": v(-114.05, 47) * mm, "end": v(-114.05, 44.45) * mm});
            skLineSegment(sketch, "E580.bottom", {"start": v(-114.05, 40.64) * mm, "end": v(-120.4, 40.64) * mm});
            skLineSegment(sketch, "E580.top", {"start": v(-114.05, 38.1) * mm, "end": v(-120.4, 38.1) * mm});
            skLineSegment(sketch, "E580.left", {"start": v(-114.05, 40.64) * mm, "end": v(-114.05, 38.1) * mm});
            skLineSegment(sketch, "E580.right", {"start": v(-120.4, 40.64) * mm, "end": v(-120.4, 38.1) * mm});
            skLineSegment(sketch, "E581.bottom", {"start": v(-120.4, 34.29) * mm, "end": v(-126.75, 34.29) * mm});
            skLineSegment(sketch, "E581.top", {"start": v(-120.4, 31.75) * mm, "end": v(-126.75, 31.75) * mm});
            skLineSegment(sketch, "E581.left", {"start": v(-120.4, 34.29) * mm, "end": v(-120.4, 31.75) * mm});
            skLineSegment(sketch, "E581.right", {"start": v(-126.75, 34.29) * mm, "end": v(-126.75, 31.75) * mm});
            skLineSegment(sketch, "E582.bottom", {"start": v(-126.75, 27.94) * mm, "end": v(-133.1, 27.94) * mm});
            skLineSegment(sketch, "E582.top", {"start": v(-126.75, 25.4) * mm, "end": v(-133.1, 25.4) * mm});
            skLineSegment(sketch, "E582.left", {"start": v(-126.75, 27.94) * mm, "end": v(-126.75, 25.4) * mm});
            skLineSegment(sketch, "E582.right", {"start": v(-133.1, 27.94) * mm, "end": v(-133.1, 25.4) * mm});
            skLineSegment(sketch, "E583.bottom", {"start": v(-133.1, 21.59) * mm, "end": v(-139.45, 21.59) * mm});
            skLineSegment(sketch, "E583.top", {"start": v(-133.1, 19.05) * mm, "end": v(-139.45, 19.05) * mm});
            skLineSegment(sketch, "E583.left", {"start": v(-133.1, 21.59) * mm, "end": v(-133.1, 19.05) * mm});
            skLineSegment(sketch, "E583.right", {"start": v(-139.45, 21.59) * mm, "end": v(-139.45, 19.05) * mm});
            skLineSegment(sketch, "E584.bottom", {"start": v(-139.45, 15.24) * mm, "end": v(-145.8, 15.24) * mm});
            skLineSegment(sketch, "E584.top", {"start": v(-139.45, 12.7) * mm, "end": v(-145.8, 12.7) * mm});
            skLineSegment(sketch, "E584.left", {"start": v(-139.45, 15.24) * mm, "end": v(-139.45, 12.7) * mm});
            skLineSegment(sketch, "E584.right", {"start": v(-145.8, 15.24) * mm, "end": v(-145.8, 12.7) * mm});
            skLineSegment(sketch, "E585.bottom", {"start": v(-145.8, 8.89) * mm, "end": v(-152.15, 8.89) * mm});
            skLineSegment(sketch, "E585.top", {"start": v(-145.8, 6.35) * mm, "end": v(-152.15, 6.35) * mm});
            skLineSegment(sketch, "E585.left", {"start": v(-145.8, 8.89) * mm, "end": v(-145.8, 6.35) * mm});
            skLineSegment(sketch, "E585.right", {"start": v(-152.15, 8.89) * mm, "end": v(-152.15, 6.35) * mm});
            skLineSegment(sketch, "E586.bottom", {"start": v(-152.15, 2.54) * mm, "end": v(-158.5, 2.54) * mm});
            skLineSegment(sketch, "E586.top", {"start": v(-152.15, 0) * mm, "end": v(-158.5, 0) * mm});
            skLineSegment(sketch, "E586.left", {"start": v(-152.15, 2.54) * mm, "end": v(-152.15, 0) * mm});
            skLineSegment(sketch, "E586.right", {"start": v(-158.5, 2.54) * mm, "end": v(-158.5, 0) * mm});
            skSolve(sketch);
        }
        {
            var Q0;
            Q0=makeQuery(id+"F57.imprint","IMPRINT",FACE,{"disambiguationData":[TD([[makeQuery(id+"F57.imprint","IMPRINT",EDGE,{"derivedFrom":sQuery(id+"F57.wireOp",EDGE,"E576.bottom")}),-1.0]])]});
            var Q1;
            Q1=makeQuery(id+"F57.imprint","IMPRINT",FACE,{"disambiguationData":[TD([[makeQuery(id+"F57.imprint","IMPRINT",EDGE,{"derivedFrom":sQuery(id+"F57.wireOp",EDGE,"E577.bottom")}),1.0]])]});
            var Q2;
            Q2=makeQuery(id+"F57.imprint","IMPRINT",FACE,{"disambiguationData":[TD([[makeQuery(id+"F57.imprint","IMPRINT",EDGE,{"derivedFrom":sQuery(id+"F57.wireOp",EDGE,"E578.bottom")}),1.0]])]});
            var Q3;
            Q3=makeQuery(id+"F57.imprint","IMPRINT",FACE,{"disambiguationData":[TD([[makeQuery(id+"F57.imprint","IMPRINT",EDGE,{"derivedFrom":sQuery(id+"F57.wireOp",EDGE,"E579.bottom")}),1.0]])]});
            var Q4;
            Q4=makeQuery(id+"F57.imprint","IMPRINT",FACE,{"disambiguationData":[TD([[makeQuery(id+"F57.imprint","IMPRINT",EDGE,{"derivedFrom":sQuery(id+"F57.wireOp",EDGE,"E580.bottom")}),1.0]])]});
            var Q5;
            Q5=makeQuery(id+"F57.imprint","IMPRINT",FACE,{"disambiguationData":[TD([[makeQuery(id+"F57.imprint","IMPRINT",EDGE,{"derivedFrom":sQuery(id+"F57.wireOp",EDGE,"E581.bottom")}),1.0]])]});
            var Q6;
            Q6=makeQuery(id+"F57.imprint","IMPRINT",FACE,{"disambiguationData":[TD([[makeQuery(id+"F57.imprint","IMPRINT",EDGE,{"derivedFrom":sQuery(id+"F57.wireOp",EDGE,"E582.bottom")}),1.0]])]});
            var Q7;
            Q7=makeQuery(id+"F57.imprint","IMPRINT",FACE,{"disambiguationData":[TD([[makeQuery(id+"F57.imprint","IMPRINT",EDGE,{"derivedFrom":sQuery(id+"F57.wireOp",EDGE,"E583.bottom")}),1.0]])]});
            var Q8;
            Q8=makeQuery(id+"F57.imprint","IMPRINT",FACE,{"disambiguationData":[TD([[makeQuery(id+"F57.imprint","IMPRINT",EDGE,{"derivedFrom":sQuery(id+"F57.wireOp",EDGE,"E584.bottom")}),1.0]])]});
            var Q9;
            Q9=makeQuery(id+"F57.imprint","IMPRINT",FACE,{"disambiguationData":[TD([[makeQuery(id+"F57.imprint","IMPRINT",EDGE,{"derivedFrom":sQuery(id+"F57.wireOp",EDGE,"E585.bottom")}),1.0]])]});
            var Q10;
            Q10=makeQuery(id+"F57.imprint","IMPRINT",FACE,{"disambiguationData":[TD([[makeQuery(id+"F57.imprint","IMPRINT",EDGE,{"derivedFrom":sQuery(id+"F57.wireOp",EDGE,"E586.bottom")}),1.0]])]});
            extrude(context, id + "F58", {"entities" : qUnion([Q0, Q1, Q2, Q3, Q4, Q5, Q6, Q7, Q8, Q9, Q10]), "operationType" : NewBodyOperationType.ADD, "depth" : 25.4 * mm});
        }
        {
            var Q0;
            Q0=makeQuery(id+"F57.imprint","IMPRINT",FACE,{"disambiguationData":[TD([[makeQuery(id+"F57.imprint","IMPRINT",EDGE,{"derivedFrom":sQuery(id+"F57.wireOp",EDGE,"E576.top")}),1.0]])]});
            var sketch = newSketch(context, id + "F59", { "sketchPlane" : qUnion([Q0])});
            skLineSegment(sketch, "E587.bottom", {"start": v(-69.53, 0) * mm, "end": v(-23.8, 0) * mm});
            skLineSegment(sketch, "E587.top", {"start": v(-69.53, 57.15) * mm, "end": v(-23.8, 57.15) * mm});
            skLineSegment(sketch, "E587.left", {"start": v(-69.53, 0) * mm, "end": v(-69.53, 57.15) * mm});
            skLineSegment(sketch, "E587.right", {"start": v(-23.8, 0) * mm, "end": v(-23.8, 57.15) * mm});
            skSolve(sketch);
        }
        {
            var Q0;
            Q0 = qSketchRegion(id + "F59", true);
            extrude(context, id + "F60", {"entities" : qUnion([Q0]), "operationType" : NewBodyOperationType.REMOVE, "oppositeDirection" : true, "depth" : 2.54 * mm});
        }
    });
